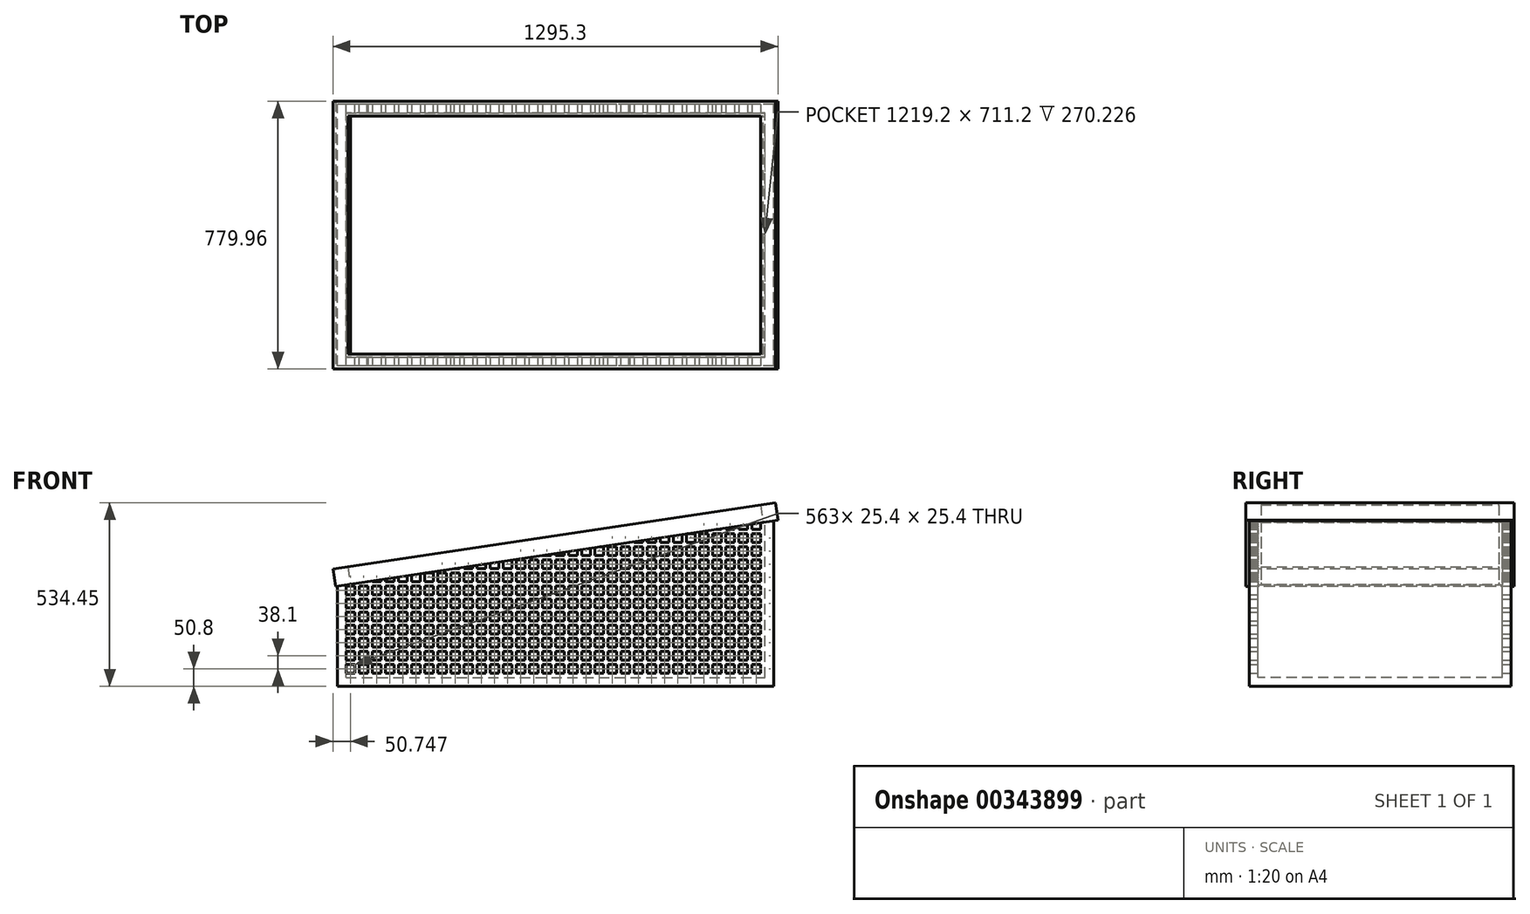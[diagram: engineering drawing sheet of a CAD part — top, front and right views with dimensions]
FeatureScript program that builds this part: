
annotation { "Feature Type Name" : "Feature", "Feature Type Description" : "" }
export const myFeature = defineFeature(function(context is Context, id is Id, definition is map)
    precondition{}
    {
        {
            var Q0;
            Q0=qCreatedBy(makeId("Top.planeOp"),FACE);
            var sketch = newSketch(context, id + "F0", { "sketchPlane" : qUnion([Q0])});
            skLineSegment(sketch, "E0.bottom", {"start": v(619.8, -571.34) * mm, "end": v(-650.2, -571.34) * mm});
            skLineSegment(sketch, "E0.top", {"start": v(619.8, 190.66) * mm, "end": v(-650.2, 190.66) * mm});
            skLineSegment(sketch, "E0.left", {"start": v(619.8, -571.34) * mm, "end": v(619.8, 190.66) * mm});
            skLineSegment(sketch, "E0.right", {"start": v(-650.2, -571.34) * mm, "end": v(-650.2, 190.66) * mm});
            skSolve(sketch);
        }
        {
            var Q0;
            Q0 = qSketchRegion(id + "F0", true);
            extrude(context, id + "F1", {"entities" : qUnion([Q0]), "depth" : 508 * mm});
        }
        {
            var Q0;
            Q0=makeQuery(id+"F1.opExtrude","SWEPT_FACE",FACE,{"disambiguationData":[OSD([sQuery(id+"F0.wireOp",EDGE,"E0.bottom")])]});
            var sketch = newSketch(context, id + "F2", { "sketchPlane" : qUnion([Q0])});
            skLineSegment(sketch, "E1.bottom", {"start": v(-650.2, 508) * mm, "end": v(619.8, 508) * mm, "construction": true});
            skLineSegment(sketch, "E1.top", {"start": v(-650.2, 317.5) * mm, "end": v(619.8, 317.5) * mm, "construction": true});
            skLineSegment(sketch, "E1.left", {"start": v(-650.2, 508) * mm, "end": v(-650.2, 317.5) * mm, "construction": true});
            skLineSegment(sketch, "E1.right", {"start": v(619.8, 508) * mm, "end": v(619.8, 317.5) * mm, "construction": true});
            skLineSegment(sketch, "E2", {"start": v(-650.2, 317.5) * mm, "end": v(619.8, 508) * mm});
            skLineSegment(sketch, "E3", {"start": v(619.8, 508) * mm, "end": v(-650.2, 508) * mm});
            skLineSegment(sketch, "E4", {"start": v(-650.2, 508) * mm, "end": v(-650.2, 317.5) * mm});
            skSolve(sketch);
        }
        {
            var Q0;
            Q0=makeQuery(id+"F1.opExtrude","CAP_FACE",FACE,{"disambiguationData":[OSD([sQuery(id+"F0.wireOp",EDGE,"E0.bottom"),sQuery(id+"F0.wireOp",EDGE,"E0.top"),sQuery(id+"F0.wireOp",EDGE,"E0.left"),sQuery(id+"F0.wireOp",EDGE,"E0.right")])],"isStart":false});
            var sketch = newSketch(context, id + "F3", { "sketchPlane" : qUnion([Q0])});
            skLineSegment(sketch, "E5.bottom", {"start": v(-624.8, 165.26) * mm, "end": v(594.4, 165.26) * mm});
            skLineSegment(sketch, "E5.top", {"start": v(-624.8, -545.94) * mm, "end": v(594.4, -545.94) * mm});
            skLineSegment(sketch, "E5.left", {"start": v(-624.8, 165.26) * mm, "end": v(-624.8, -545.94) * mm});
            skLineSegment(sketch, "E5.right", {"start": v(594.4, 165.26) * mm, "end": v(594.4, -545.94) * mm});
            skSolve(sketch);
        }
        {
            var Q0;
            Q0=makeQuery(id+"F3.imprint","IMPRINT",FACE,{"disambiguationData":[TD([[makeQuery(id+"F3.imprint","IMPRINT",EDGE,{"derivedFrom":sQuery(id+"F3.wireOp",EDGE,"E5.bottom")}),-1.0]])]});
            extrude(context, id + "F4", {"entities" : qUnion([Q0]), "operationType" : NewBodyOperationType.REMOVE, "oppositeDirection" : true, "depth" : 482.6 * mm});
        }
        {
            var Q0;
            Q0=makeQuery(id+"F2.imprint","IMPRINT",FACE,{"disambiguationData":[TD([[makeQuery(id+"F2.imprint","IMPRINT",EDGE,{"derivedFrom":sQuery(id+"F2.wireOp",EDGE,"E2")}),1.0]])]});
            extrude(context, id + "F5", {"entities" : qUnion([Q0]), "operationType" : NewBodyOperationType.REMOVE, "oppositeDirection" : true, "depth" : 762 * mm});
        }
        {
            var Q0;
            Q0=makeQuery(id+"F5.boolean.opBoolean","COPY",FACE,{"derivedFrom":makeQuery(id+"F5.opExtrude","SWEPT_FACE",FACE,{"disambiguationData":[OSD([sQuery(id+"F2.wireOp",EDGE,"E2")])]})});
            var sketch = newSketch(context, id + "F6", { "sketchPlane" : qUnion([Q0])});
            skLineSegment(sketch, "E6.bottom", {"start": v(-570.22, 165.26) * mm, "end": v(662.62, 165.26) * mm, "construction": true});
            skLineSegment(sketch, "E6.top", {"start": v(-570.22, -545.94) * mm, "end": v(662.62, -545.94) * mm, "construction": true});
            skLineSegment(sketch, "E6.left", {"start": v(-570.22, 165.26) * mm, "end": v(-570.22, -545.94) * mm, "construction": true});
            skLineSegment(sketch, "E6.right", {"start": v(662.62, 165.26) * mm, "end": v(662.62, -545.94) * mm, "construction": true});
            skLineSegment(sketch, "E7.bottom", {"start": v(688.3, 190.66) * mm, "end": v(-595.9, 190.66) * mm, "construction": true});
            skLineSegment(sketch, "E7.top", {"start": v(688.3, -571.34) * mm, "end": v(-595.9, -571.34) * mm, "construction": true});
            skLineSegment(sketch, "E7.left", {"start": v(688.3, 190.66) * mm, "end": v(688.3, -571.34) * mm, "construction": true});
            skLineSegment(sketch, "E7.right", {"start": v(-595.9, 190.66) * mm, "end": v(-595.9, -571.34) * mm, "construction": true});
            skLineSegment(sketch, "E8", {"start": v(-595.9, 190.66) * mm, "end": v(-604.88, 199.64) * mm, "construction": true});
            skLineSegment(sketch, "E9", {"start": v(-570.22, 165.26) * mm, "end": v(-561.24, 156.28) * mm, "construction": true});
            skLineSegment(sketch, "E10", {"start": v(662.62, -545.94) * mm, "end": v(653.64, -536.96) * mm, "construction": true});
            skLineSegment(sketch, "E11", {"start": v(688.3, -571.34) * mm, "end": v(697.29, -580.32) * mm, "construction": true});
            skLineSegment(sketch, "E12.bottom", {"start": v(-604.88, 199.64) * mm, "end": v(697.29, 199.64) * mm});
            skLineSegment(sketch, "E12.top", {"start": v(-604.88, -580.32) * mm, "end": v(697.29, -580.32) * mm});
            skLineSegment(sketch, "E12.left", {"start": v(-604.88, 199.64) * mm, "end": v(-604.88, -580.32) * mm});
            skLineSegment(sketch, "E12.right", {"start": v(697.29, 199.64) * mm, "end": v(697.29, -580.32) * mm});
            skLineSegment(sketch, "E13.bottom", {"start": v(653.64, -536.96) * mm, "end": v(-561.24, -536.96) * mm});
            skLineSegment(sketch, "E13.top", {"start": v(653.64, 156.28) * mm, "end": v(-561.24, 156.28) * mm});
            skLineSegment(sketch, "E13.left", {"start": v(653.64, -536.96) * mm, "end": v(653.64, 156.28) * mm});
            skLineSegment(sketch, "E13.right", {"start": v(-561.24, -536.96) * mm, "end": v(-561.24, 156.28) * mm});
            skSolve(sketch);
        }
        {
            var Q0;
            Q0=makeQuery(id+"F1.opExtrude","SWEPT_FACE",FACE,{"disambiguationData":[OSD([sQuery(id+"F0.wireOp",EDGE,"E0.top")])]});
            var sketch = newSketch(context, id + "F7", { "sketchPlane" : qUnion([Q0])});
            skLineSegment(sketch, "E14.bottom", {"start": v(-581.7, 63.5) * mm, "end": v(-556.3, 63.5) * mm});
            skLineSegment(sketch, "E14.top", {"start": v(-581.7, 38.1) * mm, "end": v(-556.3, 38.1) * mm});
            skLineSegment(sketch, "E14.left", {"start": v(-581.7, 63.5) * mm, "end": v(-581.7, 38.1) * mm});
            skLineSegment(sketch, "E14.right", {"start": v(-556.3, 63.5) * mm, "end": v(-556.3, 38.1) * mm});
            skLineSegment(sketch, "E15.0.1.0", {"start": v(-581.7, 101.6) * mm, "end": v(-556.3, 101.6) * mm});
            skLineSegment(sketch, "E15.0.1.1", {"start": v(-581.7, 101.6) * mm, "end": v(-581.7, 76.2) * mm});
            skLineSegment(sketch, "E15.0.1.2", {"start": v(-581.7, 76.2) * mm, "end": v(-556.3, 76.2) * mm});
            skLineSegment(sketch, "E15.0.1.3", {"start": v(-556.3, 101.6) * mm, "end": v(-556.3, 76.2) * mm});
            skLineSegment(sketch, "E15.0.2.0", {"start": v(-581.7, 139.7) * mm, "end": v(-556.3, 139.7) * mm});
            skLineSegment(sketch, "E15.0.2.1", {"start": v(-581.7, 139.7) * mm, "end": v(-581.7, 114.3) * mm});
            skLineSegment(sketch, "E15.0.2.2", {"start": v(-581.7, 114.3) * mm, "end": v(-556.3, 114.3) * mm});
            skLineSegment(sketch, "E15.0.2.3", {"start": v(-556.3, 139.7) * mm, "end": v(-556.3, 114.3) * mm});
            skLineSegment(sketch, "E15.0.3.0", {"start": v(-581.7, 177.8) * mm, "end": v(-556.3, 177.8) * mm});
            skLineSegment(sketch, "E15.0.3.1", {"start": v(-581.7, 177.8) * mm, "end": v(-581.7, 152.4) * mm});
            skLineSegment(sketch, "E15.0.3.2", {"start": v(-581.7, 152.4) * mm, "end": v(-556.3, 152.4) * mm});
            skLineSegment(sketch, "E15.0.3.3", {"start": v(-556.3, 177.8) * mm, "end": v(-556.3, 152.4) * mm});
            skLineSegment(sketch, "E15.0.4.0", {"start": v(-581.7, 215.9) * mm, "end": v(-556.3, 215.9) * mm});
            skLineSegment(sketch, "E15.0.4.1", {"start": v(-581.7, 215.9) * mm, "end": v(-581.7, 190.5) * mm});
            skLineSegment(sketch, "E15.0.4.2", {"start": v(-581.7, 190.5) * mm, "end": v(-556.3, 190.5) * mm});
            skLineSegment(sketch, "E15.0.4.3", {"start": v(-556.3, 215.9) * mm, "end": v(-556.3, 190.5) * mm});
            skLineSegment(sketch, "E15.0.5.0", {"start": v(-581.7, 254) * mm, "end": v(-556.3, 254) * mm});
            skLineSegment(sketch, "E15.0.5.1", {"start": v(-581.7, 254) * mm, "end": v(-581.7, 228.6) * mm});
            skLineSegment(sketch, "E15.0.5.2", {"start": v(-581.7, 228.6) * mm, "end": v(-556.3, 228.6) * mm});
            skLineSegment(sketch, "E15.0.5.3", {"start": v(-556.3, 254) * mm, "end": v(-556.3, 228.6) * mm});
            skLineSegment(sketch, "E15.0.6.0", {"start": v(-581.7, 292.1) * mm, "end": v(-556.3, 292.1) * mm});
            skLineSegment(sketch, "E15.0.6.1", {"start": v(-581.7, 292.1) * mm, "end": v(-581.7, 266.7) * mm});
            skLineSegment(sketch, "E15.0.6.2", {"start": v(-581.7, 266.7) * mm, "end": v(-556.3, 266.7) * mm});
            skLineSegment(sketch, "E15.0.6.3", {"start": v(-556.3, 292.1) * mm, "end": v(-556.3, 266.7) * mm});
            skLineSegment(sketch, "E15.0.7.0", {"start": v(-581.7, 330.2) * mm, "end": v(-556.3, 330.2) * mm});
            skLineSegment(sketch, "E15.0.7.1", {"start": v(-581.7, 330.2) * mm, "end": v(-581.7, 304.8) * mm});
            skLineSegment(sketch, "E15.0.7.2", {"start": v(-581.7, 304.8) * mm, "end": v(-556.3, 304.8) * mm});
            skLineSegment(sketch, "E15.0.7.3", {"start": v(-556.3, 330.2) * mm, "end": v(-556.3, 304.8) * mm});
            skLineSegment(sketch, "E15.0.8.0", {"start": v(-581.7, 368.3) * mm, "end": v(-556.3, 368.3) * mm});
            skLineSegment(sketch, "E15.0.8.1", {"start": v(-581.7, 368.3) * mm, "end": v(-581.7, 342.9) * mm});
            skLineSegment(sketch, "E15.0.8.2", {"start": v(-581.7, 342.9) * mm, "end": v(-556.3, 342.9) * mm});
            skLineSegment(sketch, "E15.0.8.3", {"start": v(-556.3, 368.3) * mm, "end": v(-556.3, 342.9) * mm});
            skLineSegment(sketch, "E15.1.0.0", {"start": v(-543.6, 63.5) * mm, "end": v(-518.2, 63.5) * mm});
            skLineSegment(sketch, "E15.1.0.1", {"start": v(-543.6, 63.5) * mm, "end": v(-543.6, 38.1) * mm});
            skLineSegment(sketch, "E15.1.0.2", {"start": v(-543.6, 38.1) * mm, "end": v(-518.2, 38.1) * mm});
            skLineSegment(sketch, "E15.1.0.3", {"start": v(-518.2, 63.5) * mm, "end": v(-518.2, 38.1) * mm});
            skLineSegment(sketch, "E15.1.1.0", {"start": v(-543.6, 101.6) * mm, "end": v(-518.2, 101.6) * mm});
            skLineSegment(sketch, "E15.1.1.1", {"start": v(-543.6, 101.6) * mm, "end": v(-543.6, 76.2) * mm});
            skLineSegment(sketch, "E15.1.1.2", {"start": v(-543.6, 76.2) * mm, "end": v(-518.2, 76.2) * mm});
            skLineSegment(sketch, "E15.1.1.3", {"start": v(-518.2, 101.6) * mm, "end": v(-518.2, 76.2) * mm});
            skLineSegment(sketch, "E15.1.2.0", {"start": v(-543.6, 139.7) * mm, "end": v(-518.2, 139.7) * mm});
            skLineSegment(sketch, "E15.1.2.1", {"start": v(-543.6, 139.7) * mm, "end": v(-543.6, 114.3) * mm});
            skLineSegment(sketch, "E15.1.2.2", {"start": v(-543.6, 114.3) * mm, "end": v(-518.2, 114.3) * mm});
            skLineSegment(sketch, "E15.1.2.3", {"start": v(-518.2, 139.7) * mm, "end": v(-518.2, 114.3) * mm});
            skLineSegment(sketch, "E15.1.3.0", {"start": v(-543.6, 177.8) * mm, "end": v(-518.2, 177.8) * mm});
            skLineSegment(sketch, "E15.1.3.1", {"start": v(-543.6, 177.8) * mm, "end": v(-543.6, 152.4) * mm});
            skLineSegment(sketch, "E15.1.3.2", {"start": v(-543.6, 152.4) * mm, "end": v(-518.2, 152.4) * mm});
            skLineSegment(sketch, "E15.1.3.3", {"start": v(-518.2, 177.8) * mm, "end": v(-518.2, 152.4) * mm});
            skLineSegment(sketch, "E15.1.4.0", {"start": v(-543.6, 215.9) * mm, "end": v(-518.2, 215.9) * mm});
            skLineSegment(sketch, "E15.1.4.1", {"start": v(-543.6, 215.9) * mm, "end": v(-543.6, 190.5) * mm});
            skLineSegment(sketch, "E15.1.4.2", {"start": v(-543.6, 190.5) * mm, "end": v(-518.2, 190.5) * mm});
            skLineSegment(sketch, "E15.1.4.3", {"start": v(-518.2, 215.9) * mm, "end": v(-518.2, 190.5) * mm});
            skLineSegment(sketch, "E15.1.5.0", {"start": v(-543.6, 254) * mm, "end": v(-518.2, 254) * mm});
            skLineSegment(sketch, "E15.1.5.1", {"start": v(-543.6, 254) * mm, "end": v(-543.6, 228.6) * mm});
            skLineSegment(sketch, "E15.1.5.2", {"start": v(-543.6, 228.6) * mm, "end": v(-518.2, 228.6) * mm});
            skLineSegment(sketch, "E15.1.5.3", {"start": v(-518.2, 254) * mm, "end": v(-518.2, 228.6) * mm});
            skLineSegment(sketch, "E15.1.6.0", {"start": v(-543.6, 292.1) * mm, "end": v(-518.2, 292.1) * mm});
            skLineSegment(sketch, "E15.1.6.1", {"start": v(-543.6, 292.1) * mm, "end": v(-543.6, 266.7) * mm});
            skLineSegment(sketch, "E15.1.6.2", {"start": v(-543.6, 266.7) * mm, "end": v(-518.2, 266.7) * mm});
            skLineSegment(sketch, "E15.1.6.3", {"start": v(-518.2, 292.1) * mm, "end": v(-518.2, 266.7) * mm});
            skLineSegment(sketch, "E15.1.7.0", {"start": v(-543.6, 330.2) * mm, "end": v(-518.2, 330.2) * mm});
            skLineSegment(sketch, "E15.1.7.1", {"start": v(-543.6, 330.2) * mm, "end": v(-543.6, 304.8) * mm});
            skLineSegment(sketch, "E15.1.7.2", {"start": v(-543.6, 304.8) * mm, "end": v(-518.2, 304.8) * mm});
            skLineSegment(sketch, "E15.1.7.3", {"start": v(-518.2, 330.2) * mm, "end": v(-518.2, 304.8) * mm});
            skLineSegment(sketch, "E15.1.8.0", {"start": v(-543.6, 368.3) * mm, "end": v(-518.2, 368.3) * mm});
            skLineSegment(sketch, "E15.1.8.1", {"start": v(-543.6, 368.3) * mm, "end": v(-543.6, 342.9) * mm});
            skLineSegment(sketch, "E15.1.8.2", {"start": v(-543.6, 342.9) * mm, "end": v(-518.2, 342.9) * mm});
            skLineSegment(sketch, "E15.1.8.3", {"start": v(-518.2, 368.3) * mm, "end": v(-518.2, 342.9) * mm});
            skLineSegment(sketch, "E15.2.0.0", {"start": v(-505.5, 63.5) * mm, "end": v(-480.1, 63.5) * mm});
            skLineSegment(sketch, "E15.2.0.1", {"start": v(-505.5, 63.5) * mm, "end": v(-505.5, 38.1) * mm});
            skLineSegment(sketch, "E15.2.0.2", {"start": v(-505.5, 38.1) * mm, "end": v(-480.1, 38.1) * mm});
            skLineSegment(sketch, "E15.2.0.3", {"start": v(-480.1, 63.5) * mm, "end": v(-480.1, 38.1) * mm});
            skLineSegment(sketch, "E15.2.1.0", {"start": v(-505.5, 101.6) * mm, "end": v(-480.1, 101.6) * mm});
            skLineSegment(sketch, "E15.2.1.1", {"start": v(-505.5, 101.6) * mm, "end": v(-505.5, 76.2) * mm});
            skLineSegment(sketch, "E15.2.1.2", {"start": v(-505.5, 76.2) * mm, "end": v(-480.1, 76.2) * mm});
            skLineSegment(sketch, "E15.2.1.3", {"start": v(-480.1, 101.6) * mm, "end": v(-480.1, 76.2) * mm});
            skLineSegment(sketch, "E15.2.2.0", {"start": v(-505.5, 139.7) * mm, "end": v(-480.1, 139.7) * mm});
            skLineSegment(sketch, "E15.2.2.1", {"start": v(-505.5, 139.7) * mm, "end": v(-505.5, 114.3) * mm});
            skLineSegment(sketch, "E15.2.2.2", {"start": v(-505.5, 114.3) * mm, "end": v(-480.1, 114.3) * mm});
            skLineSegment(sketch, "E15.2.2.3", {"start": v(-480.1, 139.7) * mm, "end": v(-480.1, 114.3) * mm});
            skLineSegment(sketch, "E15.2.3.0", {"start": v(-505.5, 177.8) * mm, "end": v(-480.1, 177.8) * mm});
            skLineSegment(sketch, "E15.2.3.1", {"start": v(-505.5, 177.8) * mm, "end": v(-505.5, 152.4) * mm});
            skLineSegment(sketch, "E15.2.3.2", {"start": v(-505.5, 152.4) * mm, "end": v(-480.1, 152.4) * mm});
            skLineSegment(sketch, "E15.2.3.3", {"start": v(-480.1, 177.8) * mm, "end": v(-480.1, 152.4) * mm});
            skLineSegment(sketch, "E15.2.4.0", {"start": v(-505.5, 215.9) * mm, "end": v(-480.1, 215.9) * mm});
            skLineSegment(sketch, "E15.2.4.1", {"start": v(-505.5, 215.9) * mm, "end": v(-505.5, 190.5) * mm});
            skLineSegment(sketch, "E15.2.4.2", {"start": v(-505.5, 190.5) * mm, "end": v(-480.1, 190.5) * mm});
            skLineSegment(sketch, "E15.2.4.3", {"start": v(-480.1, 215.9) * mm, "end": v(-480.1, 190.5) * mm});
            skLineSegment(sketch, "E15.2.5.0", {"start": v(-505.5, 254) * mm, "end": v(-480.1, 254) * mm});
            skLineSegment(sketch, "E15.2.5.1", {"start": v(-505.5, 254) * mm, "end": v(-505.5, 228.6) * mm});
            skLineSegment(sketch, "E15.2.5.2", {"start": v(-505.5, 228.6) * mm, "end": v(-480.1, 228.6) * mm});
            skLineSegment(sketch, "E15.2.5.3", {"start": v(-480.1, 254) * mm, "end": v(-480.1, 228.6) * mm});
            skLineSegment(sketch, "E15.2.6.0", {"start": v(-505.5, 292.1) * mm, "end": v(-480.1, 292.1) * mm});
            skLineSegment(sketch, "E15.2.6.1", {"start": v(-505.5, 292.1) * mm, "end": v(-505.5, 266.7) * mm});
            skLineSegment(sketch, "E15.2.6.2", {"start": v(-505.5, 266.7) * mm, "end": v(-480.1, 266.7) * mm});
            skLineSegment(sketch, "E15.2.6.3", {"start": v(-480.1, 292.1) * mm, "end": v(-480.1, 266.7) * mm});
            skLineSegment(sketch, "E15.2.7.0", {"start": v(-505.5, 330.2) * mm, "end": v(-480.1, 330.2) * mm});
            skLineSegment(sketch, "E15.2.7.1", {"start": v(-505.5, 330.2) * mm, "end": v(-505.5, 304.8) * mm});
            skLineSegment(sketch, "E15.2.7.2", {"start": v(-505.5, 304.8) * mm, "end": v(-480.1, 304.8) * mm});
            skLineSegment(sketch, "E15.2.7.3", {"start": v(-480.1, 330.2) * mm, "end": v(-480.1, 304.8) * mm});
            skLineSegment(sketch, "E15.2.8.0", {"start": v(-505.5, 368.3) * mm, "end": v(-480.1, 368.3) * mm});
            skLineSegment(sketch, "E15.2.8.1", {"start": v(-505.5, 368.3) * mm, "end": v(-505.5, 342.9) * mm});
            skLineSegment(sketch, "E15.2.8.2", {"start": v(-505.5, 342.9) * mm, "end": v(-480.1, 342.9) * mm});
            skLineSegment(sketch, "E15.2.8.3", {"start": v(-480.1, 368.3) * mm, "end": v(-480.1, 342.9) * mm});
            skLineSegment(sketch, "E15.3.0.0", {"start": v(-467.4, 63.5) * mm, "end": v(-442, 63.5) * mm});
            skLineSegment(sketch, "E15.3.0.1", {"start": v(-467.4, 63.5) * mm, "end": v(-467.4, 38.1) * mm});
            skLineSegment(sketch, "E15.3.0.2", {"start": v(-467.4, 38.1) * mm, "end": v(-442, 38.1) * mm});
            skLineSegment(sketch, "E15.3.0.3", {"start": v(-442, 63.5) * mm, "end": v(-442, 38.1) * mm});
            skLineSegment(sketch, "E15.3.1.0", {"start": v(-467.4, 101.6) * mm, "end": v(-442, 101.6) * mm});
            skLineSegment(sketch, "E15.3.1.1", {"start": v(-467.4, 101.6) * mm, "end": v(-467.4, 76.2) * mm});
            skLineSegment(sketch, "E15.3.1.2", {"start": v(-467.4, 76.2) * mm, "end": v(-442, 76.2) * mm});
            skLineSegment(sketch, "E15.3.1.3", {"start": v(-442, 101.6) * mm, "end": v(-442, 76.2) * mm});
            skLineSegment(sketch, "E15.3.2.0", {"start": v(-467.4, 139.7) * mm, "end": v(-442, 139.7) * mm});
            skLineSegment(sketch, "E15.3.2.1", {"start": v(-467.4, 139.7) * mm, "end": v(-467.4, 114.3) * mm});
            skLineSegment(sketch, "E15.3.2.2", {"start": v(-467.4, 114.3) * mm, "end": v(-442, 114.3) * mm});
            skLineSegment(sketch, "E15.3.2.3", {"start": v(-442, 139.7) * mm, "end": v(-442, 114.3) * mm});
            skLineSegment(sketch, "E15.3.3.0", {"start": v(-467.4, 177.8) * mm, "end": v(-442, 177.8) * mm});
            skLineSegment(sketch, "E15.3.3.1", {"start": v(-467.4, 177.8) * mm, "end": v(-467.4, 152.4) * mm});
            skLineSegment(sketch, "E15.3.3.2", {"start": v(-467.4, 152.4) * mm, "end": v(-442, 152.4) * mm});
            skLineSegment(sketch, "E15.3.3.3", {"start": v(-442, 177.8) * mm, "end": v(-442, 152.4) * mm});
            skLineSegment(sketch, "E15.3.4.0", {"start": v(-467.4, 215.9) * mm, "end": v(-442, 215.9) * mm});
            skLineSegment(sketch, "E15.3.4.1", {"start": v(-467.4, 215.9) * mm, "end": v(-467.4, 190.5) * mm});
            skLineSegment(sketch, "E15.3.4.2", {"start": v(-467.4, 190.5) * mm, "end": v(-442, 190.5) * mm});
            skLineSegment(sketch, "E15.3.4.3", {"start": v(-442, 215.9) * mm, "end": v(-442, 190.5) * mm});
            skLineSegment(sketch, "E15.3.5.0", {"start": v(-467.4, 254) * mm, "end": v(-442, 254) * mm});
            skLineSegment(sketch, "E15.3.5.1", {"start": v(-467.4, 254) * mm, "end": v(-467.4, 228.6) * mm});
            skLineSegment(sketch, "E15.3.5.2", {"start": v(-467.4, 228.6) * mm, "end": v(-442, 228.6) * mm});
            skLineSegment(sketch, "E15.3.5.3", {"start": v(-442, 254) * mm, "end": v(-442, 228.6) * mm});
            skLineSegment(sketch, "E15.3.6.0", {"start": v(-467.4, 292.1) * mm, "end": v(-442, 292.1) * mm});
            skLineSegment(sketch, "E15.3.6.1", {"start": v(-467.4, 292.1) * mm, "end": v(-467.4, 266.7) * mm});
            skLineSegment(sketch, "E15.3.6.2", {"start": v(-467.4, 266.7) * mm, "end": v(-442, 266.7) * mm});
            skLineSegment(sketch, "E15.3.6.3", {"start": v(-442, 292.1) * mm, "end": v(-442, 266.7) * mm});
            skLineSegment(sketch, "E15.3.7.0", {"start": v(-467.4, 330.2) * mm, "end": v(-442, 330.2) * mm});
            skLineSegment(sketch, "E15.3.7.1", {"start": v(-467.4, 330.2) * mm, "end": v(-467.4, 304.8) * mm});
            skLineSegment(sketch, "E15.3.7.2", {"start": v(-467.4, 304.8) * mm, "end": v(-442, 304.8) * mm});
            skLineSegment(sketch, "E15.3.7.3", {"start": v(-442, 330.2) * mm, "end": v(-442, 304.8) * mm});
            skLineSegment(sketch, "E15.3.8.0", {"start": v(-467.4, 368.3) * mm, "end": v(-442, 368.3) * mm});
            skLineSegment(sketch, "E15.3.8.1", {"start": v(-467.4, 368.3) * mm, "end": v(-467.4, 342.9) * mm});
            skLineSegment(sketch, "E15.3.8.2", {"start": v(-467.4, 342.9) * mm, "end": v(-442, 342.9) * mm});
            skLineSegment(sketch, "E15.3.8.3", {"start": v(-442, 368.3) * mm, "end": v(-442, 342.9) * mm});
            skLineSegment(sketch, "E15.4.0.0", {"start": v(-429.3, 63.5) * mm, "end": v(-403.9, 63.5) * mm});
            skLineSegment(sketch, "E15.4.0.1", {"start": v(-429.3, 63.5) * mm, "end": v(-429.3, 38.1) * mm});
            skLineSegment(sketch, "E15.4.0.2", {"start": v(-429.3, 38.1) * mm, "end": v(-403.9, 38.1) * mm});
            skLineSegment(sketch, "E15.4.0.3", {"start": v(-403.9, 63.5) * mm, "end": v(-403.9, 38.1) * mm});
            skLineSegment(sketch, "E15.4.1.0", {"start": v(-429.3, 101.6) * mm, "end": v(-403.9, 101.6) * mm});
            skLineSegment(sketch, "E15.4.1.1", {"start": v(-429.3, 101.6) * mm, "end": v(-429.3, 76.2) * mm});
            skLineSegment(sketch, "E15.4.1.2", {"start": v(-429.3, 76.2) * mm, "end": v(-403.9, 76.2) * mm});
            skLineSegment(sketch, "E15.4.1.3", {"start": v(-403.9, 101.6) * mm, "end": v(-403.9, 76.2) * mm});
            skLineSegment(sketch, "E15.4.2.0", {"start": v(-429.3, 139.7) * mm, "end": v(-403.9, 139.7) * mm});
            skLineSegment(sketch, "E15.4.2.1", {"start": v(-429.3, 139.7) * mm, "end": v(-429.3, 114.3) * mm});
            skLineSegment(sketch, "E15.4.2.2", {"start": v(-429.3, 114.3) * mm, "end": v(-403.9, 114.3) * mm});
            skLineSegment(sketch, "E15.4.2.3", {"start": v(-403.9, 139.7) * mm, "end": v(-403.9, 114.3) * mm});
            skLineSegment(sketch, "E15.4.3.0", {"start": v(-429.3, 177.8) * mm, "end": v(-403.9, 177.8) * mm});
            skLineSegment(sketch, "E15.4.3.1", {"start": v(-429.3, 177.8) * mm, "end": v(-429.3, 152.4) * mm});
            skLineSegment(sketch, "E15.4.3.2", {"start": v(-429.3, 152.4) * mm, "end": v(-403.9, 152.4) * mm});
            skLineSegment(sketch, "E15.4.3.3", {"start": v(-403.9, 177.8) * mm, "end": v(-403.9, 152.4) * mm});
            skLineSegment(sketch, "E15.4.4.0", {"start": v(-429.3, 215.9) * mm, "end": v(-403.9, 215.9) * mm});
            skLineSegment(sketch, "E15.4.4.1", {"start": v(-429.3, 215.9) * mm, "end": v(-429.3, 190.5) * mm});
            skLineSegment(sketch, "E15.4.4.2", {"start": v(-429.3, 190.5) * mm, "end": v(-403.9, 190.5) * mm});
            skLineSegment(sketch, "E15.4.4.3", {"start": v(-403.9, 215.9) * mm, "end": v(-403.9, 190.5) * mm});
            skLineSegment(sketch, "E15.4.5.0", {"start": v(-429.3, 254) * mm, "end": v(-403.9, 254) * mm});
            skLineSegment(sketch, "E15.4.5.1", {"start": v(-429.3, 254) * mm, "end": v(-429.3, 228.6) * mm});
            skLineSegment(sketch, "E15.4.5.2", {"start": v(-429.3, 228.6) * mm, "end": v(-403.9, 228.6) * mm});
            skLineSegment(sketch, "E15.4.5.3", {"start": v(-403.9, 254) * mm, "end": v(-403.9, 228.6) * mm});
            skLineSegment(sketch, "E15.4.6.0", {"start": v(-429.3, 292.1) * mm, "end": v(-403.9, 292.1) * mm});
            skLineSegment(sketch, "E15.4.6.1", {"start": v(-429.3, 292.1) * mm, "end": v(-429.3, 266.7) * mm});
            skLineSegment(sketch, "E15.4.6.2", {"start": v(-429.3, 266.7) * mm, "end": v(-403.9, 266.7) * mm});
            skLineSegment(sketch, "E15.4.6.3", {"start": v(-403.9, 292.1) * mm, "end": v(-403.9, 266.7) * mm});
            skLineSegment(sketch, "E15.4.7.0", {"start": v(-429.3, 330.2) * mm, "end": v(-403.9, 330.2) * mm});
            skLineSegment(sketch, "E15.4.7.1", {"start": v(-429.3, 330.2) * mm, "end": v(-429.3, 304.8) * mm});
            skLineSegment(sketch, "E15.4.7.2", {"start": v(-429.3, 304.8) * mm, "end": v(-403.9, 304.8) * mm});
            skLineSegment(sketch, "E15.4.7.3", {"start": v(-403.9, 330.2) * mm, "end": v(-403.9, 304.8) * mm});
            skLineSegment(sketch, "E15.4.8.0", {"start": v(-429.3, 368.3) * mm, "end": v(-403.9, 368.3) * mm});
            skLineSegment(sketch, "E15.4.8.1", {"start": v(-429.3, 368.3) * mm, "end": v(-429.3, 342.9) * mm});
            skLineSegment(sketch, "E15.4.8.2", {"start": v(-429.3, 342.9) * mm, "end": v(-403.9, 342.9) * mm});
            skLineSegment(sketch, "E15.4.8.3", {"start": v(-403.9, 368.3) * mm, "end": v(-403.9, 342.9) * mm});
            skLineSegment(sketch, "E15.5.0.0", {"start": v(-391.2, 63.5) * mm, "end": v(-365.8, 63.5) * mm});
            skLineSegment(sketch, "E15.5.0.1", {"start": v(-391.2, 63.5) * mm, "end": v(-391.2, 38.1) * mm});
            skLineSegment(sketch, "E15.5.0.2", {"start": v(-391.2, 38.1) * mm, "end": v(-365.8, 38.1) * mm});
            skLineSegment(sketch, "E15.5.0.3", {"start": v(-365.8, 63.5) * mm, "end": v(-365.8, 38.1) * mm});
            skLineSegment(sketch, "E15.5.1.0", {"start": v(-391.2, 101.6) * mm, "end": v(-365.8, 101.6) * mm});
            skLineSegment(sketch, "E15.5.1.1", {"start": v(-391.2, 101.6) * mm, "end": v(-391.2, 76.2) * mm});
            skLineSegment(sketch, "E15.5.1.2", {"start": v(-391.2, 76.2) * mm, "end": v(-365.8, 76.2) * mm});
            skLineSegment(sketch, "E15.5.1.3", {"start": v(-365.8, 101.6) * mm, "end": v(-365.8, 76.2) * mm});
            skLineSegment(sketch, "E15.5.2.0", {"start": v(-391.2, 139.7) * mm, "end": v(-365.8, 139.7) * mm});
            skLineSegment(sketch, "E15.5.2.1", {"start": v(-391.2, 139.7) * mm, "end": v(-391.2, 114.3) * mm});
            skLineSegment(sketch, "E15.5.2.2", {"start": v(-391.2, 114.3) * mm, "end": v(-365.8, 114.3) * mm});
            skLineSegment(sketch, "E15.5.2.3", {"start": v(-365.8, 139.7) * mm, "end": v(-365.8, 114.3) * mm});
            skLineSegment(sketch, "E15.5.3.0", {"start": v(-391.2, 177.8) * mm, "end": v(-365.8, 177.8) * mm});
            skLineSegment(sketch, "E15.5.3.1", {"start": v(-391.2, 177.8) * mm, "end": v(-391.2, 152.4) * mm});
            skLineSegment(sketch, "E15.5.3.2", {"start": v(-391.2, 152.4) * mm, "end": v(-365.8, 152.4) * mm});
            skLineSegment(sketch, "E15.5.3.3", {"start": v(-365.8, 177.8) * mm, "end": v(-365.8, 152.4) * mm});
            skLineSegment(sketch, "E15.5.4.0", {"start": v(-391.2, 215.9) * mm, "end": v(-365.8, 215.9) * mm});
            skLineSegment(sketch, "E15.5.4.1", {"start": v(-391.2, 215.9) * mm, "end": v(-391.2, 190.5) * mm});
            skLineSegment(sketch, "E15.5.4.2", {"start": v(-391.2, 190.5) * mm, "end": v(-365.8, 190.5) * mm});
            skLineSegment(sketch, "E15.5.4.3", {"start": v(-365.8, 215.9) * mm, "end": v(-365.8, 190.5) * mm});
            skLineSegment(sketch, "E15.5.5.0", {"start": v(-391.2, 254) * mm, "end": v(-365.8, 254) * mm});
            skLineSegment(sketch, "E15.5.5.1", {"start": v(-391.2, 254) * mm, "end": v(-391.2, 228.6) * mm});
            skLineSegment(sketch, "E15.5.5.2", {"start": v(-391.2, 228.6) * mm, "end": v(-365.8, 228.6) * mm});
            skLineSegment(sketch, "E15.5.5.3", {"start": v(-365.8, 254) * mm, "end": v(-365.8, 228.6) * mm});
            skLineSegment(sketch, "E15.5.6.0", {"start": v(-391.2, 292.1) * mm, "end": v(-365.8, 292.1) * mm});
            skLineSegment(sketch, "E15.5.6.1", {"start": v(-391.2, 292.1) * mm, "end": v(-391.2, 266.7) * mm});
            skLineSegment(sketch, "E15.5.6.2", {"start": v(-391.2, 266.7) * mm, "end": v(-365.8, 266.7) * mm});
            skLineSegment(sketch, "E15.5.6.3", {"start": v(-365.8, 292.1) * mm, "end": v(-365.8, 266.7) * mm});
            skLineSegment(sketch, "E15.5.7.0", {"start": v(-391.2, 330.2) * mm, "end": v(-365.8, 330.2) * mm});
            skLineSegment(sketch, "E15.5.7.1", {"start": v(-391.2, 330.2) * mm, "end": v(-391.2, 304.8) * mm});
            skLineSegment(sketch, "E15.5.7.2", {"start": v(-391.2, 304.8) * mm, "end": v(-365.8, 304.8) * mm});
            skLineSegment(sketch, "E15.5.7.3", {"start": v(-365.8, 330.2) * mm, "end": v(-365.8, 304.8) * mm});
            skLineSegment(sketch, "E15.5.8.0", {"start": v(-391.2, 368.3) * mm, "end": v(-365.8, 368.3) * mm});
            skLineSegment(sketch, "E15.5.8.1", {"start": v(-391.2, 368.3) * mm, "end": v(-391.2, 342.9) * mm});
            skLineSegment(sketch, "E15.5.8.2", {"start": v(-391.2, 342.9) * mm, "end": v(-365.8, 342.9) * mm});
            skLineSegment(sketch, "E15.5.8.3", {"start": v(-365.8, 368.3) * mm, "end": v(-365.8, 342.9) * mm});
            skLineSegment(sketch, "E15.6.0.0", {"start": v(-353.1, 63.5) * mm, "end": v(-327.7, 63.5) * mm});
            skLineSegment(sketch, "E15.6.0.1", {"start": v(-353.1, 63.5) * mm, "end": v(-353.1, 38.1) * mm});
            skLineSegment(sketch, "E15.6.0.2", {"start": v(-353.1, 38.1) * mm, "end": v(-327.7, 38.1) * mm});
            skLineSegment(sketch, "E15.6.0.3", {"start": v(-327.7, 63.5) * mm, "end": v(-327.7, 38.1) * mm});
            skLineSegment(sketch, "E15.6.1.0", {"start": v(-353.1, 101.6) * mm, "end": v(-327.7, 101.6) * mm});
            skLineSegment(sketch, "E15.6.1.1", {"start": v(-353.1, 101.6) * mm, "end": v(-353.1, 76.2) * mm});
            skLineSegment(sketch, "E15.6.1.2", {"start": v(-353.1, 76.2) * mm, "end": v(-327.7, 76.2) * mm});
            skLineSegment(sketch, "E15.6.1.3", {"start": v(-327.7, 101.6) * mm, "end": v(-327.7, 76.2) * mm});
            skLineSegment(sketch, "E15.6.2.0", {"start": v(-353.1, 139.7) * mm, "end": v(-327.7, 139.7) * mm});
            skLineSegment(sketch, "E15.6.2.1", {"start": v(-353.1, 139.7) * mm, "end": v(-353.1, 114.3) * mm});
            skLineSegment(sketch, "E15.6.2.2", {"start": v(-353.1, 114.3) * mm, "end": v(-327.7, 114.3) * mm});
            skLineSegment(sketch, "E15.6.2.3", {"start": v(-327.7, 139.7) * mm, "end": v(-327.7, 114.3) * mm});
            skLineSegment(sketch, "E15.6.3.0", {"start": v(-353.1, 177.8) * mm, "end": v(-327.7, 177.8) * mm});
            skLineSegment(sketch, "E15.6.3.1", {"start": v(-353.1, 177.8) * mm, "end": v(-353.1, 152.4) * mm});
            skLineSegment(sketch, "E15.6.3.2", {"start": v(-353.1, 152.4) * mm, "end": v(-327.7, 152.4) * mm});
            skLineSegment(sketch, "E15.6.3.3", {"start": v(-327.7, 177.8) * mm, "end": v(-327.7, 152.4) * mm});
            skLineSegment(sketch, "E15.6.4.0", {"start": v(-353.1, 215.9) * mm, "end": v(-327.7, 215.9) * mm});
            skLineSegment(sketch, "E15.6.4.1", {"start": v(-353.1, 215.9) * mm, "end": v(-353.1, 190.5) * mm});
            skLineSegment(sketch, "E15.6.4.2", {"start": v(-353.1, 190.5) * mm, "end": v(-327.7, 190.5) * mm});
            skLineSegment(sketch, "E15.6.4.3", {"start": v(-327.7, 215.9) * mm, "end": v(-327.7, 190.5) * mm});
            skLineSegment(sketch, "E15.6.5.0", {"start": v(-353.1, 254) * mm, "end": v(-327.7, 254) * mm});
            skLineSegment(sketch, "E15.6.5.1", {"start": v(-353.1, 254) * mm, "end": v(-353.1, 228.6) * mm});
            skLineSegment(sketch, "E15.6.5.2", {"start": v(-353.1, 228.6) * mm, "end": v(-327.7, 228.6) * mm});
            skLineSegment(sketch, "E15.6.5.3", {"start": v(-327.7, 254) * mm, "end": v(-327.7, 228.6) * mm});
            skLineSegment(sketch, "E15.6.6.0", {"start": v(-353.1, 292.1) * mm, "end": v(-327.7, 292.1) * mm});
            skLineSegment(sketch, "E15.6.6.1", {"start": v(-353.1, 292.1) * mm, "end": v(-353.1, 266.7) * mm});
            skLineSegment(sketch, "E15.6.6.2", {"start": v(-353.1, 266.7) * mm, "end": v(-327.7, 266.7) * mm});
            skLineSegment(sketch, "E15.6.6.3", {"start": v(-327.7, 292.1) * mm, "end": v(-327.7, 266.7) * mm});
            skLineSegment(sketch, "E15.6.7.0", {"start": v(-353.1, 330.2) * mm, "end": v(-327.7, 330.2) * mm});
            skLineSegment(sketch, "E15.6.7.1", {"start": v(-353.1, 330.2) * mm, "end": v(-353.1, 304.8) * mm});
            skLineSegment(sketch, "E15.6.7.2", {"start": v(-353.1, 304.8) * mm, "end": v(-327.7, 304.8) * mm});
            skLineSegment(sketch, "E15.6.7.3", {"start": v(-327.7, 330.2) * mm, "end": v(-327.7, 304.8) * mm});
            skLineSegment(sketch, "E15.6.8.0", {"start": v(-353.1, 368.3) * mm, "end": v(-327.7, 368.3) * mm});
            skLineSegment(sketch, "E15.6.8.1", {"start": v(-353.1, 368.3) * mm, "end": v(-353.1, 342.9) * mm});
            skLineSegment(sketch, "E15.6.8.2", {"start": v(-353.1, 342.9) * mm, "end": v(-327.7, 342.9) * mm});
            skLineSegment(sketch, "E15.6.8.3", {"start": v(-327.7, 368.3) * mm, "end": v(-327.7, 342.9) * mm});
            skLineSegment(sketch, "E15.7.0.0", {"start": v(-315, 63.5) * mm, "end": v(-289.6, 63.5) * mm});
            skLineSegment(sketch, "E15.7.0.1", {"start": v(-315, 63.5) * mm, "end": v(-315, 38.1) * mm});
            skLineSegment(sketch, "E15.7.0.2", {"start": v(-315, 38.1) * mm, "end": v(-289.6, 38.1) * mm});
            skLineSegment(sketch, "E15.7.0.3", {"start": v(-289.6, 63.5) * mm, "end": v(-289.6, 38.1) * mm});
            skLineSegment(sketch, "E15.7.1.0", {"start": v(-315, 101.6) * mm, "end": v(-289.6, 101.6) * mm});
            skLineSegment(sketch, "E15.7.1.1", {"start": v(-315, 101.6) * mm, "end": v(-315, 76.2) * mm});
            skLineSegment(sketch, "E15.7.1.2", {"start": v(-315, 76.2) * mm, "end": v(-289.6, 76.2) * mm});
            skLineSegment(sketch, "E15.7.1.3", {"start": v(-289.6, 101.6) * mm, "end": v(-289.6, 76.2) * mm});
            skLineSegment(sketch, "E15.7.2.0", {"start": v(-315, 139.7) * mm, "end": v(-289.6, 139.7) * mm});
            skLineSegment(sketch, "E15.7.2.1", {"start": v(-315, 139.7) * mm, "end": v(-315, 114.3) * mm});
            skLineSegment(sketch, "E15.7.2.2", {"start": v(-315, 114.3) * mm, "end": v(-289.6, 114.3) * mm});
            skLineSegment(sketch, "E15.7.2.3", {"start": v(-289.6, 139.7) * mm, "end": v(-289.6, 114.3) * mm});
            skLineSegment(sketch, "E15.7.3.0", {"start": v(-315, 177.8) * mm, "end": v(-289.6, 177.8) * mm});
            skLineSegment(sketch, "E15.7.3.1", {"start": v(-315, 177.8) * mm, "end": v(-315, 152.4) * mm});
            skLineSegment(sketch, "E15.7.3.2", {"start": v(-315, 152.4) * mm, "end": v(-289.6, 152.4) * mm});
            skLineSegment(sketch, "E15.7.3.3", {"start": v(-289.6, 177.8) * mm, "end": v(-289.6, 152.4) * mm});
            skLineSegment(sketch, "E15.7.4.0", {"start": v(-315, 215.9) * mm, "end": v(-289.6, 215.9) * mm});
            skLineSegment(sketch, "E15.7.4.1", {"start": v(-315, 215.9) * mm, "end": v(-315, 190.5) * mm});
            skLineSegment(sketch, "E15.7.4.2", {"start": v(-315, 190.5) * mm, "end": v(-289.6, 190.5) * mm});
            skLineSegment(sketch, "E15.7.4.3", {"start": v(-289.6, 215.9) * mm, "end": v(-289.6, 190.5) * mm});
            skLineSegment(sketch, "E15.7.5.0", {"start": v(-315, 254) * mm, "end": v(-289.6, 254) * mm});
            skLineSegment(sketch, "E15.7.5.1", {"start": v(-315, 254) * mm, "end": v(-315, 228.6) * mm});
            skLineSegment(sketch, "E15.7.5.2", {"start": v(-315, 228.6) * mm, "end": v(-289.6, 228.6) * mm});
            skLineSegment(sketch, "E15.7.5.3", {"start": v(-289.6, 254) * mm, "end": v(-289.6, 228.6) * mm});
            skLineSegment(sketch, "E15.7.6.0", {"start": v(-315, 292.1) * mm, "end": v(-289.6, 292.1) * mm});
            skLineSegment(sketch, "E15.7.6.1", {"start": v(-315, 292.1) * mm, "end": v(-315, 266.7) * mm});
            skLineSegment(sketch, "E15.7.6.2", {"start": v(-315, 266.7) * mm, "end": v(-289.6, 266.7) * mm});
            skLineSegment(sketch, "E15.7.6.3", {"start": v(-289.6, 292.1) * mm, "end": v(-289.6, 266.7) * mm});
            skLineSegment(sketch, "E15.7.7.0", {"start": v(-315, 330.2) * mm, "end": v(-289.6, 330.2) * mm});
            skLineSegment(sketch, "E15.7.7.1", {"start": v(-315, 330.2) * mm, "end": v(-315, 304.8) * mm});
            skLineSegment(sketch, "E15.7.7.2", {"start": v(-315, 304.8) * mm, "end": v(-289.6, 304.8) * mm});
            skLineSegment(sketch, "E15.7.7.3", {"start": v(-289.6, 330.2) * mm, "end": v(-289.6, 304.8) * mm});
            skLineSegment(sketch, "E15.7.8.0", {"start": v(-315, 368.3) * mm, "end": v(-289.6, 368.3) * mm});
            skLineSegment(sketch, "E15.7.8.1", {"start": v(-315, 368.3) * mm, "end": v(-315, 342.9) * mm});
            skLineSegment(sketch, "E15.7.8.2", {"start": v(-315, 342.9) * mm, "end": v(-289.6, 342.9) * mm});
            skLineSegment(sketch, "E15.7.8.3", {"start": v(-289.6, 368.3) * mm, "end": v(-289.6, 342.9) * mm});
            skLineSegment(sketch, "E15.8.0.0", {"start": v(-276.9, 63.5) * mm, "end": v(-251.5, 63.5) * mm});
            skLineSegment(sketch, "E15.8.0.1", {"start": v(-276.9, 63.5) * mm, "end": v(-276.9, 38.1) * mm});
            skLineSegment(sketch, "E15.8.0.2", {"start": v(-276.9, 38.1) * mm, "end": v(-251.5, 38.1) * mm});
            skLineSegment(sketch, "E15.8.0.3", {"start": v(-251.5, 63.5) * mm, "end": v(-251.5, 38.1) * mm});
            skLineSegment(sketch, "E15.8.1.0", {"start": v(-276.9, 101.6) * mm, "end": v(-251.5, 101.6) * mm});
            skLineSegment(sketch, "E15.8.1.1", {"start": v(-276.9, 101.6) * mm, "end": v(-276.9, 76.2) * mm});
            skLineSegment(sketch, "E15.8.1.2", {"start": v(-276.9, 76.2) * mm, "end": v(-251.5, 76.2) * mm});
            skLineSegment(sketch, "E15.8.1.3", {"start": v(-251.5, 101.6) * mm, "end": v(-251.5, 76.2) * mm});
            skLineSegment(sketch, "E15.8.2.0", {"start": v(-276.9, 139.7) * mm, "end": v(-251.5, 139.7) * mm});
            skLineSegment(sketch, "E15.8.2.1", {"start": v(-276.9, 139.7) * mm, "end": v(-276.9, 114.3) * mm});
            skLineSegment(sketch, "E15.8.2.2", {"start": v(-276.9, 114.3) * mm, "end": v(-251.5, 114.3) * mm});
            skLineSegment(sketch, "E15.8.2.3", {"start": v(-251.5, 139.7) * mm, "end": v(-251.5, 114.3) * mm});
            skLineSegment(sketch, "E15.8.3.0", {"start": v(-276.9, 177.8) * mm, "end": v(-251.5, 177.8) * mm});
            skLineSegment(sketch, "E15.8.3.1", {"start": v(-276.9, 177.8) * mm, "end": v(-276.9, 152.4) * mm});
            skLineSegment(sketch, "E15.8.3.2", {"start": v(-276.9, 152.4) * mm, "end": v(-251.5, 152.4) * mm});
            skLineSegment(sketch, "E15.8.3.3", {"start": v(-251.5, 177.8) * mm, "end": v(-251.5, 152.4) * mm});
            skLineSegment(sketch, "E15.8.4.0", {"start": v(-276.9, 215.9) * mm, "end": v(-251.5, 215.9) * mm});
            skLineSegment(sketch, "E15.8.4.1", {"start": v(-276.9, 215.9) * mm, "end": v(-276.9, 190.5) * mm});
            skLineSegment(sketch, "E15.8.4.2", {"start": v(-276.9, 190.5) * mm, "end": v(-251.5, 190.5) * mm});
            skLineSegment(sketch, "E15.8.4.3", {"start": v(-251.5, 215.9) * mm, "end": v(-251.5, 190.5) * mm});
            skLineSegment(sketch, "E15.8.5.0", {"start": v(-276.9, 254) * mm, "end": v(-251.5, 254) * mm});
            skLineSegment(sketch, "E15.8.5.1", {"start": v(-276.9, 254) * mm, "end": v(-276.9, 228.6) * mm});
            skLineSegment(sketch, "E15.8.5.2", {"start": v(-276.9, 228.6) * mm, "end": v(-251.5, 228.6) * mm});
            skLineSegment(sketch, "E15.8.5.3", {"start": v(-251.5, 254) * mm, "end": v(-251.5, 228.6) * mm});
            skLineSegment(sketch, "E15.8.6.0", {"start": v(-276.9, 292.1) * mm, "end": v(-251.5, 292.1) * mm});
            skLineSegment(sketch, "E15.8.6.1", {"start": v(-276.9, 292.1) * mm, "end": v(-276.9, 266.7) * mm});
            skLineSegment(sketch, "E15.8.6.2", {"start": v(-276.9, 266.7) * mm, "end": v(-251.5, 266.7) * mm});
            skLineSegment(sketch, "E15.8.6.3", {"start": v(-251.5, 292.1) * mm, "end": v(-251.5, 266.7) * mm});
            skLineSegment(sketch, "E15.8.7.0", {"start": v(-276.9, 330.2) * mm, "end": v(-251.5, 330.2) * mm});
            skLineSegment(sketch, "E15.8.7.1", {"start": v(-276.9, 330.2) * mm, "end": v(-276.9, 304.8) * mm});
            skLineSegment(sketch, "E15.8.7.2", {"start": v(-276.9, 304.8) * mm, "end": v(-251.5, 304.8) * mm});
            skLineSegment(sketch, "E15.8.7.3", {"start": v(-251.5, 330.2) * mm, "end": v(-251.5, 304.8) * mm});
            skLineSegment(sketch, "E15.8.8.0", {"start": v(-276.9, 368.3) * mm, "end": v(-251.5, 368.3) * mm});
            skLineSegment(sketch, "E15.8.8.1", {"start": v(-276.9, 368.3) * mm, "end": v(-276.9, 342.9) * mm});
            skLineSegment(sketch, "E15.8.8.2", {"start": v(-276.9, 342.9) * mm, "end": v(-251.5, 342.9) * mm});
            skLineSegment(sketch, "E15.8.8.3", {"start": v(-251.5, 368.3) * mm, "end": v(-251.5, 342.9) * mm});
            skLineSegment(sketch, "E15.9.0.0", {"start": v(-238.8, 63.5) * mm, "end": v(-213.4, 63.5) * mm});
            skLineSegment(sketch, "E15.9.0.1", {"start": v(-238.8, 63.5) * mm, "end": v(-238.8, 38.1) * mm});
            skLineSegment(sketch, "E15.9.0.2", {"start": v(-238.8, 38.1) * mm, "end": v(-213.4, 38.1) * mm});
            skLineSegment(sketch, "E15.9.0.3", {"start": v(-213.4, 63.5) * mm, "end": v(-213.4, 38.1) * mm});
            skLineSegment(sketch, "E15.9.1.0", {"start": v(-238.8, 101.6) * mm, "end": v(-213.4, 101.6) * mm});
            skLineSegment(sketch, "E15.9.1.1", {"start": v(-238.8, 101.6) * mm, "end": v(-238.8, 76.2) * mm});
            skLineSegment(sketch, "E15.9.1.2", {"start": v(-238.8, 76.2) * mm, "end": v(-213.4, 76.2) * mm});
            skLineSegment(sketch, "E15.9.1.3", {"start": v(-213.4, 101.6) * mm, "end": v(-213.4, 76.2) * mm});
            skLineSegment(sketch, "E15.9.2.0", {"start": v(-238.8, 139.7) * mm, "end": v(-213.4, 139.7) * mm});
            skLineSegment(sketch, "E15.9.2.1", {"start": v(-238.8, 139.7) * mm, "end": v(-238.8, 114.3) * mm});
            skLineSegment(sketch, "E15.9.2.2", {"start": v(-238.8, 114.3) * mm, "end": v(-213.4, 114.3) * mm});
            skLineSegment(sketch, "E15.9.2.3", {"start": v(-213.4, 139.7) * mm, "end": v(-213.4, 114.3) * mm});
            skLineSegment(sketch, "E15.9.3.0", {"start": v(-238.8, 177.8) * mm, "end": v(-213.4, 177.8) * mm});
            skLineSegment(sketch, "E15.9.3.1", {"start": v(-238.8, 177.8) * mm, "end": v(-238.8, 152.4) * mm});
            skLineSegment(sketch, "E15.9.3.2", {"start": v(-238.8, 152.4) * mm, "end": v(-213.4, 152.4) * mm});
            skLineSegment(sketch, "E15.9.3.3", {"start": v(-213.4, 177.8) * mm, "end": v(-213.4, 152.4) * mm});
            skLineSegment(sketch, "E15.9.4.0", {"start": v(-238.8, 215.9) * mm, "end": v(-213.4, 215.9) * mm});
            skLineSegment(sketch, "E15.9.4.1", {"start": v(-238.8, 215.9) * mm, "end": v(-238.8, 190.5) * mm});
            skLineSegment(sketch, "E15.9.4.2", {"start": v(-238.8, 190.5) * mm, "end": v(-213.4, 190.5) * mm});
            skLineSegment(sketch, "E15.9.4.3", {"start": v(-213.4, 215.9) * mm, "end": v(-213.4, 190.5) * mm});
            skLineSegment(sketch, "E15.9.5.0", {"start": v(-238.8, 254) * mm, "end": v(-213.4, 254) * mm});
            skLineSegment(sketch, "E15.9.5.1", {"start": v(-238.8, 254) * mm, "end": v(-238.8, 228.6) * mm});
            skLineSegment(sketch, "E15.9.5.2", {"start": v(-238.8, 228.6) * mm, "end": v(-213.4, 228.6) * mm});
            skLineSegment(sketch, "E15.9.5.3", {"start": v(-213.4, 254) * mm, "end": v(-213.4, 228.6) * mm});
            skLineSegment(sketch, "E15.9.6.0", {"start": v(-238.8, 292.1) * mm, "end": v(-213.4, 292.1) * mm});
            skLineSegment(sketch, "E15.9.6.1", {"start": v(-238.8, 292.1) * mm, "end": v(-238.8, 266.7) * mm});
            skLineSegment(sketch, "E15.9.6.2", {"start": v(-238.8, 266.7) * mm, "end": v(-213.4, 266.7) * mm});
            skLineSegment(sketch, "E15.9.6.3", {"start": v(-213.4, 292.1) * mm, "end": v(-213.4, 266.7) * mm});
            skLineSegment(sketch, "E15.9.7.0", {"start": v(-238.8, 330.2) * mm, "end": v(-213.4, 330.2) * mm});
            skLineSegment(sketch, "E15.9.7.1", {"start": v(-238.8, 330.2) * mm, "end": v(-238.8, 304.8) * mm});
            skLineSegment(sketch, "E15.9.7.2", {"start": v(-238.8, 304.8) * mm, "end": v(-213.4, 304.8) * mm});
            skLineSegment(sketch, "E15.9.7.3", {"start": v(-213.4, 330.2) * mm, "end": v(-213.4, 304.8) * mm});
            skLineSegment(sketch, "E15.9.8.0", {"start": v(-238.8, 368.3) * mm, "end": v(-213.4, 368.3) * mm});
            skLineSegment(sketch, "E15.9.8.1", {"start": v(-238.8, 368.3) * mm, "end": v(-238.8, 342.9) * mm});
            skLineSegment(sketch, "E15.9.8.2", {"start": v(-238.8, 342.9) * mm, "end": v(-213.4, 342.9) * mm});
            skLineSegment(sketch, "E15.9.8.3", {"start": v(-213.4, 368.3) * mm, "end": v(-213.4, 342.9) * mm});
            skLineSegment(sketch, "E15.10.0.0", {"start": v(-200.7, 63.5) * mm, "end": v(-175.3, 63.5) * mm});
            skLineSegment(sketch, "E15.10.0.1", {"start": v(-200.7, 63.5) * mm, "end": v(-200.7, 38.1) * mm});
            skLineSegment(sketch, "E15.10.0.2", {"start": v(-200.7, 38.1) * mm, "end": v(-175.3, 38.1) * mm});
            skLineSegment(sketch, "E15.10.0.3", {"start": v(-175.3, 63.5) * mm, "end": v(-175.3, 38.1) * mm});
            skLineSegment(sketch, "E15.10.1.0", {"start": v(-200.7, 101.6) * mm, "end": v(-175.3, 101.6) * mm});
            skLineSegment(sketch, "E15.10.1.1", {"start": v(-200.7, 101.6) * mm, "end": v(-200.7, 76.2) * mm});
            skLineSegment(sketch, "E15.10.1.2", {"start": v(-200.7, 76.2) * mm, "end": v(-175.3, 76.2) * mm});
            skLineSegment(sketch, "E15.10.1.3", {"start": v(-175.3, 101.6) * mm, "end": v(-175.3, 76.2) * mm});
            skLineSegment(sketch, "E15.10.2.0", {"start": v(-200.7, 139.7) * mm, "end": v(-175.3, 139.7) * mm});
            skLineSegment(sketch, "E15.10.2.1", {"start": v(-200.7, 139.7) * mm, "end": v(-200.7, 114.3) * mm});
            skLineSegment(sketch, "E15.10.2.2", {"start": v(-200.7, 114.3) * mm, "end": v(-175.3, 114.3) * mm});
            skLineSegment(sketch, "E15.10.2.3", {"start": v(-175.3, 139.7) * mm, "end": v(-175.3, 114.3) * mm});
            skLineSegment(sketch, "E15.10.3.0", {"start": v(-200.7, 177.8) * mm, "end": v(-175.3, 177.8) * mm});
            skLineSegment(sketch, "E15.10.3.1", {"start": v(-200.7, 177.8) * mm, "end": v(-200.7, 152.4) * mm});
            skLineSegment(sketch, "E15.10.3.2", {"start": v(-200.7, 152.4) * mm, "end": v(-175.3, 152.4) * mm});
            skLineSegment(sketch, "E15.10.3.3", {"start": v(-175.3, 177.8) * mm, "end": v(-175.3, 152.4) * mm});
            skLineSegment(sketch, "E15.10.4.0", {"start": v(-200.7, 215.9) * mm, "end": v(-175.3, 215.9) * mm});
            skLineSegment(sketch, "E15.10.4.1", {"start": v(-200.7, 215.9) * mm, "end": v(-200.7, 190.5) * mm});
            skLineSegment(sketch, "E15.10.4.2", {"start": v(-200.7, 190.5) * mm, "end": v(-175.3, 190.5) * mm});
            skLineSegment(sketch, "E15.10.4.3", {"start": v(-175.3, 215.9) * mm, "end": v(-175.3, 190.5) * mm});
            skLineSegment(sketch, "E15.10.5.0", {"start": v(-200.7, 254) * mm, "end": v(-175.3, 254) * mm});
            skLineSegment(sketch, "E15.10.5.1", {"start": v(-200.7, 254) * mm, "end": v(-200.7, 228.6) * mm});
            skLineSegment(sketch, "E15.10.5.2", {"start": v(-200.7, 228.6) * mm, "end": v(-175.3, 228.6) * mm});
            skLineSegment(sketch, "E15.10.5.3", {"start": v(-175.3, 254) * mm, "end": v(-175.3, 228.6) * mm});
            skLineSegment(sketch, "E15.10.6.0", {"start": v(-200.7, 292.1) * mm, "end": v(-175.3, 292.1) * mm});
            skLineSegment(sketch, "E15.10.6.1", {"start": v(-200.7, 292.1) * mm, "end": v(-200.7, 266.7) * mm});
            skLineSegment(sketch, "E15.10.6.2", {"start": v(-200.7, 266.7) * mm, "end": v(-175.3, 266.7) * mm});
            skLineSegment(sketch, "E15.10.6.3", {"start": v(-175.3, 292.1) * mm, "end": v(-175.3, 266.7) * mm});
            skLineSegment(sketch, "E15.10.7.0", {"start": v(-200.7, 330.2) * mm, "end": v(-175.3, 330.2) * mm});
            skLineSegment(sketch, "E15.10.7.1", {"start": v(-200.7, 330.2) * mm, "end": v(-200.7, 304.8) * mm});
            skLineSegment(sketch, "E15.10.7.2", {"start": v(-200.7, 304.8) * mm, "end": v(-175.3, 304.8) * mm});
            skLineSegment(sketch, "E15.10.7.3", {"start": v(-175.3, 330.2) * mm, "end": v(-175.3, 304.8) * mm});
            skLineSegment(sketch, "E15.10.8.0", {"start": v(-200.7, 368.3) * mm, "end": v(-175.3, 368.3) * mm});
            skLineSegment(sketch, "E15.10.8.1", {"start": v(-200.7, 368.3) * mm, "end": v(-200.7, 342.9) * mm});
            skLineSegment(sketch, "E15.10.8.2", {"start": v(-200.7, 342.9) * mm, "end": v(-175.3, 342.9) * mm});
            skLineSegment(sketch, "E15.10.8.3", {"start": v(-175.3, 368.3) * mm, "end": v(-175.3, 342.9) * mm});
            skLineSegment(sketch, "E15.11.0.0", {"start": v(-162.6, 63.5) * mm, "end": v(-137.2, 63.5) * mm});
            skLineSegment(sketch, "E15.11.0.1", {"start": v(-162.6, 63.5) * mm, "end": v(-162.6, 38.1) * mm});
            skLineSegment(sketch, "E15.11.0.2", {"start": v(-162.6, 38.1) * mm, "end": v(-137.2, 38.1) * mm});
            skLineSegment(sketch, "E15.11.0.3", {"start": v(-137.2, 63.5) * mm, "end": v(-137.2, 38.1) * mm});
            skLineSegment(sketch, "E15.11.1.0", {"start": v(-162.6, 101.6) * mm, "end": v(-137.2, 101.6) * mm});
            skLineSegment(sketch, "E15.11.1.1", {"start": v(-162.6, 101.6) * mm, "end": v(-162.6, 76.2) * mm});
            skLineSegment(sketch, "E15.11.1.2", {"start": v(-162.6, 76.2) * mm, "end": v(-137.2, 76.2) * mm});
            skLineSegment(sketch, "E15.11.1.3", {"start": v(-137.2, 101.6) * mm, "end": v(-137.2, 76.2) * mm});
            skLineSegment(sketch, "E15.11.2.0", {"start": v(-162.6, 139.7) * mm, "end": v(-137.2, 139.7) * mm});
            skLineSegment(sketch, "E15.11.2.1", {"start": v(-162.6, 139.7) * mm, "end": v(-162.6, 114.3) * mm});
            skLineSegment(sketch, "E15.11.2.2", {"start": v(-162.6, 114.3) * mm, "end": v(-137.2, 114.3) * mm});
            skLineSegment(sketch, "E15.11.2.3", {"start": v(-137.2, 139.7) * mm, "end": v(-137.2, 114.3) * mm});
            skLineSegment(sketch, "E15.11.3.0", {"start": v(-162.6, 177.8) * mm, "end": v(-137.2, 177.8) * mm});
            skLineSegment(sketch, "E15.11.3.1", {"start": v(-162.6, 177.8) * mm, "end": v(-162.6, 152.4) * mm});
            skLineSegment(sketch, "E15.11.3.2", {"start": v(-162.6, 152.4) * mm, "end": v(-137.2, 152.4) * mm});
            skLineSegment(sketch, "E15.11.3.3", {"start": v(-137.2, 177.8) * mm, "end": v(-137.2, 152.4) * mm});
            skLineSegment(sketch, "E15.11.4.0", {"start": v(-162.6, 215.9) * mm, "end": v(-137.2, 215.9) * mm});
            skLineSegment(sketch, "E15.11.4.1", {"start": v(-162.6, 215.9) * mm, "end": v(-162.6, 190.5) * mm});
            skLineSegment(sketch, "E15.11.4.2", {"start": v(-162.6, 190.5) * mm, "end": v(-137.2, 190.5) * mm});
            skLineSegment(sketch, "E15.11.4.3", {"start": v(-137.2, 215.9) * mm, "end": v(-137.2, 190.5) * mm});
            skLineSegment(sketch, "E15.11.5.0", {"start": v(-162.6, 254) * mm, "end": v(-137.2, 254) * mm});
            skLineSegment(sketch, "E15.11.5.1", {"start": v(-162.6, 254) * mm, "end": v(-162.6, 228.6) * mm});
            skLineSegment(sketch, "E15.11.5.2", {"start": v(-162.6, 228.6) * mm, "end": v(-137.2, 228.6) * mm});
            skLineSegment(sketch, "E15.11.5.3", {"start": v(-137.2, 254) * mm, "end": v(-137.2, 228.6) * mm});
            skLineSegment(sketch, "E15.11.6.0", {"start": v(-162.6, 292.1) * mm, "end": v(-137.2, 292.1) * mm});
            skLineSegment(sketch, "E15.11.6.1", {"start": v(-162.6, 292.1) * mm, "end": v(-162.6, 266.7) * mm});
            skLineSegment(sketch, "E15.11.6.2", {"start": v(-162.6, 266.7) * mm, "end": v(-137.2, 266.7) * mm});
            skLineSegment(sketch, "E15.11.6.3", {"start": v(-137.2, 292.1) * mm, "end": v(-137.2, 266.7) * mm});
            skLineSegment(sketch, "E15.11.7.0", {"start": v(-162.6, 330.2) * mm, "end": v(-137.2, 330.2) * mm});
            skLineSegment(sketch, "E15.11.7.1", {"start": v(-162.6, 330.2) * mm, "end": v(-162.6, 304.8) * mm});
            skLineSegment(sketch, "E15.11.7.2", {"start": v(-162.6, 304.8) * mm, "end": v(-137.2, 304.8) * mm});
            skLineSegment(sketch, "E15.11.7.3", {"start": v(-137.2, 330.2) * mm, "end": v(-137.2, 304.8) * mm});
            skLineSegment(sketch, "E15.11.8.0", {"start": v(-162.6, 368.3) * mm, "end": v(-137.2, 368.3) * mm});
            skLineSegment(sketch, "E15.11.8.1", {"start": v(-162.6, 368.3) * mm, "end": v(-162.6, 342.9) * mm});
            skLineSegment(sketch, "E15.11.8.2", {"start": v(-162.6, 342.9) * mm, "end": v(-137.2, 342.9) * mm});
            skLineSegment(sketch, "E15.11.8.3", {"start": v(-137.2, 368.3) * mm, "end": v(-137.2, 342.9) * mm});
            skLineSegment(sketch, "E15.12.0.0", {"start": v(-124.5, 63.5) * mm, "end": v(-99.1, 63.5) * mm});
            skLineSegment(sketch, "E15.12.0.1", {"start": v(-124.5, 63.5) * mm, "end": v(-124.5, 38.1) * mm});
            skLineSegment(sketch, "E15.12.0.2", {"start": v(-124.5, 38.1) * mm, "end": v(-99.1, 38.1) * mm});
            skLineSegment(sketch, "E15.12.0.3", {"start": v(-99.1, 63.5) * mm, "end": v(-99.1, 38.1) * mm});
            skLineSegment(sketch, "E15.12.1.0", {"start": v(-124.5, 101.6) * mm, "end": v(-99.1, 101.6) * mm});
            skLineSegment(sketch, "E15.12.1.1", {"start": v(-124.5, 101.6) * mm, "end": v(-124.5, 76.2) * mm});
            skLineSegment(sketch, "E15.12.1.2", {"start": v(-124.5, 76.2) * mm, "end": v(-99.1, 76.2) * mm});
            skLineSegment(sketch, "E15.12.1.3", {"start": v(-99.1, 101.6) * mm, "end": v(-99.1, 76.2) * mm});
            skLineSegment(sketch, "E15.12.2.0", {"start": v(-124.5, 139.7) * mm, "end": v(-99.1, 139.7) * mm});
            skLineSegment(sketch, "E15.12.2.1", {"start": v(-124.5, 139.7) * mm, "end": v(-124.5, 114.3) * mm});
            skLineSegment(sketch, "E15.12.2.2", {"start": v(-124.5, 114.3) * mm, "end": v(-99.1, 114.3) * mm});
            skLineSegment(sketch, "E15.12.2.3", {"start": v(-99.1, 139.7) * mm, "end": v(-99.1, 114.3) * mm});
            skLineSegment(sketch, "E15.12.3.0", {"start": v(-124.5, 177.8) * mm, "end": v(-99.1, 177.8) * mm});
            skLineSegment(sketch, "E15.12.3.1", {"start": v(-124.5, 177.8) * mm, "end": v(-124.5, 152.4) * mm});
            skLineSegment(sketch, "E15.12.3.2", {"start": v(-124.5, 152.4) * mm, "end": v(-99.1, 152.4) * mm});
            skLineSegment(sketch, "E15.12.3.3", {"start": v(-99.1, 177.8) * mm, "end": v(-99.1, 152.4) * mm});
            skLineSegment(sketch, "E15.12.4.0", {"start": v(-124.5, 215.9) * mm, "end": v(-99.1, 215.9) * mm});
            skLineSegment(sketch, "E15.12.4.1", {"start": v(-124.5, 215.9) * mm, "end": v(-124.5, 190.5) * mm});
            skLineSegment(sketch, "E15.12.4.2", {"start": v(-124.5, 190.5) * mm, "end": v(-99.1, 190.5) * mm});
            skLineSegment(sketch, "E15.12.4.3", {"start": v(-99.1, 215.9) * mm, "end": v(-99.1, 190.5) * mm});
            skLineSegment(sketch, "E15.12.5.0", {"start": v(-124.5, 254) * mm, "end": v(-99.1, 254) * mm});
            skLineSegment(sketch, "E15.12.5.1", {"start": v(-124.5, 254) * mm, "end": v(-124.5, 228.6) * mm});
            skLineSegment(sketch, "E15.12.5.2", {"start": v(-124.5, 228.6) * mm, "end": v(-99.1, 228.6) * mm});
            skLineSegment(sketch, "E15.12.5.3", {"start": v(-99.1, 254) * mm, "end": v(-99.1, 228.6) * mm});
            skLineSegment(sketch, "E15.12.6.0", {"start": v(-124.5, 292.1) * mm, "end": v(-99.1, 292.1) * mm});
            skLineSegment(sketch, "E15.12.6.1", {"start": v(-124.5, 292.1) * mm, "end": v(-124.5, 266.7) * mm});
            skLineSegment(sketch, "E15.12.6.2", {"start": v(-124.5, 266.7) * mm, "end": v(-99.1, 266.7) * mm});
            skLineSegment(sketch, "E15.12.6.3", {"start": v(-99.1, 292.1) * mm, "end": v(-99.1, 266.7) * mm});
            skLineSegment(sketch, "E15.12.7.0", {"start": v(-124.5, 330.2) * mm, "end": v(-99.1, 330.2) * mm});
            skLineSegment(sketch, "E15.12.7.1", {"start": v(-124.5, 330.2) * mm, "end": v(-124.5, 304.8) * mm});
            skLineSegment(sketch, "E15.12.7.2", {"start": v(-124.5, 304.8) * mm, "end": v(-99.1, 304.8) * mm});
            skLineSegment(sketch, "E15.12.7.3", {"start": v(-99.1, 330.2) * mm, "end": v(-99.1, 304.8) * mm});
            skLineSegment(sketch, "E15.12.8.0", {"start": v(-124.5, 368.3) * mm, "end": v(-99.1, 368.3) * mm});
            skLineSegment(sketch, "E15.12.8.1", {"start": v(-124.5, 368.3) * mm, "end": v(-124.5, 342.9) * mm});
            skLineSegment(sketch, "E15.12.8.2", {"start": v(-124.5, 342.9) * mm, "end": v(-99.1, 342.9) * mm});
            skLineSegment(sketch, "E15.12.8.3", {"start": v(-99.1, 368.3) * mm, "end": v(-99.1, 342.9) * mm});
            skLineSegment(sketch, "E15.13.0.0", {"start": v(-86.4, 63.5) * mm, "end": v(-61, 63.5) * mm});
            skLineSegment(sketch, "E15.13.0.1", {"start": v(-86.4, 63.5) * mm, "end": v(-86.4, 38.1) * mm});
            skLineSegment(sketch, "E15.13.0.2", {"start": v(-86.4, 38.1) * mm, "end": v(-61, 38.1) * mm});
            skLineSegment(sketch, "E15.13.0.3", {"start": v(-61, 63.5) * mm, "end": v(-61, 38.1) * mm});
            skLineSegment(sketch, "E15.13.1.0", {"start": v(-86.4, 101.6) * mm, "end": v(-61, 101.6) * mm});
            skLineSegment(sketch, "E15.13.1.1", {"start": v(-86.4, 101.6) * mm, "end": v(-86.4, 76.2) * mm});
            skLineSegment(sketch, "E15.13.1.2", {"start": v(-86.4, 76.2) * mm, "end": v(-61, 76.2) * mm});
            skLineSegment(sketch, "E15.13.1.3", {"start": v(-61, 101.6) * mm, "end": v(-61, 76.2) * mm});
            skLineSegment(sketch, "E15.13.2.0", {"start": v(-86.4, 139.7) * mm, "end": v(-61, 139.7) * mm});
            skLineSegment(sketch, "E15.13.2.1", {"start": v(-86.4, 139.7) * mm, "end": v(-86.4, 114.3) * mm});
            skLineSegment(sketch, "E15.13.2.2", {"start": v(-86.4, 114.3) * mm, "end": v(-61, 114.3) * mm});
            skLineSegment(sketch, "E15.13.2.3", {"start": v(-61, 139.7) * mm, "end": v(-61, 114.3) * mm});
            skLineSegment(sketch, "E15.13.3.0", {"start": v(-86.4, 177.8) * mm, "end": v(-61, 177.8) * mm});
            skLineSegment(sketch, "E15.13.3.1", {"start": v(-86.4, 177.8) * mm, "end": v(-86.4, 152.4) * mm});
            skLineSegment(sketch, "E15.13.3.2", {"start": v(-86.4, 152.4) * mm, "end": v(-61, 152.4) * mm});
            skLineSegment(sketch, "E15.13.3.3", {"start": v(-61, 177.8) * mm, "end": v(-61, 152.4) * mm});
            skLineSegment(sketch, "E15.13.4.0", {"start": v(-86.4, 215.9) * mm, "end": v(-61, 215.9) * mm});
            skLineSegment(sketch, "E15.13.4.1", {"start": v(-86.4, 215.9) * mm, "end": v(-86.4, 190.5) * mm});
            skLineSegment(sketch, "E15.13.4.2", {"start": v(-86.4, 190.5) * mm, "end": v(-61, 190.5) * mm});
            skLineSegment(sketch, "E15.13.4.3", {"start": v(-61, 215.9) * mm, "end": v(-61, 190.5) * mm});
            skLineSegment(sketch, "E15.13.5.0", {"start": v(-86.4, 254) * mm, "end": v(-61, 254) * mm});
            skLineSegment(sketch, "E15.13.5.1", {"start": v(-86.4, 254) * mm, "end": v(-86.4, 228.6) * mm});
            skLineSegment(sketch, "E15.13.5.2", {"start": v(-86.4, 228.6) * mm, "end": v(-61, 228.6) * mm});
            skLineSegment(sketch, "E15.13.5.3", {"start": v(-61, 254) * mm, "end": v(-61, 228.6) * mm});
            skLineSegment(sketch, "E15.13.6.0", {"start": v(-86.4, 292.1) * mm, "end": v(-61, 292.1) * mm});
            skLineSegment(sketch, "E15.13.6.1", {"start": v(-86.4, 292.1) * mm, "end": v(-86.4, 266.7) * mm});
            skLineSegment(sketch, "E15.13.6.2", {"start": v(-86.4, 266.7) * mm, "end": v(-61, 266.7) * mm});
            skLineSegment(sketch, "E15.13.6.3", {"start": v(-61, 292.1) * mm, "end": v(-61, 266.7) * mm});
            skLineSegment(sketch, "E15.13.7.0", {"start": v(-86.4, 330.2) * mm, "end": v(-61, 330.2) * mm});
            skLineSegment(sketch, "E15.13.7.1", {"start": v(-86.4, 330.2) * mm, "end": v(-86.4, 304.8) * mm});
            skLineSegment(sketch, "E15.13.7.2", {"start": v(-86.4, 304.8) * mm, "end": v(-61, 304.8) * mm});
            skLineSegment(sketch, "E15.13.7.3", {"start": v(-61, 330.2) * mm, "end": v(-61, 304.8) * mm});
            skLineSegment(sketch, "E15.13.8.0", {"start": v(-86.4, 368.3) * mm, "end": v(-61, 368.3) * mm});
            skLineSegment(sketch, "E15.13.8.1", {"start": v(-86.4, 368.3) * mm, "end": v(-86.4, 342.9) * mm});
            skLineSegment(sketch, "E15.13.8.2", {"start": v(-86.4, 342.9) * mm, "end": v(-61, 342.9) * mm});
            skLineSegment(sketch, "E15.13.8.3", {"start": v(-61, 368.3) * mm, "end": v(-61, 342.9) * mm});
            skLineSegment(sketch, "E15.14.0.0", {"start": v(-48.3, 63.5) * mm, "end": v(-22.9, 63.5) * mm});
            skLineSegment(sketch, "E15.14.0.1", {"start": v(-48.3, 63.5) * mm, "end": v(-48.3, 38.1) * mm});
            skLineSegment(sketch, "E15.14.0.2", {"start": v(-48.3, 38.1) * mm, "end": v(-22.9, 38.1) * mm});
            skLineSegment(sketch, "E15.14.0.3", {"start": v(-22.9, 63.5) * mm, "end": v(-22.9, 38.1) * mm});
            skLineSegment(sketch, "E15.14.1.0", {"start": v(-48.3, 101.6) * mm, "end": v(-22.9, 101.6) * mm});
            skLineSegment(sketch, "E15.14.1.1", {"start": v(-48.3, 101.6) * mm, "end": v(-48.3, 76.2) * mm});
            skLineSegment(sketch, "E15.14.1.2", {"start": v(-48.3, 76.2) * mm, "end": v(-22.9, 76.2) * mm});
            skLineSegment(sketch, "E15.14.1.3", {"start": v(-22.9, 101.6) * mm, "end": v(-22.9, 76.2) * mm});
            skLineSegment(sketch, "E15.14.2.0", {"start": v(-48.3, 139.7) * mm, "end": v(-22.9, 139.7) * mm});
            skLineSegment(sketch, "E15.14.2.1", {"start": v(-48.3, 139.7) * mm, "end": v(-48.3, 114.3) * mm});
            skLineSegment(sketch, "E15.14.2.2", {"start": v(-48.3, 114.3) * mm, "end": v(-22.9, 114.3) * mm});
            skLineSegment(sketch, "E15.14.2.3", {"start": v(-22.9, 139.7) * mm, "end": v(-22.9, 114.3) * mm});
            skLineSegment(sketch, "E15.14.3.0", {"start": v(-48.3, 177.8) * mm, "end": v(-22.9, 177.8) * mm});
            skLineSegment(sketch, "E15.14.3.1", {"start": v(-48.3, 177.8) * mm, "end": v(-48.3, 152.4) * mm});
            skLineSegment(sketch, "E15.14.3.2", {"start": v(-48.3, 152.4) * mm, "end": v(-22.9, 152.4) * mm});
            skLineSegment(sketch, "E15.14.3.3", {"start": v(-22.9, 177.8) * mm, "end": v(-22.9, 152.4) * mm});
            skLineSegment(sketch, "E15.14.4.0", {"start": v(-48.3, 215.9) * mm, "end": v(-22.9, 215.9) * mm});
            skLineSegment(sketch, "E15.14.4.1", {"start": v(-48.3, 215.9) * mm, "end": v(-48.3, 190.5) * mm});
            skLineSegment(sketch, "E15.14.4.2", {"start": v(-48.3, 190.5) * mm, "end": v(-22.9, 190.5) * mm});
            skLineSegment(sketch, "E15.14.4.3", {"start": v(-22.9, 215.9) * mm, "end": v(-22.9, 190.5) * mm});
            skLineSegment(sketch, "E15.14.5.0", {"start": v(-48.3, 254) * mm, "end": v(-22.9, 254) * mm});
            skLineSegment(sketch, "E15.14.5.1", {"start": v(-48.3, 254) * mm, "end": v(-48.3, 228.6) * mm});
            skLineSegment(sketch, "E15.14.5.2", {"start": v(-48.3, 228.6) * mm, "end": v(-22.9, 228.6) * mm});
            skLineSegment(sketch, "E15.14.5.3", {"start": v(-22.9, 254) * mm, "end": v(-22.9, 228.6) * mm});
            skLineSegment(sketch, "E15.14.6.0", {"start": v(-48.3, 292.1) * mm, "end": v(-22.9, 292.1) * mm});
            skLineSegment(sketch, "E15.14.6.1", {"start": v(-48.3, 292.1) * mm, "end": v(-48.3, 266.7) * mm});
            skLineSegment(sketch, "E15.14.6.2", {"start": v(-48.3, 266.7) * mm, "end": v(-22.9, 266.7) * mm});
            skLineSegment(sketch, "E15.14.6.3", {"start": v(-22.9, 292.1) * mm, "end": v(-22.9, 266.7) * mm});
            skLineSegment(sketch, "E15.14.7.0", {"start": v(-48.3, 330.2) * mm, "end": v(-22.9, 330.2) * mm});
            skLineSegment(sketch, "E15.14.7.1", {"start": v(-48.3, 330.2) * mm, "end": v(-48.3, 304.8) * mm});
            skLineSegment(sketch, "E15.14.7.2", {"start": v(-48.3, 304.8) * mm, "end": v(-22.9, 304.8) * mm});
            skLineSegment(sketch, "E15.14.7.3", {"start": v(-22.9, 330.2) * mm, "end": v(-22.9, 304.8) * mm});
            skLineSegment(sketch, "E15.14.8.0", {"start": v(-48.3, 368.3) * mm, "end": v(-22.9, 368.3) * mm});
            skLineSegment(sketch, "E15.14.8.1", {"start": v(-48.3, 368.3) * mm, "end": v(-48.3, 342.9) * mm});
            skLineSegment(sketch, "E15.14.8.2", {"start": v(-48.3, 342.9) * mm, "end": v(-22.9, 342.9) * mm});
            skLineSegment(sketch, "E15.14.8.3", {"start": v(-22.9, 368.3) * mm, "end": v(-22.9, 342.9) * mm});
            skLineSegment(sketch, "E15.15.0.0", {"start": v(-10.2, 63.5) * mm, "end": v(15.2, 63.5) * mm});
            skLineSegment(sketch, "E15.15.0.1", {"start": v(-10.2, 63.5) * mm, "end": v(-10.2, 38.1) * mm});
            skLineSegment(sketch, "E15.15.0.2", {"start": v(-10.2, 38.1) * mm, "end": v(15.2, 38.1) * mm});
            skLineSegment(sketch, "E15.15.0.3", {"start": v(15.2, 63.5) * mm, "end": v(15.2, 38.1) * mm});
            skLineSegment(sketch, "E15.15.1.0", {"start": v(-10.2, 101.6) * mm, "end": v(15.2, 101.6) * mm});
            skLineSegment(sketch, "E15.15.1.1", {"start": v(-10.2, 101.6) * mm, "end": v(-10.2, 76.2) * mm});
            skLineSegment(sketch, "E15.15.1.2", {"start": v(-10.2, 76.2) * mm, "end": v(15.2, 76.2) * mm});
            skLineSegment(sketch, "E15.15.1.3", {"start": v(15.2, 101.6) * mm, "end": v(15.2, 76.2) * mm});
            skLineSegment(sketch, "E15.15.2.0", {"start": v(-10.2, 139.7) * mm, "end": v(15.2, 139.7) * mm});
            skLineSegment(sketch, "E15.15.2.1", {"start": v(-10.2, 139.7) * mm, "end": v(-10.2, 114.3) * mm});
            skLineSegment(sketch, "E15.15.2.2", {"start": v(-10.2, 114.3) * mm, "end": v(15.2, 114.3) * mm});
            skLineSegment(sketch, "E15.15.2.3", {"start": v(15.2, 139.7) * mm, "end": v(15.2, 114.3) * mm});
            skLineSegment(sketch, "E15.15.3.0", {"start": v(-10.2, 177.8) * mm, "end": v(15.2, 177.8) * mm});
            skLineSegment(sketch, "E15.15.3.1", {"start": v(-10.2, 177.8) * mm, "end": v(-10.2, 152.4) * mm});
            skLineSegment(sketch, "E15.15.3.2", {"start": v(-10.2, 152.4) * mm, "end": v(15.2, 152.4) * mm});
            skLineSegment(sketch, "E15.15.3.3", {"start": v(15.2, 177.8) * mm, "end": v(15.2, 152.4) * mm});
            skLineSegment(sketch, "E15.15.4.0", {"start": v(-10.2, 215.9) * mm, "end": v(15.2, 215.9) * mm});
            skLineSegment(sketch, "E15.15.4.1", {"start": v(-10.2, 215.9) * mm, "end": v(-10.2, 190.5) * mm});
            skLineSegment(sketch, "E15.15.4.2", {"start": v(-10.2, 190.5) * mm, "end": v(15.2, 190.5) * mm});
            skLineSegment(sketch, "E15.15.4.3", {"start": v(15.2, 215.9) * mm, "end": v(15.2, 190.5) * mm});
            skLineSegment(sketch, "E15.15.5.0", {"start": v(-10.2, 254) * mm, "end": v(15.2, 254) * mm});
            skLineSegment(sketch, "E15.15.5.1", {"start": v(-10.2, 254) * mm, "end": v(-10.2, 228.6) * mm});
            skLineSegment(sketch, "E15.15.5.2", {"start": v(-10.2, 228.6) * mm, "end": v(15.2, 228.6) * mm});
            skLineSegment(sketch, "E15.15.5.3", {"start": v(15.2, 254) * mm, "end": v(15.2, 228.6) * mm});
            skLineSegment(sketch, "E15.15.6.0", {"start": v(-10.2, 292.1) * mm, "end": v(15.2, 292.1) * mm});
            skLineSegment(sketch, "E15.15.6.1", {"start": v(-10.2, 292.1) * mm, "end": v(-10.2, 266.7) * mm});
            skLineSegment(sketch, "E15.15.6.2", {"start": v(-10.2, 266.7) * mm, "end": v(15.2, 266.7) * mm});
            skLineSegment(sketch, "E15.15.6.3", {"start": v(15.2, 292.1) * mm, "end": v(15.2, 266.7) * mm});
            skLineSegment(sketch, "E15.15.7.0", {"start": v(-10.2, 330.2) * mm, "end": v(15.2, 330.2) * mm});
            skLineSegment(sketch, "E15.15.7.1", {"start": v(-10.2, 330.2) * mm, "end": v(-10.2, 304.8) * mm});
            skLineSegment(sketch, "E15.15.7.2", {"start": v(-10.2, 304.8) * mm, "end": v(15.2, 304.8) * mm});
            skLineSegment(sketch, "E15.15.7.3", {"start": v(15.2, 330.2) * mm, "end": v(15.2, 304.8) * mm});
            skLineSegment(sketch, "E15.15.8.0", {"start": v(-10.2, 368.3) * mm, "end": v(15.2, 368.3) * mm});
            skLineSegment(sketch, "E15.15.8.1", {"start": v(-10.2, 368.3) * mm, "end": v(-10.2, 342.9) * mm});
            skLineSegment(sketch, "E15.15.8.2", {"start": v(-10.2, 342.9) * mm, "end": v(15.2, 342.9) * mm});
            skLineSegment(sketch, "E15.15.8.3", {"start": v(15.2, 368.3) * mm, "end": v(15.2, 342.9) * mm});
            skLineSegment(sketch, "E15.16.0.0", {"start": v(27.9, 63.5) * mm, "end": v(53.3, 63.5) * mm});
            skLineSegment(sketch, "E15.16.0.1", {"start": v(27.9, 63.5) * mm, "end": v(27.9, 38.1) * mm});
            skLineSegment(sketch, "E15.16.0.2", {"start": v(27.9, 38.1) * mm, "end": v(53.3, 38.1) * mm});
            skLineSegment(sketch, "E15.16.0.3", {"start": v(53.3, 63.5) * mm, "end": v(53.3, 38.1) * mm});
            skLineSegment(sketch, "E15.16.1.0", {"start": v(27.9, 101.6) * mm, "end": v(53.3, 101.6) * mm});
            skLineSegment(sketch, "E15.16.1.1", {"start": v(27.9, 101.6) * mm, "end": v(27.9, 76.2) * mm});
            skLineSegment(sketch, "E15.16.1.2", {"start": v(27.9, 76.2) * mm, "end": v(53.3, 76.2) * mm});
            skLineSegment(sketch, "E15.16.1.3", {"start": v(53.3, 101.6) * mm, "end": v(53.3, 76.2) * mm});
            skLineSegment(sketch, "E15.16.2.0", {"start": v(27.9, 139.7) * mm, "end": v(53.3, 139.7) * mm});
            skLineSegment(sketch, "E15.16.2.1", {"start": v(27.9, 139.7) * mm, "end": v(27.9, 114.3) * mm});
            skLineSegment(sketch, "E15.16.2.2", {"start": v(27.9, 114.3) * mm, "end": v(53.3, 114.3) * mm});
            skLineSegment(sketch, "E15.16.2.3", {"start": v(53.3, 139.7) * mm, "end": v(53.3, 114.3) * mm});
            skLineSegment(sketch, "E15.16.3.0", {"start": v(27.9, 177.8) * mm, "end": v(53.3, 177.8) * mm});
            skLineSegment(sketch, "E15.16.3.1", {"start": v(27.9, 177.8) * mm, "end": v(27.9, 152.4) * mm});
            skLineSegment(sketch, "E15.16.3.2", {"start": v(27.9, 152.4) * mm, "end": v(53.3, 152.4) * mm});
            skLineSegment(sketch, "E15.16.3.3", {"start": v(53.3, 177.8) * mm, "end": v(53.3, 152.4) * mm});
            skLineSegment(sketch, "E15.16.4.0", {"start": v(27.9, 215.9) * mm, "end": v(53.3, 215.9) * mm});
            skLineSegment(sketch, "E15.16.4.1", {"start": v(27.9, 215.9) * mm, "end": v(27.9, 190.5) * mm});
            skLineSegment(sketch, "E15.16.4.2", {"start": v(27.9, 190.5) * mm, "end": v(53.3, 190.5) * mm});
            skLineSegment(sketch, "E15.16.4.3", {"start": v(53.3, 215.9) * mm, "end": v(53.3, 190.5) * mm});
            skLineSegment(sketch, "E15.16.5.0", {"start": v(27.9, 254) * mm, "end": v(53.3, 254) * mm});
            skLineSegment(sketch, "E15.16.5.1", {"start": v(27.9, 254) * mm, "end": v(27.9, 228.6) * mm});
            skLineSegment(sketch, "E15.16.5.2", {"start": v(27.9, 228.6) * mm, "end": v(53.3, 228.6) * mm});
            skLineSegment(sketch, "E15.16.5.3", {"start": v(53.3, 254) * mm, "end": v(53.3, 228.6) * mm});
            skLineSegment(sketch, "E15.16.6.0", {"start": v(27.9, 292.1) * mm, "end": v(53.3, 292.1) * mm});
            skLineSegment(sketch, "E15.16.6.1", {"start": v(27.9, 292.1) * mm, "end": v(27.9, 266.7) * mm});
            skLineSegment(sketch, "E15.16.6.2", {"start": v(27.9, 266.7) * mm, "end": v(53.3, 266.7) * mm});
            skLineSegment(sketch, "E15.16.6.3", {"start": v(53.3, 292.1) * mm, "end": v(53.3, 266.7) * mm});
            skLineSegment(sketch, "E15.16.7.0", {"start": v(27.9, 330.2) * mm, "end": v(53.3, 330.2) * mm});
            skLineSegment(sketch, "E15.16.7.1", {"start": v(27.9, 330.2) * mm, "end": v(27.9, 304.8) * mm});
            skLineSegment(sketch, "E15.16.7.2", {"start": v(27.9, 304.8) * mm, "end": v(53.3, 304.8) * mm});
            skLineSegment(sketch, "E15.16.7.3", {"start": v(53.3, 330.2) * mm, "end": v(53.3, 304.8) * mm});
            skLineSegment(sketch, "E15.16.8.0", {"start": v(27.9, 368.3) * mm, "end": v(53.3, 368.3) * mm});
            skLineSegment(sketch, "E15.16.8.1", {"start": v(27.9, 368.3) * mm, "end": v(27.9, 342.9) * mm});
            skLineSegment(sketch, "E15.16.8.2", {"start": v(27.9, 342.9) * mm, "end": v(53.3, 342.9) * mm});
            skLineSegment(sketch, "E15.16.8.3", {"start": v(53.3, 368.3) * mm, "end": v(53.3, 342.9) * mm});
            skLineSegment(sketch, "E15.17.0.0", {"start": v(66, 63.5) * mm, "end": v(91.4, 63.5) * mm});
            skLineSegment(sketch, "E15.17.0.1", {"start": v(66, 63.5) * mm, "end": v(66, 38.1) * mm});
            skLineSegment(sketch, "E15.17.0.2", {"start": v(66, 38.1) * mm, "end": v(91.4, 38.1) * mm});
            skLineSegment(sketch, "E15.17.0.3", {"start": v(91.4, 63.5) * mm, "end": v(91.4, 38.1) * mm});
            skLineSegment(sketch, "E15.17.1.0", {"start": v(66, 101.6) * mm, "end": v(91.4, 101.6) * mm});
            skLineSegment(sketch, "E15.17.1.1", {"start": v(66, 101.6) * mm, "end": v(66, 76.2) * mm});
            skLineSegment(sketch, "E15.17.1.2", {"start": v(66, 76.2) * mm, "end": v(91.4, 76.2) * mm});
            skLineSegment(sketch, "E15.17.1.3", {"start": v(91.4, 101.6) * mm, "end": v(91.4, 76.2) * mm});
            skLineSegment(sketch, "E15.17.2.0", {"start": v(66, 139.7) * mm, "end": v(91.4, 139.7) * mm});
            skLineSegment(sketch, "E15.17.2.1", {"start": v(66, 139.7) * mm, "end": v(66, 114.3) * mm});
            skLineSegment(sketch, "E15.17.2.2", {"start": v(66, 114.3) * mm, "end": v(91.4, 114.3) * mm});
            skLineSegment(sketch, "E15.17.2.3", {"start": v(91.4, 139.7) * mm, "end": v(91.4, 114.3) * mm});
            skLineSegment(sketch, "E15.17.3.0", {"start": v(66, 177.8) * mm, "end": v(91.4, 177.8) * mm});
            skLineSegment(sketch, "E15.17.3.1", {"start": v(66, 177.8) * mm, "end": v(66, 152.4) * mm});
            skLineSegment(sketch, "E15.17.3.2", {"start": v(66, 152.4) * mm, "end": v(91.4, 152.4) * mm});
            skLineSegment(sketch, "E15.17.3.3", {"start": v(91.4, 177.8) * mm, "end": v(91.4, 152.4) * mm});
            skLineSegment(sketch, "E15.17.4.0", {"start": v(66, 215.9) * mm, "end": v(91.4, 215.9) * mm});
            skLineSegment(sketch, "E15.17.4.1", {"start": v(66, 215.9) * mm, "end": v(66, 190.5) * mm});
            skLineSegment(sketch, "E15.17.4.2", {"start": v(66, 190.5) * mm, "end": v(91.4, 190.5) * mm});
            skLineSegment(sketch, "E15.17.4.3", {"start": v(91.4, 215.9) * mm, "end": v(91.4, 190.5) * mm});
            skLineSegment(sketch, "E15.17.5.0", {"start": v(66, 254) * mm, "end": v(91.4, 254) * mm});
            skLineSegment(sketch, "E15.17.5.1", {"start": v(66, 254) * mm, "end": v(66, 228.6) * mm});
            skLineSegment(sketch, "E15.17.5.2", {"start": v(66, 228.6) * mm, "end": v(91.4, 228.6) * mm});
            skLineSegment(sketch, "E15.17.5.3", {"start": v(91.4, 254) * mm, "end": v(91.4, 228.6) * mm});
            skLineSegment(sketch, "E15.17.6.0", {"start": v(66, 292.1) * mm, "end": v(91.4, 292.1) * mm});
            skLineSegment(sketch, "E15.17.6.1", {"start": v(66, 292.1) * mm, "end": v(66, 266.7) * mm});
            skLineSegment(sketch, "E15.17.6.2", {"start": v(66, 266.7) * mm, "end": v(91.4, 266.7) * mm});
            skLineSegment(sketch, "E15.17.6.3", {"start": v(91.4, 292.1) * mm, "end": v(91.4, 266.7) * mm});
            skLineSegment(sketch, "E15.17.7.0", {"start": v(66, 330.2) * mm, "end": v(91.4, 330.2) * mm});
            skLineSegment(sketch, "E15.17.7.1", {"start": v(66, 330.2) * mm, "end": v(66, 304.8) * mm});
            skLineSegment(sketch, "E15.17.7.2", {"start": v(66, 304.8) * mm, "end": v(91.4, 304.8) * mm});
            skLineSegment(sketch, "E15.17.7.3", {"start": v(91.4, 330.2) * mm, "end": v(91.4, 304.8) * mm});
            skLineSegment(sketch, "E15.17.8.0", {"start": v(66, 368.3) * mm, "end": v(91.4, 368.3) * mm});
            skLineSegment(sketch, "E15.17.8.1", {"start": v(66, 368.3) * mm, "end": v(66, 342.9) * mm});
            skLineSegment(sketch, "E15.17.8.2", {"start": v(66, 342.9) * mm, "end": v(91.4, 342.9) * mm});
            skLineSegment(sketch, "E15.17.8.3", {"start": v(91.4, 368.3) * mm, "end": v(91.4, 342.9) * mm});
            skLineSegment(sketch, "E15.18.0.0", {"start": v(104.1, 63.5) * mm, "end": v(129.5, 63.5) * mm});
            skLineSegment(sketch, "E15.18.0.1", {"start": v(104.1, 63.5) * mm, "end": v(104.1, 38.1) * mm});
            skLineSegment(sketch, "E15.18.0.2", {"start": v(104.1, 38.1) * mm, "end": v(129.5, 38.1) * mm});
            skLineSegment(sketch, "E15.18.0.3", {"start": v(129.5, 63.5) * mm, "end": v(129.5, 38.1) * mm});
            skLineSegment(sketch, "E15.18.1.0", {"start": v(104.1, 101.6) * mm, "end": v(129.5, 101.6) * mm});
            skLineSegment(sketch, "E15.18.1.1", {"start": v(104.1, 101.6) * mm, "end": v(104.1, 76.2) * mm});
            skLineSegment(sketch, "E15.18.1.2", {"start": v(104.1, 76.2) * mm, "end": v(129.5, 76.2) * mm});
            skLineSegment(sketch, "E15.18.1.3", {"start": v(129.5, 101.6) * mm, "end": v(129.5, 76.2) * mm});
            skLineSegment(sketch, "E15.18.2.0", {"start": v(104.1, 139.7) * mm, "end": v(129.5, 139.7) * mm});
            skLineSegment(sketch, "E15.18.2.1", {"start": v(104.1, 139.7) * mm, "end": v(104.1, 114.3) * mm});
            skLineSegment(sketch, "E15.18.2.2", {"start": v(104.1, 114.3) * mm, "end": v(129.5, 114.3) * mm});
            skLineSegment(sketch, "E15.18.2.3", {"start": v(129.5, 139.7) * mm, "end": v(129.5, 114.3) * mm});
            skLineSegment(sketch, "E15.18.3.0", {"start": v(104.1, 177.8) * mm, "end": v(129.5, 177.8) * mm});
            skLineSegment(sketch, "E15.18.3.1", {"start": v(104.1, 177.8) * mm, "end": v(104.1, 152.4) * mm});
            skLineSegment(sketch, "E15.18.3.2", {"start": v(104.1, 152.4) * mm, "end": v(129.5, 152.4) * mm});
            skLineSegment(sketch, "E15.18.3.3", {"start": v(129.5, 177.8) * mm, "end": v(129.5, 152.4) * mm});
            skLineSegment(sketch, "E15.18.4.0", {"start": v(104.1, 215.9) * mm, "end": v(129.5, 215.9) * mm});
            skLineSegment(sketch, "E15.18.4.1", {"start": v(104.1, 215.9) * mm, "end": v(104.1, 190.5) * mm});
            skLineSegment(sketch, "E15.18.4.2", {"start": v(104.1, 190.5) * mm, "end": v(129.5, 190.5) * mm});
            skLineSegment(sketch, "E15.18.4.3", {"start": v(129.5, 215.9) * mm, "end": v(129.5, 190.5) * mm});
            skLineSegment(sketch, "E15.18.5.0", {"start": v(104.1, 254) * mm, "end": v(129.5, 254) * mm});
            skLineSegment(sketch, "E15.18.5.1", {"start": v(104.1, 254) * mm, "end": v(104.1, 228.6) * mm});
            skLineSegment(sketch, "E15.18.5.2", {"start": v(104.1, 228.6) * mm, "end": v(129.5, 228.6) * mm});
            skLineSegment(sketch, "E15.18.5.3", {"start": v(129.5, 254) * mm, "end": v(129.5, 228.6) * mm});
            skLineSegment(sketch, "E15.18.6.0", {"start": v(104.1, 292.1) * mm, "end": v(129.5, 292.1) * mm});
            skLineSegment(sketch, "E15.18.6.1", {"start": v(104.1, 292.1) * mm, "end": v(104.1, 266.7) * mm});
            skLineSegment(sketch, "E15.18.6.2", {"start": v(104.1, 266.7) * mm, "end": v(129.5, 266.7) * mm});
            skLineSegment(sketch, "E15.18.6.3", {"start": v(129.5, 292.1) * mm, "end": v(129.5, 266.7) * mm});
            skLineSegment(sketch, "E15.18.7.0", {"start": v(104.1, 330.2) * mm, "end": v(129.5, 330.2) * mm});
            skLineSegment(sketch, "E15.18.7.1", {"start": v(104.1, 330.2) * mm, "end": v(104.1, 304.8) * mm});
            skLineSegment(sketch, "E15.18.7.2", {"start": v(104.1, 304.8) * mm, "end": v(129.5, 304.8) * mm});
            skLineSegment(sketch, "E15.18.7.3", {"start": v(129.5, 330.2) * mm, "end": v(129.5, 304.8) * mm});
            skLineSegment(sketch, "E15.18.8.0", {"start": v(104.1, 368.3) * mm, "end": v(129.5, 368.3) * mm});
            skLineSegment(sketch, "E15.18.8.1", {"start": v(104.1, 368.3) * mm, "end": v(104.1, 342.9) * mm});
            skLineSegment(sketch, "E15.18.8.2", {"start": v(104.1, 342.9) * mm, "end": v(129.5, 342.9) * mm});
            skLineSegment(sketch, "E15.18.8.3", {"start": v(129.5, 368.3) * mm, "end": v(129.5, 342.9) * mm});
            skLineSegment(sketch, "E15.19.0.0", {"start": v(142.2, 63.5) * mm, "end": v(167.6, 63.5) * mm});
            skLineSegment(sketch, "E15.19.0.1", {"start": v(142.2, 63.5) * mm, "end": v(142.2, 38.1) * mm});
            skLineSegment(sketch, "E15.19.0.2", {"start": v(142.2, 38.1) * mm, "end": v(167.6, 38.1) * mm});
            skLineSegment(sketch, "E15.19.0.3", {"start": v(167.6, 63.5) * mm, "end": v(167.6, 38.1) * mm});
            skLineSegment(sketch, "E15.19.1.0", {"start": v(142.2, 101.6) * mm, "end": v(167.6, 101.6) * mm});
            skLineSegment(sketch, "E15.19.1.1", {"start": v(142.2, 101.6) * mm, "end": v(142.2, 76.2) * mm});
            skLineSegment(sketch, "E15.19.1.2", {"start": v(142.2, 76.2) * mm, "end": v(167.6, 76.2) * mm});
            skLineSegment(sketch, "E15.19.1.3", {"start": v(167.6, 101.6) * mm, "end": v(167.6, 76.2) * mm});
            skLineSegment(sketch, "E15.19.2.0", {"start": v(142.2, 139.7) * mm, "end": v(167.6, 139.7) * mm});
            skLineSegment(sketch, "E15.19.2.1", {"start": v(142.2, 139.7) * mm, "end": v(142.2, 114.3) * mm});
            skLineSegment(sketch, "E15.19.2.2", {"start": v(142.2, 114.3) * mm, "end": v(167.6, 114.3) * mm});
            skLineSegment(sketch, "E15.19.2.3", {"start": v(167.6, 139.7) * mm, "end": v(167.6, 114.3) * mm});
            skLineSegment(sketch, "E15.19.3.0", {"start": v(142.2, 177.8) * mm, "end": v(167.6, 177.8) * mm});
            skLineSegment(sketch, "E15.19.3.1", {"start": v(142.2, 177.8) * mm, "end": v(142.2, 152.4) * mm});
            skLineSegment(sketch, "E15.19.3.2", {"start": v(142.2, 152.4) * mm, "end": v(167.6, 152.4) * mm});
            skLineSegment(sketch, "E15.19.3.3", {"start": v(167.6, 177.8) * mm, "end": v(167.6, 152.4) * mm});
            skLineSegment(sketch, "E15.19.4.0", {"start": v(142.2, 215.9) * mm, "end": v(167.6, 215.9) * mm});
            skLineSegment(sketch, "E15.19.4.1", {"start": v(142.2, 215.9) * mm, "end": v(142.2, 190.5) * mm});
            skLineSegment(sketch, "E15.19.4.2", {"start": v(142.2, 190.5) * mm, "end": v(167.6, 190.5) * mm});
            skLineSegment(sketch, "E15.19.4.3", {"start": v(167.6, 215.9) * mm, "end": v(167.6, 190.5) * mm});
            skLineSegment(sketch, "E15.19.5.0", {"start": v(142.2, 254) * mm, "end": v(167.6, 254) * mm});
            skLineSegment(sketch, "E15.19.5.1", {"start": v(142.2, 254) * mm, "end": v(142.2, 228.6) * mm});
            skLineSegment(sketch, "E15.19.5.2", {"start": v(142.2, 228.6) * mm, "end": v(167.6, 228.6) * mm});
            skLineSegment(sketch, "E15.19.5.3", {"start": v(167.6, 254) * mm, "end": v(167.6, 228.6) * mm});
            skLineSegment(sketch, "E15.19.6.0", {"start": v(142.2, 292.1) * mm, "end": v(167.6, 292.1) * mm});
            skLineSegment(sketch, "E15.19.6.1", {"start": v(142.2, 292.1) * mm, "end": v(142.2, 266.7) * mm});
            skLineSegment(sketch, "E15.19.6.2", {"start": v(142.2, 266.7) * mm, "end": v(167.6, 266.7) * mm});
            skLineSegment(sketch, "E15.19.6.3", {"start": v(167.6, 292.1) * mm, "end": v(167.6, 266.7) * mm});
            skLineSegment(sketch, "E15.19.7.0", {"start": v(142.2, 330.2) * mm, "end": v(167.6, 330.2) * mm});
            skLineSegment(sketch, "E15.19.7.1", {"start": v(142.2, 330.2) * mm, "end": v(142.2, 304.8) * mm});
            skLineSegment(sketch, "E15.19.7.2", {"start": v(142.2, 304.8) * mm, "end": v(167.6, 304.8) * mm});
            skLineSegment(sketch, "E15.19.7.3", {"start": v(167.6, 330.2) * mm, "end": v(167.6, 304.8) * mm});
            skLineSegment(sketch, "E15.19.8.0", {"start": v(142.2, 368.3) * mm, "end": v(167.6, 368.3) * mm});
            skLineSegment(sketch, "E15.19.8.1", {"start": v(142.2, 368.3) * mm, "end": v(142.2, 342.9) * mm});
            skLineSegment(sketch, "E15.19.8.2", {"start": v(142.2, 342.9) * mm, "end": v(167.6, 342.9) * mm});
            skLineSegment(sketch, "E15.19.8.3", {"start": v(167.6, 368.3) * mm, "end": v(167.6, 342.9) * mm});
            skLineSegment(sketch, "E15.20.0.0", {"start": v(180.3, 63.5) * mm, "end": v(205.7, 63.5) * mm});
            skLineSegment(sketch, "E15.20.0.1", {"start": v(180.3, 63.5) * mm, "end": v(180.3, 38.1) * mm});
            skLineSegment(sketch, "E15.20.0.2", {"start": v(180.3, 38.1) * mm, "end": v(205.7, 38.1) * mm});
            skLineSegment(sketch, "E15.20.0.3", {"start": v(205.7, 63.5) * mm, "end": v(205.7, 38.1) * mm});
            skLineSegment(sketch, "E15.20.1.0", {"start": v(180.3, 101.6) * mm, "end": v(205.7, 101.6) * mm});
            skLineSegment(sketch, "E15.20.1.1", {"start": v(180.3, 101.6) * mm, "end": v(180.3, 76.2) * mm});
            skLineSegment(sketch, "E15.20.1.2", {"start": v(180.3, 76.2) * mm, "end": v(205.7, 76.2) * mm});
            skLineSegment(sketch, "E15.20.1.3", {"start": v(205.7, 101.6) * mm, "end": v(205.7, 76.2) * mm});
            skLineSegment(sketch, "E15.20.2.0", {"start": v(180.3, 139.7) * mm, "end": v(205.7, 139.7) * mm});
            skLineSegment(sketch, "E15.20.2.1", {"start": v(180.3, 139.7) * mm, "end": v(180.3, 114.3) * mm});
            skLineSegment(sketch, "E15.20.2.2", {"start": v(180.3, 114.3) * mm, "end": v(205.7, 114.3) * mm});
            skLineSegment(sketch, "E15.20.2.3", {"start": v(205.7, 139.7) * mm, "end": v(205.7, 114.3) * mm});
            skLineSegment(sketch, "E15.20.3.0", {"start": v(180.3, 177.8) * mm, "end": v(205.7, 177.8) * mm});
            skLineSegment(sketch, "E15.20.3.1", {"start": v(180.3, 177.8) * mm, "end": v(180.3, 152.4) * mm});
            skLineSegment(sketch, "E15.20.3.2", {"start": v(180.3, 152.4) * mm, "end": v(205.7, 152.4) * mm});
            skLineSegment(sketch, "E15.20.3.3", {"start": v(205.7, 177.8) * mm, "end": v(205.7, 152.4) * mm});
            skLineSegment(sketch, "E15.20.4.0", {"start": v(180.3, 215.9) * mm, "end": v(205.7, 215.9) * mm});
            skLineSegment(sketch, "E15.20.4.1", {"start": v(180.3, 215.9) * mm, "end": v(180.3, 190.5) * mm});
            skLineSegment(sketch, "E15.20.4.2", {"start": v(180.3, 190.5) * mm, "end": v(205.7, 190.5) * mm});
            skLineSegment(sketch, "E15.20.4.3", {"start": v(205.7, 215.9) * mm, "end": v(205.7, 190.5) * mm});
            skLineSegment(sketch, "E15.20.5.0", {"start": v(180.3, 254) * mm, "end": v(205.7, 254) * mm});
            skLineSegment(sketch, "E15.20.5.1", {"start": v(180.3, 254) * mm, "end": v(180.3, 228.6) * mm});
            skLineSegment(sketch, "E15.20.5.2", {"start": v(180.3, 228.6) * mm, "end": v(205.7, 228.6) * mm});
            skLineSegment(sketch, "E15.20.5.3", {"start": v(205.7, 254) * mm, "end": v(205.7, 228.6) * mm});
            skLineSegment(sketch, "E15.20.6.0", {"start": v(180.3, 292.1) * mm, "end": v(205.7, 292.1) * mm});
            skLineSegment(sketch, "E15.20.6.1", {"start": v(180.3, 292.1) * mm, "end": v(180.3, 266.7) * mm});
            skLineSegment(sketch, "E15.20.6.2", {"start": v(180.3, 266.7) * mm, "end": v(205.7, 266.7) * mm});
            skLineSegment(sketch, "E15.20.6.3", {"start": v(205.7, 292.1) * mm, "end": v(205.7, 266.7) * mm});
            skLineSegment(sketch, "E15.20.7.0", {"start": v(180.3, 330.2) * mm, "end": v(205.7, 330.2) * mm});
            skLineSegment(sketch, "E15.20.7.1", {"start": v(180.3, 330.2) * mm, "end": v(180.3, 304.8) * mm});
            skLineSegment(sketch, "E15.20.7.2", {"start": v(180.3, 304.8) * mm, "end": v(205.7, 304.8) * mm});
            skLineSegment(sketch, "E15.20.7.3", {"start": v(205.7, 330.2) * mm, "end": v(205.7, 304.8) * mm});
            skLineSegment(sketch, "E15.20.8.0", {"start": v(180.3, 368.3) * mm, "end": v(205.7, 368.3) * mm});
            skLineSegment(sketch, "E15.20.8.1", {"start": v(180.3, 368.3) * mm, "end": v(180.3, 342.9) * mm});
            skLineSegment(sketch, "E15.20.8.2", {"start": v(180.3, 342.9) * mm, "end": v(205.7, 342.9) * mm});
            skLineSegment(sketch, "E15.20.8.3", {"start": v(205.7, 368.3) * mm, "end": v(205.7, 342.9) * mm});
            skLineSegment(sketch, "E15.21.0.0", {"start": v(218.4, 63.5) * mm, "end": v(243.8, 63.5) * mm});
            skLineSegment(sketch, "E15.21.0.1", {"start": v(218.4, 63.5) * mm, "end": v(218.4, 38.1) * mm});
            skLineSegment(sketch, "E15.21.0.2", {"start": v(218.4, 38.1) * mm, "end": v(243.8, 38.1) * mm});
            skLineSegment(sketch, "E15.21.0.3", {"start": v(243.8, 63.5) * mm, "end": v(243.8, 38.1) * mm});
            skLineSegment(sketch, "E15.21.1.0", {"start": v(218.4, 101.6) * mm, "end": v(243.8, 101.6) * mm});
            skLineSegment(sketch, "E15.21.1.1", {"start": v(218.4, 101.6) * mm, "end": v(218.4, 76.2) * mm});
            skLineSegment(sketch, "E15.21.1.2", {"start": v(218.4, 76.2) * mm, "end": v(243.8, 76.2) * mm});
            skLineSegment(sketch, "E15.21.1.3", {"start": v(243.8, 101.6) * mm, "end": v(243.8, 76.2) * mm});
            skLineSegment(sketch, "E15.21.2.0", {"start": v(218.4, 139.7) * mm, "end": v(243.8, 139.7) * mm});
            skLineSegment(sketch, "E15.21.2.1", {"start": v(218.4, 139.7) * mm, "end": v(218.4, 114.3) * mm});
            skLineSegment(sketch, "E15.21.2.2", {"start": v(218.4, 114.3) * mm, "end": v(243.8, 114.3) * mm});
            skLineSegment(sketch, "E15.21.2.3", {"start": v(243.8, 139.7) * mm, "end": v(243.8, 114.3) * mm});
            skLineSegment(sketch, "E15.21.3.0", {"start": v(218.4, 177.8) * mm, "end": v(243.8, 177.8) * mm});
            skLineSegment(sketch, "E15.21.3.1", {"start": v(218.4, 177.8) * mm, "end": v(218.4, 152.4) * mm});
            skLineSegment(sketch, "E15.21.3.2", {"start": v(218.4, 152.4) * mm, "end": v(243.8, 152.4) * mm});
            skLineSegment(sketch, "E15.21.3.3", {"start": v(243.8, 177.8) * mm, "end": v(243.8, 152.4) * mm});
            skLineSegment(sketch, "E15.21.4.0", {"start": v(218.4, 215.9) * mm, "end": v(243.8, 215.9) * mm});
            skLineSegment(sketch, "E15.21.4.1", {"start": v(218.4, 215.9) * mm, "end": v(218.4, 190.5) * mm});
            skLineSegment(sketch, "E15.21.4.2", {"start": v(218.4, 190.5) * mm, "end": v(243.8, 190.5) * mm});
            skLineSegment(sketch, "E15.21.4.3", {"start": v(243.8, 215.9) * mm, "end": v(243.8, 190.5) * mm});
            skLineSegment(sketch, "E15.21.5.0", {"start": v(218.4, 254) * mm, "end": v(243.8, 254) * mm});
            skLineSegment(sketch, "E15.21.5.1", {"start": v(218.4, 254) * mm, "end": v(218.4, 228.6) * mm});
            skLineSegment(sketch, "E15.21.5.2", {"start": v(218.4, 228.6) * mm, "end": v(243.8, 228.6) * mm});
            skLineSegment(sketch, "E15.21.5.3", {"start": v(243.8, 254) * mm, "end": v(243.8, 228.6) * mm});
            skLineSegment(sketch, "E15.21.6.0", {"start": v(218.4, 292.1) * mm, "end": v(243.8, 292.1) * mm});
            skLineSegment(sketch, "E15.21.6.1", {"start": v(218.4, 292.1) * mm, "end": v(218.4, 266.7) * mm});
            skLineSegment(sketch, "E15.21.6.2", {"start": v(218.4, 266.7) * mm, "end": v(243.8, 266.7) * mm});
            skLineSegment(sketch, "E15.21.6.3", {"start": v(243.8, 292.1) * mm, "end": v(243.8, 266.7) * mm});
            skLineSegment(sketch, "E15.21.7.0", {"start": v(218.4, 330.2) * mm, "end": v(243.8, 330.2) * mm});
            skLineSegment(sketch, "E15.21.7.1", {"start": v(218.4, 330.2) * mm, "end": v(218.4, 304.8) * mm});
            skLineSegment(sketch, "E15.21.7.2", {"start": v(218.4, 304.8) * mm, "end": v(243.8, 304.8) * mm});
            skLineSegment(sketch, "E15.21.7.3", {"start": v(243.8, 330.2) * mm, "end": v(243.8, 304.8) * mm});
            skLineSegment(sketch, "E15.21.8.0", {"start": v(218.4, 368.3) * mm, "end": v(243.8, 368.3) * mm});
            skLineSegment(sketch, "E15.21.8.1", {"start": v(218.4, 368.3) * mm, "end": v(218.4, 342.9) * mm});
            skLineSegment(sketch, "E15.21.8.2", {"start": v(218.4, 342.9) * mm, "end": v(243.8, 342.9) * mm});
            skLineSegment(sketch, "E15.21.8.3", {"start": v(243.8, 368.3) * mm, "end": v(243.8, 342.9) * mm});
            skLineSegment(sketch, "E15.22.0.0", {"start": v(256.5, 63.5) * mm, "end": v(281.9, 63.5) * mm});
            skLineSegment(sketch, "E15.22.0.1", {"start": v(256.5, 63.5) * mm, "end": v(256.5, 38.1) * mm});
            skLineSegment(sketch, "E15.22.0.2", {"start": v(256.5, 38.1) * mm, "end": v(281.9, 38.1) * mm});
            skLineSegment(sketch, "E15.22.0.3", {"start": v(281.9, 63.5) * mm, "end": v(281.9, 38.1) * mm});
            skLineSegment(sketch, "E15.22.1.0", {"start": v(256.5, 101.6) * mm, "end": v(281.9, 101.6) * mm});
            skLineSegment(sketch, "E15.22.1.1", {"start": v(256.5, 101.6) * mm, "end": v(256.5, 76.2) * mm});
            skLineSegment(sketch, "E15.22.1.2", {"start": v(256.5, 76.2) * mm, "end": v(281.9, 76.2) * mm});
            skLineSegment(sketch, "E15.22.1.3", {"start": v(281.9, 101.6) * mm, "end": v(281.9, 76.2) * mm});
            skLineSegment(sketch, "E15.22.2.0", {"start": v(256.5, 139.7) * mm, "end": v(281.9, 139.7) * mm});
            skLineSegment(sketch, "E15.22.2.1", {"start": v(256.5, 139.7) * mm, "end": v(256.5, 114.3) * mm});
            skLineSegment(sketch, "E15.22.2.2", {"start": v(256.5, 114.3) * mm, "end": v(281.9, 114.3) * mm});
            skLineSegment(sketch, "E15.22.2.3", {"start": v(281.9, 139.7) * mm, "end": v(281.9, 114.3) * mm});
            skLineSegment(sketch, "E15.22.3.0", {"start": v(256.5, 177.8) * mm, "end": v(281.9, 177.8) * mm});
            skLineSegment(sketch, "E15.22.3.1", {"start": v(256.5, 177.8) * mm, "end": v(256.5, 152.4) * mm});
            skLineSegment(sketch, "E15.22.3.2", {"start": v(256.5, 152.4) * mm, "end": v(281.9, 152.4) * mm});
            skLineSegment(sketch, "E15.22.3.3", {"start": v(281.9, 177.8) * mm, "end": v(281.9, 152.4) * mm});
            skLineSegment(sketch, "E15.22.4.0", {"start": v(256.5, 215.9) * mm, "end": v(281.9, 215.9) * mm});
            skLineSegment(sketch, "E15.22.4.1", {"start": v(256.5, 215.9) * mm, "end": v(256.5, 190.5) * mm});
            skLineSegment(sketch, "E15.22.4.2", {"start": v(256.5, 190.5) * mm, "end": v(281.9, 190.5) * mm});
            skLineSegment(sketch, "E15.22.4.3", {"start": v(281.9, 215.9) * mm, "end": v(281.9, 190.5) * mm});
            skLineSegment(sketch, "E15.22.5.0", {"start": v(256.5, 254) * mm, "end": v(281.9, 254) * mm});
            skLineSegment(sketch, "E15.22.5.1", {"start": v(256.5, 254) * mm, "end": v(256.5, 228.6) * mm});
            skLineSegment(sketch, "E15.22.5.2", {"start": v(256.5, 228.6) * mm, "end": v(281.9, 228.6) * mm});
            skLineSegment(sketch, "E15.22.5.3", {"start": v(281.9, 254) * mm, "end": v(281.9, 228.6) * mm});
            skLineSegment(sketch, "E15.22.6.0", {"start": v(256.5, 292.1) * mm, "end": v(281.9, 292.1) * mm});
            skLineSegment(sketch, "E15.22.6.1", {"start": v(256.5, 292.1) * mm, "end": v(256.5, 266.7) * mm});
            skLineSegment(sketch, "E15.22.6.2", {"start": v(256.5, 266.7) * mm, "end": v(281.9, 266.7) * mm});
            skLineSegment(sketch, "E15.22.6.3", {"start": v(281.9, 292.1) * mm, "end": v(281.9, 266.7) * mm});
            skLineSegment(sketch, "E15.22.7.0", {"start": v(256.5, 330.2) * mm, "end": v(281.9, 330.2) * mm});
            skLineSegment(sketch, "E15.22.7.1", {"start": v(256.5, 330.2) * mm, "end": v(256.5, 304.8) * mm});
            skLineSegment(sketch, "E15.22.7.2", {"start": v(256.5, 304.8) * mm, "end": v(281.9, 304.8) * mm});
            skLineSegment(sketch, "E15.22.7.3", {"start": v(281.9, 330.2) * mm, "end": v(281.9, 304.8) * mm});
            skLineSegment(sketch, "E15.22.8.0", {"start": v(256.5, 368.3) * mm, "end": v(281.9, 368.3) * mm});
            skLineSegment(sketch, "E15.22.8.1", {"start": v(256.5, 368.3) * mm, "end": v(256.5, 342.9) * mm});
            skLineSegment(sketch, "E15.22.8.2", {"start": v(256.5, 342.9) * mm, "end": v(281.9, 342.9) * mm});
            skLineSegment(sketch, "E15.22.8.3", {"start": v(281.9, 368.3) * mm, "end": v(281.9, 342.9) * mm});
            skLineSegment(sketch, "E15.23.0.0", {"start": v(294.6, 63.5) * mm, "end": v(320, 63.5) * mm});
            skLineSegment(sketch, "E15.23.0.1", {"start": v(294.6, 63.5) * mm, "end": v(294.6, 38.1) * mm});
            skLineSegment(sketch, "E15.23.0.2", {"start": v(294.6, 38.1) * mm, "end": v(320, 38.1) * mm});
            skLineSegment(sketch, "E15.23.0.3", {"start": v(320, 63.5) * mm, "end": v(320, 38.1) * mm});
            skLineSegment(sketch, "E15.23.1.0", {"start": v(294.6, 101.6) * mm, "end": v(320, 101.6) * mm});
            skLineSegment(sketch, "E15.23.1.1", {"start": v(294.6, 101.6) * mm, "end": v(294.6, 76.2) * mm});
            skLineSegment(sketch, "E15.23.1.2", {"start": v(294.6, 76.2) * mm, "end": v(320, 76.2) * mm});
            skLineSegment(sketch, "E15.23.1.3", {"start": v(320, 101.6) * mm, "end": v(320, 76.2) * mm});
            skLineSegment(sketch, "E15.23.2.0", {"start": v(294.6, 139.7) * mm, "end": v(320, 139.7) * mm});
            skLineSegment(sketch, "E15.23.2.1", {"start": v(294.6, 139.7) * mm, "end": v(294.6, 114.3) * mm});
            skLineSegment(sketch, "E15.23.2.2", {"start": v(294.6, 114.3) * mm, "end": v(320, 114.3) * mm});
            skLineSegment(sketch, "E15.23.2.3", {"start": v(320, 139.7) * mm, "end": v(320, 114.3) * mm});
            skLineSegment(sketch, "E15.23.3.0", {"start": v(294.6, 177.8) * mm, "end": v(320, 177.8) * mm});
            skLineSegment(sketch, "E15.23.3.1", {"start": v(294.6, 177.8) * mm, "end": v(294.6, 152.4) * mm});
            skLineSegment(sketch, "E15.23.3.2", {"start": v(294.6, 152.4) * mm, "end": v(320, 152.4) * mm});
            skLineSegment(sketch, "E15.23.3.3", {"start": v(320, 177.8) * mm, "end": v(320, 152.4) * mm});
            skLineSegment(sketch, "E15.23.4.0", {"start": v(294.6, 215.9) * mm, "end": v(320, 215.9) * mm});
            skLineSegment(sketch, "E15.23.4.1", {"start": v(294.6, 215.9) * mm, "end": v(294.6, 190.5) * mm});
            skLineSegment(sketch, "E15.23.4.2", {"start": v(294.6, 190.5) * mm, "end": v(320, 190.5) * mm});
            skLineSegment(sketch, "E15.23.4.3", {"start": v(320, 215.9) * mm, "end": v(320, 190.5) * mm});
            skLineSegment(sketch, "E15.23.5.0", {"start": v(294.6, 254) * mm, "end": v(320, 254) * mm});
            skLineSegment(sketch, "E15.23.5.1", {"start": v(294.6, 254) * mm, "end": v(294.6, 228.6) * mm});
            skLineSegment(sketch, "E15.23.5.2", {"start": v(294.6, 228.6) * mm, "end": v(320, 228.6) * mm});
            skLineSegment(sketch, "E15.23.5.3", {"start": v(320, 254) * mm, "end": v(320, 228.6) * mm});
            skLineSegment(sketch, "E15.23.6.0", {"start": v(294.6, 292.1) * mm, "end": v(320, 292.1) * mm});
            skLineSegment(sketch, "E15.23.6.1", {"start": v(294.6, 292.1) * mm, "end": v(294.6, 266.7) * mm});
            skLineSegment(sketch, "E15.23.6.2", {"start": v(294.6, 266.7) * mm, "end": v(320, 266.7) * mm});
            skLineSegment(sketch, "E15.23.6.3", {"start": v(320, 292.1) * mm, "end": v(320, 266.7) * mm});
            skLineSegment(sketch, "E15.23.7.0", {"start": v(294.6, 330.2) * mm, "end": v(320, 330.2) * mm});
            skLineSegment(sketch, "E15.23.7.1", {"start": v(294.6, 330.2) * mm, "end": v(294.6, 304.8) * mm});
            skLineSegment(sketch, "E15.23.7.2", {"start": v(294.6, 304.8) * mm, "end": v(320, 304.8) * mm});
            skLineSegment(sketch, "E15.23.7.3", {"start": v(320, 330.2) * mm, "end": v(320, 304.8) * mm});
            skLineSegment(sketch, "E15.23.8.0", {"start": v(294.6, 368.3) * mm, "end": v(320, 368.3) * mm});
            skLineSegment(sketch, "E15.23.8.1", {"start": v(294.6, 368.3) * mm, "end": v(294.6, 342.9) * mm});
            skLineSegment(sketch, "E15.23.8.2", {"start": v(294.6, 342.9) * mm, "end": v(320, 342.9) * mm});
            skLineSegment(sketch, "E15.23.8.3", {"start": v(320, 368.3) * mm, "end": v(320, 342.9) * mm});
            skLineSegment(sketch, "E15.direction1", {"start": v(-581.7, 63.5) * mm, "end": v(-543.6, 63.5) * mm, "construction": true});
            skLineSegment(sketch, "E15.direction2", {"start": v(-581.7, 63.5) * mm, "end": v(-581.7, 101.6) * mm, "construction": true});
            skLineSegment(sketch, "E16.0.0.9", {"start": v(-581.7, 406.4) * mm, "end": v(-556.3, 406.4) * mm});
            skLineSegment(sketch, "E16.3.0.9", {"start": v(-581.7, 406.4) * mm, "end": v(-581.7, 381) * mm});
            skLineSegment(sketch, "E16.6.0.9", {"start": v(-581.7, 381) * mm, "end": v(-556.3, 381) * mm});
            skLineSegment(sketch, "E16.9.0.9", {"start": v(-556.3, 406.4) * mm, "end": v(-556.3, 381) * mm});
            skLineSegment(sketch, "E16.0.1.9", {"start": v(-543.6, 406.4) * mm, "end": v(-518.2, 406.4) * mm});
            skLineSegment(sketch, "E16.3.1.9", {"start": v(-543.6, 406.4) * mm, "end": v(-543.6, 381) * mm});
            skLineSegment(sketch, "E16.6.1.9", {"start": v(-543.6, 381) * mm, "end": v(-518.2, 381) * mm});
            skLineSegment(sketch, "E16.9.1.9", {"start": v(-518.2, 406.4) * mm, "end": v(-518.2, 381) * mm});
            skLineSegment(sketch, "E16.0.2.9", {"start": v(-505.5, 406.4) * mm, "end": v(-480.1, 406.4) * mm});
            skLineSegment(sketch, "E16.3.2.9", {"start": v(-505.5, 406.4) * mm, "end": v(-505.5, 381) * mm});
            skLineSegment(sketch, "E16.6.2.9", {"start": v(-505.5, 381) * mm, "end": v(-480.1, 381) * mm});
            skLineSegment(sketch, "E16.9.2.9", {"start": v(-480.1, 406.4) * mm, "end": v(-480.1, 381) * mm});
            skLineSegment(sketch, "E16.0.3.9", {"start": v(-467.4, 406.4) * mm, "end": v(-442, 406.4) * mm});
            skLineSegment(sketch, "E16.3.3.9", {"start": v(-467.4, 406.4) * mm, "end": v(-467.4, 381) * mm});
            skLineSegment(sketch, "E16.6.3.9", {"start": v(-467.4, 381) * mm, "end": v(-442, 381) * mm});
            skLineSegment(sketch, "E16.9.3.9", {"start": v(-442, 406.4) * mm, "end": v(-442, 381) * mm});
            skLineSegment(sketch, "E16.0.4.9", {"start": v(-429.3, 406.4) * mm, "end": v(-403.9, 406.4) * mm});
            skLineSegment(sketch, "E16.3.4.9", {"start": v(-429.3, 406.4) * mm, "end": v(-429.3, 381) * mm});
            skLineSegment(sketch, "E16.6.4.9", {"start": v(-429.3, 381) * mm, "end": v(-403.9, 381) * mm});
            skLineSegment(sketch, "E16.9.4.9", {"start": v(-403.9, 406.4) * mm, "end": v(-403.9, 381) * mm});
            skLineSegment(sketch, "E16.0.5.9", {"start": v(-391.2, 406.4) * mm, "end": v(-365.8, 406.4) * mm});
            skLineSegment(sketch, "E16.3.5.9", {"start": v(-391.2, 406.4) * mm, "end": v(-391.2, 381) * mm});
            skLineSegment(sketch, "E16.6.5.9", {"start": v(-391.2, 381) * mm, "end": v(-365.8, 381) * mm});
            skLineSegment(sketch, "E16.9.5.9", {"start": v(-365.8, 406.4) * mm, "end": v(-365.8, 381) * mm});
            skLineSegment(sketch, "E16.0.6.9", {"start": v(-353.1, 406.4) * mm, "end": v(-327.7, 406.4) * mm});
            skLineSegment(sketch, "E16.3.6.9", {"start": v(-353.1, 406.4) * mm, "end": v(-353.1, 381) * mm});
            skLineSegment(sketch, "E16.6.6.9", {"start": v(-353.1, 381) * mm, "end": v(-327.7, 381) * mm});
            skLineSegment(sketch, "E16.9.6.9", {"start": v(-327.7, 406.4) * mm, "end": v(-327.7, 381) * mm});
            skLineSegment(sketch, "E16.0.7.9", {"start": v(-315, 406.4) * mm, "end": v(-289.6, 406.4) * mm});
            skLineSegment(sketch, "E16.3.7.9", {"start": v(-315, 406.4) * mm, "end": v(-315, 381) * mm});
            skLineSegment(sketch, "E16.6.7.9", {"start": v(-315, 381) * mm, "end": v(-289.6, 381) * mm});
            skLineSegment(sketch, "E16.9.7.9", {"start": v(-289.6, 406.4) * mm, "end": v(-289.6, 381) * mm});
            skLineSegment(sketch, "E16.0.8.9", {"start": v(-276.9, 406.4) * mm, "end": v(-251.5, 406.4) * mm});
            skLineSegment(sketch, "E16.3.8.9", {"start": v(-276.9, 406.4) * mm, "end": v(-276.9, 381) * mm});
            skLineSegment(sketch, "E16.6.8.9", {"start": v(-276.9, 381) * mm, "end": v(-251.5, 381) * mm});
            skLineSegment(sketch, "E16.9.8.9", {"start": v(-251.5, 406.4) * mm, "end": v(-251.5, 381) * mm});
            skLineSegment(sketch, "E16.0.9.9", {"start": v(-238.8, 406.4) * mm, "end": v(-213.4, 406.4) * mm});
            skLineSegment(sketch, "E16.3.9.9", {"start": v(-238.8, 406.4) * mm, "end": v(-238.8, 381) * mm});
            skLineSegment(sketch, "E16.6.9.9", {"start": v(-238.8, 381) * mm, "end": v(-213.4, 381) * mm});
            skLineSegment(sketch, "E16.9.9.9", {"start": v(-213.4, 406.4) * mm, "end": v(-213.4, 381) * mm});
            skLineSegment(sketch, "E16.0.10.9", {"start": v(-200.7, 406.4) * mm, "end": v(-175.3, 406.4) * mm});
            skLineSegment(sketch, "E16.3.10.9", {"start": v(-200.7, 406.4) * mm, "end": v(-200.7, 381) * mm});
            skLineSegment(sketch, "E16.6.10.9", {"start": v(-200.7, 381) * mm, "end": v(-175.3, 381) * mm});
            skLineSegment(sketch, "E16.9.10.9", {"start": v(-175.3, 406.4) * mm, "end": v(-175.3, 381) * mm});
            skLineSegment(sketch, "E16.0.11.9", {"start": v(-162.6, 406.4) * mm, "end": v(-137.2, 406.4) * mm});
            skLineSegment(sketch, "E16.3.11.9", {"start": v(-162.6, 406.4) * mm, "end": v(-162.6, 381) * mm});
            skLineSegment(sketch, "E16.6.11.9", {"start": v(-162.6, 381) * mm, "end": v(-137.2, 381) * mm});
            skLineSegment(sketch, "E16.9.11.9", {"start": v(-137.2, 406.4) * mm, "end": v(-137.2, 381) * mm});
            skLineSegment(sketch, "E16.0.12.9", {"start": v(-124.5, 406.4) * mm, "end": v(-99.1, 406.4) * mm});
            skLineSegment(sketch, "E16.3.12.9", {"start": v(-124.5, 406.4) * mm, "end": v(-124.5, 381) * mm});
            skLineSegment(sketch, "E16.6.12.9", {"start": v(-124.5, 381) * mm, "end": v(-99.1, 381) * mm});
            skLineSegment(sketch, "E16.9.12.9", {"start": v(-99.1, 406.4) * mm, "end": v(-99.1, 381) * mm});
            skLineSegment(sketch, "E16.0.13.9", {"start": v(-86.4, 406.4) * mm, "end": v(-61, 406.4) * mm});
            skLineSegment(sketch, "E16.3.13.9", {"start": v(-86.4, 406.4) * mm, "end": v(-86.4, 381) * mm});
            skLineSegment(sketch, "E16.6.13.9", {"start": v(-86.4, 381) * mm, "end": v(-61, 381) * mm});
            skLineSegment(sketch, "E16.9.13.9", {"start": v(-61, 406.4) * mm, "end": v(-61, 381) * mm});
            skLineSegment(sketch, "E16.0.14.9", {"start": v(-48.3, 406.4) * mm, "end": v(-22.9, 406.4) * mm});
            skLineSegment(sketch, "E16.3.14.9", {"start": v(-48.3, 406.4) * mm, "end": v(-48.3, 381) * mm});
            skLineSegment(sketch, "E16.6.14.9", {"start": v(-48.3, 381) * mm, "end": v(-22.9, 381) * mm});
            skLineSegment(sketch, "E16.9.14.9", {"start": v(-22.9, 406.4) * mm, "end": v(-22.9, 381) * mm});
            skLineSegment(sketch, "E16.0.15.9", {"start": v(-10.2, 406.4) * mm, "end": v(15.2, 406.4) * mm});
            skLineSegment(sketch, "E16.3.15.9", {"start": v(-10.2, 406.4) * mm, "end": v(-10.2, 381) * mm});
            skLineSegment(sketch, "E16.6.15.9", {"start": v(-10.2, 381) * mm, "end": v(15.2, 381) * mm});
            skLineSegment(sketch, "E16.9.15.9", {"start": v(15.2, 406.4) * mm, "end": v(15.2, 381) * mm});
            skLineSegment(sketch, "E16.0.16.9", {"start": v(27.9, 406.4) * mm, "end": v(53.3, 406.4) * mm});
            skLineSegment(sketch, "E16.3.16.9", {"start": v(27.9, 406.4) * mm, "end": v(27.9, 381) * mm});
            skLineSegment(sketch, "E16.6.16.9", {"start": v(27.9, 381) * mm, "end": v(53.3, 381) * mm});
            skLineSegment(sketch, "E16.9.16.9", {"start": v(53.3, 406.4) * mm, "end": v(53.3, 381) * mm});
            skLineSegment(sketch, "E16.0.17.9", {"start": v(66, 406.4) * mm, "end": v(91.4, 406.4) * mm});
            skLineSegment(sketch, "E16.3.17.9", {"start": v(66, 406.4) * mm, "end": v(66, 381) * mm});
            skLineSegment(sketch, "E16.6.17.9", {"start": v(66, 381) * mm, "end": v(91.4, 381) * mm});
            skLineSegment(sketch, "E16.9.17.9", {"start": v(91.4, 406.4) * mm, "end": v(91.4, 381) * mm});
            skLineSegment(sketch, "E16.0.18.9", {"start": v(104.1, 406.4) * mm, "end": v(129.5, 406.4) * mm});
            skLineSegment(sketch, "E16.3.18.9", {"start": v(104.1, 406.4) * mm, "end": v(104.1, 381) * mm});
            skLineSegment(sketch, "E16.6.18.9", {"start": v(104.1, 381) * mm, "end": v(129.5, 381) * mm});
            skLineSegment(sketch, "E16.9.18.9", {"start": v(129.5, 406.4) * mm, "end": v(129.5, 381) * mm});
            skLineSegment(sketch, "E16.0.19.9", {"start": v(142.2, 406.4) * mm, "end": v(167.6, 406.4) * mm});
            skLineSegment(sketch, "E16.3.19.9", {"start": v(142.2, 406.4) * mm, "end": v(142.2, 381) * mm});
            skLineSegment(sketch, "E16.6.19.9", {"start": v(142.2, 381) * mm, "end": v(167.6, 381) * mm});
            skLineSegment(sketch, "E16.9.19.9", {"start": v(167.6, 406.4) * mm, "end": v(167.6, 381) * mm});
            skLineSegment(sketch, "E16.0.20.9", {"start": v(180.3, 406.4) * mm, "end": v(205.7, 406.4) * mm});
            skLineSegment(sketch, "E16.3.20.9", {"start": v(180.3, 406.4) * mm, "end": v(180.3, 381) * mm});
            skLineSegment(sketch, "E16.6.20.9", {"start": v(180.3, 381) * mm, "end": v(205.7, 381) * mm});
            skLineSegment(sketch, "E16.9.20.9", {"start": v(205.7, 406.4) * mm, "end": v(205.7, 381) * mm});
            skLineSegment(sketch, "E16.0.21.9", {"start": v(218.4, 406.4) * mm, "end": v(243.8, 406.4) * mm});
            skLineSegment(sketch, "E16.3.21.9", {"start": v(218.4, 406.4) * mm, "end": v(218.4, 381) * mm});
            skLineSegment(sketch, "E16.6.21.9", {"start": v(218.4, 381) * mm, "end": v(243.8, 381) * mm});
            skLineSegment(sketch, "E16.9.21.9", {"start": v(243.8, 406.4) * mm, "end": v(243.8, 381) * mm});
            skLineSegment(sketch, "E16.0.22.9", {"start": v(256.5, 406.4) * mm, "end": v(281.9, 406.4) * mm});
            skLineSegment(sketch, "E16.3.22.9", {"start": v(256.5, 406.4) * mm, "end": v(256.5, 381) * mm});
            skLineSegment(sketch, "E16.6.22.9", {"start": v(256.5, 381) * mm, "end": v(281.9, 381) * mm});
            skLineSegment(sketch, "E16.9.22.9", {"start": v(281.9, 406.4) * mm, "end": v(281.9, 381) * mm});
            skLineSegment(sketch, "E16.0.23.9", {"start": v(294.6, 406.4) * mm, "end": v(320, 406.4) * mm});
            skLineSegment(sketch, "E16.3.23.9", {"start": v(294.6, 406.4) * mm, "end": v(294.6, 381) * mm});
            skLineSegment(sketch, "E16.6.23.9", {"start": v(294.6, 381) * mm, "end": v(320, 381) * mm});
            skLineSegment(sketch, "E16.9.23.9", {"start": v(320, 406.4) * mm, "end": v(320, 381) * mm});
            skLineSegment(sketch, "E17.0.24.0", {"start": v(332.7, 63.5) * mm, "end": v(358.1, 63.5) * mm});
            skLineSegment(sketch, "E17.3.24.0", {"start": v(332.7, 63.5) * mm, "end": v(332.7, 38.1) * mm});
            skLineSegment(sketch, "E17.6.24.0", {"start": v(332.7, 38.1) * mm, "end": v(358.1, 38.1) * mm});
            skLineSegment(sketch, "E17.9.24.0", {"start": v(358.1, 63.5) * mm, "end": v(358.1, 38.1) * mm});
            skLineSegment(sketch, "E17.0.24.1", {"start": v(332.7, 101.6) * mm, "end": v(358.1, 101.6) * mm});
            skLineSegment(sketch, "E17.3.24.1", {"start": v(332.7, 101.6) * mm, "end": v(332.7, 76.2) * mm});
            skLineSegment(sketch, "E17.6.24.1", {"start": v(332.7, 76.2) * mm, "end": v(358.1, 76.2) * mm});
            skLineSegment(sketch, "E17.9.24.1", {"start": v(358.1, 101.6) * mm, "end": v(358.1, 76.2) * mm});
            skLineSegment(sketch, "E17.0.24.2", {"start": v(332.7, 139.7) * mm, "end": v(358.1, 139.7) * mm});
            skLineSegment(sketch, "E17.3.24.2", {"start": v(332.7, 139.7) * mm, "end": v(332.7, 114.3) * mm});
            skLineSegment(sketch, "E17.6.24.2", {"start": v(332.7, 114.3) * mm, "end": v(358.1, 114.3) * mm});
            skLineSegment(sketch, "E17.9.24.2", {"start": v(358.1, 139.7) * mm, "end": v(358.1, 114.3) * mm});
            skLineSegment(sketch, "E17.0.24.3", {"start": v(332.7, 177.8) * mm, "end": v(358.1, 177.8) * mm});
            skLineSegment(sketch, "E17.3.24.3", {"start": v(332.7, 177.8) * mm, "end": v(332.7, 152.4) * mm});
            skLineSegment(sketch, "E17.6.24.3", {"start": v(332.7, 152.4) * mm, "end": v(358.1, 152.4) * mm});
            skLineSegment(sketch, "E17.9.24.3", {"start": v(358.1, 177.8) * mm, "end": v(358.1, 152.4) * mm});
            skLineSegment(sketch, "E17.0.24.4", {"start": v(332.7, 215.9) * mm, "end": v(358.1, 215.9) * mm});
            skLineSegment(sketch, "E17.3.24.4", {"start": v(332.7, 215.9) * mm, "end": v(332.7, 190.5) * mm});
            skLineSegment(sketch, "E17.6.24.4", {"start": v(332.7, 190.5) * mm, "end": v(358.1, 190.5) * mm});
            skLineSegment(sketch, "E17.9.24.4", {"start": v(358.1, 215.9) * mm, "end": v(358.1, 190.5) * mm});
            skLineSegment(sketch, "E17.0.24.5", {"start": v(332.7, 254) * mm, "end": v(358.1, 254) * mm});
            skLineSegment(sketch, "E17.3.24.5", {"start": v(332.7, 254) * mm, "end": v(332.7, 228.6) * mm});
            skLineSegment(sketch, "E17.6.24.5", {"start": v(332.7, 228.6) * mm, "end": v(358.1, 228.6) * mm});
            skLineSegment(sketch, "E17.9.24.5", {"start": v(358.1, 254) * mm, "end": v(358.1, 228.6) * mm});
            skLineSegment(sketch, "E17.0.24.6", {"start": v(332.7, 292.1) * mm, "end": v(358.1, 292.1) * mm});
            skLineSegment(sketch, "E17.3.24.6", {"start": v(332.7, 292.1) * mm, "end": v(332.7, 266.7) * mm});
            skLineSegment(sketch, "E17.6.24.6", {"start": v(332.7, 266.7) * mm, "end": v(358.1, 266.7) * mm});
            skLineSegment(sketch, "E17.9.24.6", {"start": v(358.1, 292.1) * mm, "end": v(358.1, 266.7) * mm});
            skLineSegment(sketch, "E17.0.24.7", {"start": v(332.7, 330.2) * mm, "end": v(358.1, 330.2) * mm});
            skLineSegment(sketch, "E17.3.24.7", {"start": v(332.7, 330.2) * mm, "end": v(332.7, 304.8) * mm});
            skLineSegment(sketch, "E17.6.24.7", {"start": v(332.7, 304.8) * mm, "end": v(358.1, 304.8) * mm});
            skLineSegment(sketch, "E17.9.24.7", {"start": v(358.1, 330.2) * mm, "end": v(358.1, 304.8) * mm});
            skLineSegment(sketch, "E17.0.24.8", {"start": v(332.7, 368.3) * mm, "end": v(358.1, 368.3) * mm});
            skLineSegment(sketch, "E17.3.24.8", {"start": v(332.7, 368.3) * mm, "end": v(332.7, 342.9) * mm});
            skLineSegment(sketch, "E17.6.24.8", {"start": v(332.7, 342.9) * mm, "end": v(358.1, 342.9) * mm});
            skLineSegment(sketch, "E17.9.24.8", {"start": v(358.1, 368.3) * mm, "end": v(358.1, 342.9) * mm});
            skLineSegment(sketch, "E17.0.24.9", {"start": v(332.7, 406.4) * mm, "end": v(358.1, 406.4) * mm});
            skLineSegment(sketch, "E17.3.24.9", {"start": v(332.7, 406.4) * mm, "end": v(332.7, 381) * mm});
            skLineSegment(sketch, "E17.6.24.9", {"start": v(332.7, 381) * mm, "end": v(358.1, 381) * mm});
            skLineSegment(sketch, "E17.9.24.9", {"start": v(358.1, 406.4) * mm, "end": v(358.1, 381) * mm});
            skLineSegment(sketch, "E18.0.0.10", {"start": v(-581.7, 444.5) * mm, "end": v(-556.3, 444.5) * mm});
            skLineSegment(sketch, "E18.3.0.10", {"start": v(-581.7, 444.5) * mm, "end": v(-581.7, 419.1) * mm});
            skLineSegment(sketch, "E18.6.0.10", {"start": v(-581.7, 419.1) * mm, "end": v(-556.3, 419.1) * mm});
            skLineSegment(sketch, "E18.9.0.10", {"start": v(-556.3, 444.5) * mm, "end": v(-556.3, 419.1) * mm});
            skLineSegment(sketch, "E18.0.0.11", {"start": v(-581.7, 482.6) * mm, "end": v(-556.3, 482.6) * mm});
            skLineSegment(sketch, "E18.3.0.11", {"start": v(-581.7, 482.6) * mm, "end": v(-581.7, 457.2) * mm});
            skLineSegment(sketch, "E18.6.0.11", {"start": v(-581.7, 457.2) * mm, "end": v(-556.3, 457.2) * mm});
            skLineSegment(sketch, "E18.9.0.11", {"start": v(-556.3, 482.6) * mm, "end": v(-556.3, 457.2) * mm});
            skLineSegment(sketch, "E18.0.1.10", {"start": v(-543.6, 444.5) * mm, "end": v(-518.2, 444.5) * mm});
            skLineSegment(sketch, "E18.3.1.10", {"start": v(-543.6, 444.5) * mm, "end": v(-543.6, 419.1) * mm});
            skLineSegment(sketch, "E18.6.1.10", {"start": v(-543.6, 419.1) * mm, "end": v(-518.2, 419.1) * mm});
            skLineSegment(sketch, "E18.9.1.10", {"start": v(-518.2, 444.5) * mm, "end": v(-518.2, 419.1) * mm});
            skLineSegment(sketch, "E18.0.1.11", {"start": v(-543.6, 482.6) * mm, "end": v(-518.2, 482.6) * mm});
            skLineSegment(sketch, "E18.3.1.11", {"start": v(-543.6, 482.6) * mm, "end": v(-543.6, 457.2) * mm});
            skLineSegment(sketch, "E18.6.1.11", {"start": v(-543.6, 457.2) * mm, "end": v(-518.2, 457.2) * mm});
            skLineSegment(sketch, "E18.9.1.11", {"start": v(-518.2, 482.6) * mm, "end": v(-518.2, 457.2) * mm});
            skLineSegment(sketch, "E18.0.2.10", {"start": v(-505.5, 444.5) * mm, "end": v(-480.1, 444.5) * mm});
            skLineSegment(sketch, "E18.3.2.10", {"start": v(-505.5, 444.5) * mm, "end": v(-505.5, 419.1) * mm});
            skLineSegment(sketch, "E18.6.2.10", {"start": v(-505.5, 419.1) * mm, "end": v(-480.1, 419.1) * mm});
            skLineSegment(sketch, "E18.9.2.10", {"start": v(-480.1, 444.5) * mm, "end": v(-480.1, 419.1) * mm});
            skLineSegment(sketch, "E18.0.2.11", {"start": v(-505.5, 482.6) * mm, "end": v(-480.1, 482.6) * mm});
            skLineSegment(sketch, "E18.3.2.11", {"start": v(-505.5, 482.6) * mm, "end": v(-505.5, 457.2) * mm});
            skLineSegment(sketch, "E18.6.2.11", {"start": v(-505.5, 457.2) * mm, "end": v(-480.1, 457.2) * mm});
            skLineSegment(sketch, "E18.9.2.11", {"start": v(-480.1, 482.6) * mm, "end": v(-480.1, 457.2) * mm});
            skLineSegment(sketch, "E18.0.3.10", {"start": v(-467.4, 444.5) * mm, "end": v(-442, 444.5) * mm});
            skLineSegment(sketch, "E18.3.3.10", {"start": v(-467.4, 444.5) * mm, "end": v(-467.4, 419.1) * mm});
            skLineSegment(sketch, "E18.6.3.10", {"start": v(-467.4, 419.1) * mm, "end": v(-442, 419.1) * mm});
            skLineSegment(sketch, "E18.9.3.10", {"start": v(-442, 444.5) * mm, "end": v(-442, 419.1) * mm});
            skLineSegment(sketch, "E18.0.3.11", {"start": v(-467.4, 482.6) * mm, "end": v(-442, 482.6) * mm});
            skLineSegment(sketch, "E18.3.3.11", {"start": v(-467.4, 482.6) * mm, "end": v(-467.4, 457.2) * mm});
            skLineSegment(sketch, "E18.6.3.11", {"start": v(-467.4, 457.2) * mm, "end": v(-442, 457.2) * mm});
            skLineSegment(sketch, "E18.9.3.11", {"start": v(-442, 482.6) * mm, "end": v(-442, 457.2) * mm});
            skLineSegment(sketch, "E18.0.4.10", {"start": v(-429.3, 444.5) * mm, "end": v(-403.9, 444.5) * mm});
            skLineSegment(sketch, "E18.3.4.10", {"start": v(-429.3, 444.5) * mm, "end": v(-429.3, 419.1) * mm});
            skLineSegment(sketch, "E18.6.4.10", {"start": v(-429.3, 419.1) * mm, "end": v(-403.9, 419.1) * mm});
            skLineSegment(sketch, "E18.9.4.10", {"start": v(-403.9, 444.5) * mm, "end": v(-403.9, 419.1) * mm});
            skLineSegment(sketch, "E18.0.4.11", {"start": v(-429.3, 482.6) * mm, "end": v(-403.9, 482.6) * mm});
            skLineSegment(sketch, "E18.3.4.11", {"start": v(-429.3, 482.6) * mm, "end": v(-429.3, 457.2) * mm});
            skLineSegment(sketch, "E18.6.4.11", {"start": v(-429.3, 457.2) * mm, "end": v(-403.9, 457.2) * mm});
            skLineSegment(sketch, "E18.9.4.11", {"start": v(-403.9, 482.6) * mm, "end": v(-403.9, 457.2) * mm});
            skLineSegment(sketch, "E18.0.5.10", {"start": v(-391.2, 444.5) * mm, "end": v(-365.8, 444.5) * mm});
            skLineSegment(sketch, "E18.3.5.10", {"start": v(-391.2, 444.5) * mm, "end": v(-391.2, 419.1) * mm});
            skLineSegment(sketch, "E18.6.5.10", {"start": v(-391.2, 419.1) * mm, "end": v(-365.8, 419.1) * mm});
            skLineSegment(sketch, "E18.9.5.10", {"start": v(-365.8, 444.5) * mm, "end": v(-365.8, 419.1) * mm});
            skLineSegment(sketch, "E18.0.5.11", {"start": v(-391.2, 482.6) * mm, "end": v(-365.8, 482.6) * mm});
            skLineSegment(sketch, "E18.3.5.11", {"start": v(-391.2, 482.6) * mm, "end": v(-391.2, 457.2) * mm});
            skLineSegment(sketch, "E18.6.5.11", {"start": v(-391.2, 457.2) * mm, "end": v(-365.8, 457.2) * mm});
            skLineSegment(sketch, "E18.9.5.11", {"start": v(-365.8, 482.6) * mm, "end": v(-365.8, 457.2) * mm});
            skLineSegment(sketch, "E18.0.6.10", {"start": v(-353.1, 444.5) * mm, "end": v(-327.7, 444.5) * mm});
            skLineSegment(sketch, "E18.3.6.10", {"start": v(-353.1, 444.5) * mm, "end": v(-353.1, 419.1) * mm});
            skLineSegment(sketch, "E18.6.6.10", {"start": v(-353.1, 419.1) * mm, "end": v(-327.7, 419.1) * mm});
            skLineSegment(sketch, "E18.9.6.10", {"start": v(-327.7, 444.5) * mm, "end": v(-327.7, 419.1) * mm});
            skLineSegment(sketch, "E18.0.6.11", {"start": v(-353.1, 482.6) * mm, "end": v(-327.7, 482.6) * mm});
            skLineSegment(sketch, "E18.3.6.11", {"start": v(-353.1, 482.6) * mm, "end": v(-353.1, 457.2) * mm});
            skLineSegment(sketch, "E18.6.6.11", {"start": v(-353.1, 457.2) * mm, "end": v(-327.7, 457.2) * mm});
            skLineSegment(sketch, "E18.9.6.11", {"start": v(-327.7, 482.6) * mm, "end": v(-327.7, 457.2) * mm});
            skLineSegment(sketch, "E18.0.7.10", {"start": v(-315, 444.5) * mm, "end": v(-289.6, 444.5) * mm});
            skLineSegment(sketch, "E18.3.7.10", {"start": v(-315, 444.5) * mm, "end": v(-315, 419.1) * mm});
            skLineSegment(sketch, "E18.6.7.10", {"start": v(-315, 419.1) * mm, "end": v(-289.6, 419.1) * mm});
            skLineSegment(sketch, "E18.9.7.10", {"start": v(-289.6, 444.5) * mm, "end": v(-289.6, 419.1) * mm});
            skLineSegment(sketch, "E18.0.7.11", {"start": v(-315, 482.6) * mm, "end": v(-289.6, 482.6) * mm});
            skLineSegment(sketch, "E18.3.7.11", {"start": v(-315, 482.6) * mm, "end": v(-315, 457.2) * mm});
            skLineSegment(sketch, "E18.6.7.11", {"start": v(-315, 457.2) * mm, "end": v(-289.6, 457.2) * mm});
            skLineSegment(sketch, "E18.9.7.11", {"start": v(-289.6, 482.6) * mm, "end": v(-289.6, 457.2) * mm});
            skLineSegment(sketch, "E18.0.8.10", {"start": v(-276.9, 444.5) * mm, "end": v(-251.5, 444.5) * mm});
            skLineSegment(sketch, "E18.3.8.10", {"start": v(-276.9, 444.5) * mm, "end": v(-276.9, 419.1) * mm});
            skLineSegment(sketch, "E18.6.8.10", {"start": v(-276.9, 419.1) * mm, "end": v(-251.5, 419.1) * mm});
            skLineSegment(sketch, "E18.9.8.10", {"start": v(-251.5, 444.5) * mm, "end": v(-251.5, 419.1) * mm});
            skLineSegment(sketch, "E18.0.8.11", {"start": v(-276.9, 482.6) * mm, "end": v(-251.5, 482.6) * mm});
            skLineSegment(sketch, "E18.3.8.11", {"start": v(-276.9, 482.6) * mm, "end": v(-276.9, 457.2) * mm});
            skLineSegment(sketch, "E18.6.8.11", {"start": v(-276.9, 457.2) * mm, "end": v(-251.5, 457.2) * mm});
            skLineSegment(sketch, "E18.9.8.11", {"start": v(-251.5, 482.6) * mm, "end": v(-251.5, 457.2) * mm});
            skLineSegment(sketch, "E18.0.9.10", {"start": v(-238.8, 444.5) * mm, "end": v(-213.4, 444.5) * mm});
            skLineSegment(sketch, "E18.3.9.10", {"start": v(-238.8, 444.5) * mm, "end": v(-238.8, 419.1) * mm});
            skLineSegment(sketch, "E18.6.9.10", {"start": v(-238.8, 419.1) * mm, "end": v(-213.4, 419.1) * mm});
            skLineSegment(sketch, "E18.9.9.10", {"start": v(-213.4, 444.5) * mm, "end": v(-213.4, 419.1) * mm});
            skLineSegment(sketch, "E18.0.9.11", {"start": v(-238.8, 482.6) * mm, "end": v(-213.4, 482.6) * mm});
            skLineSegment(sketch, "E18.3.9.11", {"start": v(-238.8, 482.6) * mm, "end": v(-238.8, 457.2) * mm});
            skLineSegment(sketch, "E18.6.9.11", {"start": v(-238.8, 457.2) * mm, "end": v(-213.4, 457.2) * mm});
            skLineSegment(sketch, "E18.9.9.11", {"start": v(-213.4, 482.6) * mm, "end": v(-213.4, 457.2) * mm});
            skLineSegment(sketch, "E18.0.10.10", {"start": v(-200.7, 444.5) * mm, "end": v(-175.3, 444.5) * mm});
            skLineSegment(sketch, "E18.3.10.10", {"start": v(-200.7, 444.5) * mm, "end": v(-200.7, 419.1) * mm});
            skLineSegment(sketch, "E18.6.10.10", {"start": v(-200.7, 419.1) * mm, "end": v(-175.3, 419.1) * mm});
            skLineSegment(sketch, "E18.9.10.10", {"start": v(-175.3, 444.5) * mm, "end": v(-175.3, 419.1) * mm});
            skLineSegment(sketch, "E18.0.10.11", {"start": v(-200.7, 482.6) * mm, "end": v(-175.3, 482.6) * mm});
            skLineSegment(sketch, "E18.3.10.11", {"start": v(-200.7, 482.6) * mm, "end": v(-200.7, 457.2) * mm});
            skLineSegment(sketch, "E18.6.10.11", {"start": v(-200.7, 457.2) * mm, "end": v(-175.3, 457.2) * mm});
            skLineSegment(sketch, "E18.9.10.11", {"start": v(-175.3, 482.6) * mm, "end": v(-175.3, 457.2) * mm});
            skLineSegment(sketch, "E18.0.11.10", {"start": v(-162.6, 444.5) * mm, "end": v(-137.2, 444.5) * mm});
            skLineSegment(sketch, "E18.3.11.10", {"start": v(-162.6, 444.5) * mm, "end": v(-162.6, 419.1) * mm});
            skLineSegment(sketch, "E18.6.11.10", {"start": v(-162.6, 419.1) * mm, "end": v(-137.2, 419.1) * mm});
            skLineSegment(sketch, "E18.9.11.10", {"start": v(-137.2, 444.5) * mm, "end": v(-137.2, 419.1) * mm});
            skLineSegment(sketch, "E18.0.11.11", {"start": v(-162.6, 482.6) * mm, "end": v(-137.2, 482.6) * mm});
            skLineSegment(sketch, "E18.3.11.11", {"start": v(-162.6, 482.6) * mm, "end": v(-162.6, 457.2) * mm});
            skLineSegment(sketch, "E18.6.11.11", {"start": v(-162.6, 457.2) * mm, "end": v(-137.2, 457.2) * mm});
            skLineSegment(sketch, "E18.9.11.11", {"start": v(-137.2, 482.6) * mm, "end": v(-137.2, 457.2) * mm});
            skLineSegment(sketch, "E18.0.12.10", {"start": v(-124.5, 444.5) * mm, "end": v(-99.1, 444.5) * mm});
            skLineSegment(sketch, "E18.3.12.10", {"start": v(-124.5, 444.5) * mm, "end": v(-124.5, 419.1) * mm});
            skLineSegment(sketch, "E18.6.12.10", {"start": v(-124.5, 419.1) * mm, "end": v(-99.1, 419.1) * mm});
            skLineSegment(sketch, "E18.9.12.10", {"start": v(-99.1, 444.5) * mm, "end": v(-99.1, 419.1) * mm});
            skLineSegment(sketch, "E18.0.12.11", {"start": v(-124.5, 482.6) * mm, "end": v(-99.1, 482.6) * mm});
            skLineSegment(sketch, "E18.3.12.11", {"start": v(-124.5, 482.6) * mm, "end": v(-124.5, 457.2) * mm});
            skLineSegment(sketch, "E18.6.12.11", {"start": v(-124.5, 457.2) * mm, "end": v(-99.1, 457.2) * mm});
            skLineSegment(sketch, "E18.9.12.11", {"start": v(-99.1, 482.6) * mm, "end": v(-99.1, 457.2) * mm});
            skLineSegment(sketch, "E18.0.13.10", {"start": v(-86.4, 444.5) * mm, "end": v(-61, 444.5) * mm});
            skLineSegment(sketch, "E18.3.13.10", {"start": v(-86.4, 444.5) * mm, "end": v(-86.4, 419.1) * mm});
            skLineSegment(sketch, "E18.6.13.10", {"start": v(-86.4, 419.1) * mm, "end": v(-61, 419.1) * mm});
            skLineSegment(sketch, "E18.9.13.10", {"start": v(-61, 444.5) * mm, "end": v(-61, 419.1) * mm});
            skLineSegment(sketch, "E18.0.13.11", {"start": v(-86.4, 482.6) * mm, "end": v(-61, 482.6) * mm});
            skLineSegment(sketch, "E18.3.13.11", {"start": v(-86.4, 482.6) * mm, "end": v(-86.4, 457.2) * mm});
            skLineSegment(sketch, "E18.6.13.11", {"start": v(-86.4, 457.2) * mm, "end": v(-61, 457.2) * mm});
            skLineSegment(sketch, "E18.9.13.11", {"start": v(-61, 482.6) * mm, "end": v(-61, 457.2) * mm});
            skLineSegment(sketch, "E18.0.14.10", {"start": v(-48.3, 444.5) * mm, "end": v(-22.9, 444.5) * mm});
            skLineSegment(sketch, "E18.3.14.10", {"start": v(-48.3, 444.5) * mm, "end": v(-48.3, 419.1) * mm});
            skLineSegment(sketch, "E18.6.14.10", {"start": v(-48.3, 419.1) * mm, "end": v(-22.9, 419.1) * mm});
            skLineSegment(sketch, "E18.9.14.10", {"start": v(-22.9, 444.5) * mm, "end": v(-22.9, 419.1) * mm});
            skLineSegment(sketch, "E18.0.14.11", {"start": v(-48.3, 482.6) * mm, "end": v(-22.9, 482.6) * mm});
            skLineSegment(sketch, "E18.3.14.11", {"start": v(-48.3, 482.6) * mm, "end": v(-48.3, 457.2) * mm});
            skLineSegment(sketch, "E18.6.14.11", {"start": v(-48.3, 457.2) * mm, "end": v(-22.9, 457.2) * mm});
            skLineSegment(sketch, "E18.9.14.11", {"start": v(-22.9, 482.6) * mm, "end": v(-22.9, 457.2) * mm});
            skLineSegment(sketch, "E18.0.15.10", {"start": v(-10.2, 444.5) * mm, "end": v(15.2, 444.5) * mm});
            skLineSegment(sketch, "E18.3.15.10", {"start": v(-10.2, 444.5) * mm, "end": v(-10.2, 419.1) * mm});
            skLineSegment(sketch, "E18.6.15.10", {"start": v(-10.2, 419.1) * mm, "end": v(15.2, 419.1) * mm});
            skLineSegment(sketch, "E18.9.15.10", {"start": v(15.2, 444.5) * mm, "end": v(15.2, 419.1) * mm});
            skLineSegment(sketch, "E18.0.15.11", {"start": v(-10.2, 482.6) * mm, "end": v(15.2, 482.6) * mm});
            skLineSegment(sketch, "E18.3.15.11", {"start": v(-10.2, 482.6) * mm, "end": v(-10.2, 457.2) * mm});
            skLineSegment(sketch, "E18.6.15.11", {"start": v(-10.2, 457.2) * mm, "end": v(15.2, 457.2) * mm});
            skLineSegment(sketch, "E18.9.15.11", {"start": v(15.2, 482.6) * mm, "end": v(15.2, 457.2) * mm});
            skLineSegment(sketch, "E18.0.16.10", {"start": v(27.9, 444.5) * mm, "end": v(53.3, 444.5) * mm});
            skLineSegment(sketch, "E18.3.16.10", {"start": v(27.9, 444.5) * mm, "end": v(27.9, 419.1) * mm});
            skLineSegment(sketch, "E18.6.16.10", {"start": v(27.9, 419.1) * mm, "end": v(53.3, 419.1) * mm});
            skLineSegment(sketch, "E18.9.16.10", {"start": v(53.3, 444.5) * mm, "end": v(53.3, 419.1) * mm});
            skLineSegment(sketch, "E18.0.16.11", {"start": v(27.9, 482.6) * mm, "end": v(53.3, 482.6) * mm});
            skLineSegment(sketch, "E18.3.16.11", {"start": v(27.9, 482.6) * mm, "end": v(27.9, 457.2) * mm});
            skLineSegment(sketch, "E18.6.16.11", {"start": v(27.9, 457.2) * mm, "end": v(53.3, 457.2) * mm});
            skLineSegment(sketch, "E18.9.16.11", {"start": v(53.3, 482.6) * mm, "end": v(53.3, 457.2) * mm});
            skLineSegment(sketch, "E18.0.17.10", {"start": v(66, 444.5) * mm, "end": v(91.4, 444.5) * mm});
            skLineSegment(sketch, "E18.3.17.10", {"start": v(66, 444.5) * mm, "end": v(66, 419.1) * mm});
            skLineSegment(sketch, "E18.6.17.10", {"start": v(66, 419.1) * mm, "end": v(91.4, 419.1) * mm});
            skLineSegment(sketch, "E18.9.17.10", {"start": v(91.4, 444.5) * mm, "end": v(91.4, 419.1) * mm});
            skLineSegment(sketch, "E18.0.17.11", {"start": v(66, 482.6) * mm, "end": v(91.4, 482.6) * mm});
            skLineSegment(sketch, "E18.3.17.11", {"start": v(66, 482.6) * mm, "end": v(66, 457.2) * mm});
            skLineSegment(sketch, "E18.6.17.11", {"start": v(66, 457.2) * mm, "end": v(91.4, 457.2) * mm});
            skLineSegment(sketch, "E18.9.17.11", {"start": v(91.4, 482.6) * mm, "end": v(91.4, 457.2) * mm});
            skLineSegment(sketch, "E18.0.18.10", {"start": v(104.1, 444.5) * mm, "end": v(129.5, 444.5) * mm});
            skLineSegment(sketch, "E18.3.18.10", {"start": v(104.1, 444.5) * mm, "end": v(104.1, 419.1) * mm});
            skLineSegment(sketch, "E18.6.18.10", {"start": v(104.1, 419.1) * mm, "end": v(129.5, 419.1) * mm});
            skLineSegment(sketch, "E18.9.18.10", {"start": v(129.5, 444.5) * mm, "end": v(129.5, 419.1) * mm});
            skLineSegment(sketch, "E18.0.18.11", {"start": v(104.1, 482.6) * mm, "end": v(129.5, 482.6) * mm});
            skLineSegment(sketch, "E18.3.18.11", {"start": v(104.1, 482.6) * mm, "end": v(104.1, 457.2) * mm});
            skLineSegment(sketch, "E18.6.18.11", {"start": v(104.1, 457.2) * mm, "end": v(129.5, 457.2) * mm});
            skLineSegment(sketch, "E18.9.18.11", {"start": v(129.5, 482.6) * mm, "end": v(129.5, 457.2) * mm});
            skLineSegment(sketch, "E18.0.19.10", {"start": v(142.2, 444.5) * mm, "end": v(167.6, 444.5) * mm});
            skLineSegment(sketch, "E18.3.19.10", {"start": v(142.2, 444.5) * mm, "end": v(142.2, 419.1) * mm});
            skLineSegment(sketch, "E18.6.19.10", {"start": v(142.2, 419.1) * mm, "end": v(167.6, 419.1) * mm});
            skLineSegment(sketch, "E18.9.19.10", {"start": v(167.6, 444.5) * mm, "end": v(167.6, 419.1) * mm});
            skLineSegment(sketch, "E18.0.19.11", {"start": v(142.2, 482.6) * mm, "end": v(167.6, 482.6) * mm});
            skLineSegment(sketch, "E18.3.19.11", {"start": v(142.2, 482.6) * mm, "end": v(142.2, 457.2) * mm});
            skLineSegment(sketch, "E18.6.19.11", {"start": v(142.2, 457.2) * mm, "end": v(167.6, 457.2) * mm});
            skLineSegment(sketch, "E18.9.19.11", {"start": v(167.6, 482.6) * mm, "end": v(167.6, 457.2) * mm});
            skLineSegment(sketch, "E18.0.20.10", {"start": v(180.3, 444.5) * mm, "end": v(205.7, 444.5) * mm});
            skLineSegment(sketch, "E18.3.20.10", {"start": v(180.3, 444.5) * mm, "end": v(180.3, 419.1) * mm});
            skLineSegment(sketch, "E18.6.20.10", {"start": v(180.3, 419.1) * mm, "end": v(205.7, 419.1) * mm});
            skLineSegment(sketch, "E18.9.20.10", {"start": v(205.7, 444.5) * mm, "end": v(205.7, 419.1) * mm});
            skLineSegment(sketch, "E18.0.20.11", {"start": v(180.3, 482.6) * mm, "end": v(205.7, 482.6) * mm});
            skLineSegment(sketch, "E18.3.20.11", {"start": v(180.3, 482.6) * mm, "end": v(180.3, 457.2) * mm});
            skLineSegment(sketch, "E18.6.20.11", {"start": v(180.3, 457.2) * mm, "end": v(205.7, 457.2) * mm});
            skLineSegment(sketch, "E18.9.20.11", {"start": v(205.7, 482.6) * mm, "end": v(205.7, 457.2) * mm});
            skLineSegment(sketch, "E18.0.21.10", {"start": v(218.4, 444.5) * mm, "end": v(243.8, 444.5) * mm});
            skLineSegment(sketch, "E18.3.21.10", {"start": v(218.4, 444.5) * mm, "end": v(218.4, 419.1) * mm});
            skLineSegment(sketch, "E18.6.21.10", {"start": v(218.4, 419.1) * mm, "end": v(243.8, 419.1) * mm});
            skLineSegment(sketch, "E18.9.21.10", {"start": v(243.8, 444.5) * mm, "end": v(243.8, 419.1) * mm});
            skLineSegment(sketch, "E18.0.21.11", {"start": v(218.4, 482.6) * mm, "end": v(243.8, 482.6) * mm});
            skLineSegment(sketch, "E18.3.21.11", {"start": v(218.4, 482.6) * mm, "end": v(218.4, 457.2) * mm});
            skLineSegment(sketch, "E18.6.21.11", {"start": v(218.4, 457.2) * mm, "end": v(243.8, 457.2) * mm});
            skLineSegment(sketch, "E18.9.21.11", {"start": v(243.8, 482.6) * mm, "end": v(243.8, 457.2) * mm});
            skLineSegment(sketch, "E18.0.22.10", {"start": v(256.5, 444.5) * mm, "end": v(281.9, 444.5) * mm});
            skLineSegment(sketch, "E18.3.22.10", {"start": v(256.5, 444.5) * mm, "end": v(256.5, 419.1) * mm});
            skLineSegment(sketch, "E18.6.22.10", {"start": v(256.5, 419.1) * mm, "end": v(281.9, 419.1) * mm});
            skLineSegment(sketch, "E18.9.22.10", {"start": v(281.9, 444.5) * mm, "end": v(281.9, 419.1) * mm});
            skLineSegment(sketch, "E18.0.22.11", {"start": v(256.5, 482.6) * mm, "end": v(281.9, 482.6) * mm});
            skLineSegment(sketch, "E18.3.22.11", {"start": v(256.5, 482.6) * mm, "end": v(256.5, 457.2) * mm});
            skLineSegment(sketch, "E18.6.22.11", {"start": v(256.5, 457.2) * mm, "end": v(281.9, 457.2) * mm});
            skLineSegment(sketch, "E18.9.22.11", {"start": v(281.9, 482.6) * mm, "end": v(281.9, 457.2) * mm});
            skLineSegment(sketch, "E18.0.23.10", {"start": v(294.6, 444.5) * mm, "end": v(320, 444.5) * mm});
            skLineSegment(sketch, "E18.3.23.10", {"start": v(294.6, 444.5) * mm, "end": v(294.6, 419.1) * mm});
            skLineSegment(sketch, "E18.6.23.10", {"start": v(294.6, 419.1) * mm, "end": v(320, 419.1) * mm});
            skLineSegment(sketch, "E18.9.23.10", {"start": v(320, 444.5) * mm, "end": v(320, 419.1) * mm});
            skLineSegment(sketch, "E18.0.23.11", {"start": v(294.6, 482.6) * mm, "end": v(320, 482.6) * mm});
            skLineSegment(sketch, "E18.3.23.11", {"start": v(294.6, 482.6) * mm, "end": v(294.6, 457.2) * mm});
            skLineSegment(sketch, "E18.6.23.11", {"start": v(294.6, 457.2) * mm, "end": v(320, 457.2) * mm});
            skLineSegment(sketch, "E18.9.23.11", {"start": v(320, 482.6) * mm, "end": v(320, 457.2) * mm});
            skLineSegment(sketch, "E18.0.24.10", {"start": v(332.7, 444.5) * mm, "end": v(358.1, 444.5) * mm});
            skLineSegment(sketch, "E18.3.24.10", {"start": v(332.7, 444.5) * mm, "end": v(332.7, 419.1) * mm});
            skLineSegment(sketch, "E18.6.24.10", {"start": v(332.7, 419.1) * mm, "end": v(358.1, 419.1) * mm});
            skLineSegment(sketch, "E18.9.24.10", {"start": v(358.1, 444.5) * mm, "end": v(358.1, 419.1) * mm});
            skLineSegment(sketch, "E18.0.24.11", {"start": v(332.7, 482.6) * mm, "end": v(358.1, 482.6) * mm});
            skLineSegment(sketch, "E18.3.24.11", {"start": v(332.7, 482.6) * mm, "end": v(332.7, 457.2) * mm});
            skLineSegment(sketch, "E18.6.24.11", {"start": v(332.7, 457.2) * mm, "end": v(358.1, 457.2) * mm});
            skLineSegment(sketch, "E18.9.24.11", {"start": v(358.1, 482.6) * mm, "end": v(358.1, 457.2) * mm});
            skLineSegment(sketch, "E19.0.25.0", {"start": v(370.8, 63.5) * mm, "end": v(396.2, 63.5) * mm});
            skLineSegment(sketch, "E19.3.25.0", {"start": v(370.8, 63.5) * mm, "end": v(370.8, 38.1) * mm});
            skLineSegment(sketch, "E19.6.25.0", {"start": v(370.8, 38.1) * mm, "end": v(396.2, 38.1) * mm});
            skLineSegment(sketch, "E19.9.25.0", {"start": v(396.2, 63.5) * mm, "end": v(396.2, 38.1) * mm});
            skLineSegment(sketch, "E19.0.25.1", {"start": v(370.8, 101.6) * mm, "end": v(396.2, 101.6) * mm});
            skLineSegment(sketch, "E19.3.25.1", {"start": v(370.8, 101.6) * mm, "end": v(370.8, 76.2) * mm});
            skLineSegment(sketch, "E19.6.25.1", {"start": v(370.8, 76.2) * mm, "end": v(396.2, 76.2) * mm});
            skLineSegment(sketch, "E19.9.25.1", {"start": v(396.2, 101.6) * mm, "end": v(396.2, 76.2) * mm});
            skLineSegment(sketch, "E19.0.25.2", {"start": v(370.8, 139.7) * mm, "end": v(396.2, 139.7) * mm});
            skLineSegment(sketch, "E19.3.25.2", {"start": v(370.8, 139.7) * mm, "end": v(370.8, 114.3) * mm});
            skLineSegment(sketch, "E19.6.25.2", {"start": v(370.8, 114.3) * mm, "end": v(396.2, 114.3) * mm});
            skLineSegment(sketch, "E19.9.25.2", {"start": v(396.2, 139.7) * mm, "end": v(396.2, 114.3) * mm});
            skLineSegment(sketch, "E19.0.25.3", {"start": v(370.8, 177.8) * mm, "end": v(396.2, 177.8) * mm});
            skLineSegment(sketch, "E19.3.25.3", {"start": v(370.8, 177.8) * mm, "end": v(370.8, 152.4) * mm});
            skLineSegment(sketch, "E19.6.25.3", {"start": v(370.8, 152.4) * mm, "end": v(396.2, 152.4) * mm});
            skLineSegment(sketch, "E19.9.25.3", {"start": v(396.2, 177.8) * mm, "end": v(396.2, 152.4) * mm});
            skLineSegment(sketch, "E19.0.25.4", {"start": v(370.8, 215.9) * mm, "end": v(396.2, 215.9) * mm});
            skLineSegment(sketch, "E19.3.25.4", {"start": v(370.8, 215.9) * mm, "end": v(370.8, 190.5) * mm});
            skLineSegment(sketch, "E19.6.25.4", {"start": v(370.8, 190.5) * mm, "end": v(396.2, 190.5) * mm});
            skLineSegment(sketch, "E19.9.25.4", {"start": v(396.2, 215.9) * mm, "end": v(396.2, 190.5) * mm});
            skLineSegment(sketch, "E19.0.25.5", {"start": v(370.8, 254) * mm, "end": v(396.2, 254) * mm});
            skLineSegment(sketch, "E19.3.25.5", {"start": v(370.8, 254) * mm, "end": v(370.8, 228.6) * mm});
            skLineSegment(sketch, "E19.6.25.5", {"start": v(370.8, 228.6) * mm, "end": v(396.2, 228.6) * mm});
            skLineSegment(sketch, "E19.9.25.5", {"start": v(396.2, 254) * mm, "end": v(396.2, 228.6) * mm});
            skLineSegment(sketch, "E19.0.25.6", {"start": v(370.8, 292.1) * mm, "end": v(396.2, 292.1) * mm});
            skLineSegment(sketch, "E19.3.25.6", {"start": v(370.8, 292.1) * mm, "end": v(370.8, 266.7) * mm});
            skLineSegment(sketch, "E19.6.25.6", {"start": v(370.8, 266.7) * mm, "end": v(396.2, 266.7) * mm});
            skLineSegment(sketch, "E19.9.25.6", {"start": v(396.2, 292.1) * mm, "end": v(396.2, 266.7) * mm});
            skLineSegment(sketch, "E19.0.25.7", {"start": v(370.8, 330.2) * mm, "end": v(396.2, 330.2) * mm});
            skLineSegment(sketch, "E19.3.25.7", {"start": v(370.8, 330.2) * mm, "end": v(370.8, 304.8) * mm});
            skLineSegment(sketch, "E19.6.25.7", {"start": v(370.8, 304.8) * mm, "end": v(396.2, 304.8) * mm});
            skLineSegment(sketch, "E19.9.25.7", {"start": v(396.2, 330.2) * mm, "end": v(396.2, 304.8) * mm});
            skLineSegment(sketch, "E19.0.25.8", {"start": v(370.8, 368.3) * mm, "end": v(396.2, 368.3) * mm});
            skLineSegment(sketch, "E19.3.25.8", {"start": v(370.8, 368.3) * mm, "end": v(370.8, 342.9) * mm});
            skLineSegment(sketch, "E19.6.25.8", {"start": v(370.8, 342.9) * mm, "end": v(396.2, 342.9) * mm});
            skLineSegment(sketch, "E19.9.25.8", {"start": v(396.2, 368.3) * mm, "end": v(396.2, 342.9) * mm});
            skLineSegment(sketch, "E19.0.25.9", {"start": v(370.8, 406.4) * mm, "end": v(396.2, 406.4) * mm});
            skLineSegment(sketch, "E19.3.25.9", {"start": v(370.8, 406.4) * mm, "end": v(370.8, 381) * mm});
            skLineSegment(sketch, "E19.6.25.9", {"start": v(370.8, 381) * mm, "end": v(396.2, 381) * mm});
            skLineSegment(sketch, "E19.9.25.9", {"start": v(396.2, 406.4) * mm, "end": v(396.2, 381) * mm});
            skLineSegment(sketch, "E19.0.25.10", {"start": v(370.8, 444.5) * mm, "end": v(396.2, 444.5) * mm});
            skLineSegment(sketch, "E19.3.25.10", {"start": v(370.8, 444.5) * mm, "end": v(370.8, 419.1) * mm});
            skLineSegment(sketch, "E19.6.25.10", {"start": v(370.8, 419.1) * mm, "end": v(396.2, 419.1) * mm});
            skLineSegment(sketch, "E19.9.25.10", {"start": v(396.2, 444.5) * mm, "end": v(396.2, 419.1) * mm});
            skLineSegment(sketch, "E19.0.25.11", {"start": v(370.8, 482.6) * mm, "end": v(396.2, 482.6) * mm});
            skLineSegment(sketch, "E19.3.25.11", {"start": v(370.8, 482.6) * mm, "end": v(370.8, 457.2) * mm});
            skLineSegment(sketch, "E19.6.25.11", {"start": v(370.8, 457.2) * mm, "end": v(396.2, 457.2) * mm});
            skLineSegment(sketch, "E19.9.25.11", {"start": v(396.2, 482.6) * mm, "end": v(396.2, 457.2) * mm});
            skLineSegment(sketch, "E19.0.26.0", {"start": v(408.9, 63.5) * mm, "end": v(434.3, 63.5) * mm});
            skLineSegment(sketch, "E19.3.26.0", {"start": v(408.9, 63.5) * mm, "end": v(408.9, 38.1) * mm});
            skLineSegment(sketch, "E19.6.26.0", {"start": v(408.9, 38.1) * mm, "end": v(434.3, 38.1) * mm});
            skLineSegment(sketch, "E19.9.26.0", {"start": v(434.3, 63.5) * mm, "end": v(434.3, 38.1) * mm});
            skLineSegment(sketch, "E19.0.26.1", {"start": v(408.9, 101.6) * mm, "end": v(434.3, 101.6) * mm});
            skLineSegment(sketch, "E19.3.26.1", {"start": v(408.9, 101.6) * mm, "end": v(408.9, 76.2) * mm});
            skLineSegment(sketch, "E19.6.26.1", {"start": v(408.9, 76.2) * mm, "end": v(434.3, 76.2) * mm});
            skLineSegment(sketch, "E19.9.26.1", {"start": v(434.3, 101.6) * mm, "end": v(434.3, 76.2) * mm});
            skLineSegment(sketch, "E19.0.26.2", {"start": v(408.9, 139.7) * mm, "end": v(434.3, 139.7) * mm});
            skLineSegment(sketch, "E19.3.26.2", {"start": v(408.9, 139.7) * mm, "end": v(408.9, 114.3) * mm});
            skLineSegment(sketch, "E19.6.26.2", {"start": v(408.9, 114.3) * mm, "end": v(434.3, 114.3) * mm});
            skLineSegment(sketch, "E19.9.26.2", {"start": v(434.3, 139.7) * mm, "end": v(434.3, 114.3) * mm});
            skLineSegment(sketch, "E19.0.26.3", {"start": v(408.9, 177.8) * mm, "end": v(434.3, 177.8) * mm});
            skLineSegment(sketch, "E19.3.26.3", {"start": v(408.9, 177.8) * mm, "end": v(408.9, 152.4) * mm});
            skLineSegment(sketch, "E19.6.26.3", {"start": v(408.9, 152.4) * mm, "end": v(434.3, 152.4) * mm});
            skLineSegment(sketch, "E19.9.26.3", {"start": v(434.3, 177.8) * mm, "end": v(434.3, 152.4) * mm});
            skLineSegment(sketch, "E19.0.26.4", {"start": v(408.9, 215.9) * mm, "end": v(434.3, 215.9) * mm});
            skLineSegment(sketch, "E19.3.26.4", {"start": v(408.9, 215.9) * mm, "end": v(408.9, 190.5) * mm});
            skLineSegment(sketch, "E19.6.26.4", {"start": v(408.9, 190.5) * mm, "end": v(434.3, 190.5) * mm});
            skLineSegment(sketch, "E19.9.26.4", {"start": v(434.3, 215.9) * mm, "end": v(434.3, 190.5) * mm});
            skLineSegment(sketch, "E19.0.26.5", {"start": v(408.9, 254) * mm, "end": v(434.3, 254) * mm});
            skLineSegment(sketch, "E19.3.26.5", {"start": v(408.9, 254) * mm, "end": v(408.9, 228.6) * mm});
            skLineSegment(sketch, "E19.6.26.5", {"start": v(408.9, 228.6) * mm, "end": v(434.3, 228.6) * mm});
            skLineSegment(sketch, "E19.9.26.5", {"start": v(434.3, 254) * mm, "end": v(434.3, 228.6) * mm});
            skLineSegment(sketch, "E19.0.26.6", {"start": v(408.9, 292.1) * mm, "end": v(434.3, 292.1) * mm});
            skLineSegment(sketch, "E19.3.26.6", {"start": v(408.9, 292.1) * mm, "end": v(408.9, 266.7) * mm});
            skLineSegment(sketch, "E19.6.26.6", {"start": v(408.9, 266.7) * mm, "end": v(434.3, 266.7) * mm});
            skLineSegment(sketch, "E19.9.26.6", {"start": v(434.3, 292.1) * mm, "end": v(434.3, 266.7) * mm});
            skLineSegment(sketch, "E19.0.26.7", {"start": v(408.9, 330.2) * mm, "end": v(434.3, 330.2) * mm});
            skLineSegment(sketch, "E19.3.26.7", {"start": v(408.9, 330.2) * mm, "end": v(408.9, 304.8) * mm});
            skLineSegment(sketch, "E19.6.26.7", {"start": v(408.9, 304.8) * mm, "end": v(434.3, 304.8) * mm});
            skLineSegment(sketch, "E19.9.26.7", {"start": v(434.3, 330.2) * mm, "end": v(434.3, 304.8) * mm});
            skLineSegment(sketch, "E19.0.26.8", {"start": v(408.9, 368.3) * mm, "end": v(434.3, 368.3) * mm});
            skLineSegment(sketch, "E19.3.26.8", {"start": v(408.9, 368.3) * mm, "end": v(408.9, 342.9) * mm});
            skLineSegment(sketch, "E19.6.26.8", {"start": v(408.9, 342.9) * mm, "end": v(434.3, 342.9) * mm});
            skLineSegment(sketch, "E19.9.26.8", {"start": v(434.3, 368.3) * mm, "end": v(434.3, 342.9) * mm});
            skLineSegment(sketch, "E19.0.26.9", {"start": v(408.9, 406.4) * mm, "end": v(434.3, 406.4) * mm});
            skLineSegment(sketch, "E19.3.26.9", {"start": v(408.9, 406.4) * mm, "end": v(408.9, 381) * mm});
            skLineSegment(sketch, "E19.6.26.9", {"start": v(408.9, 381) * mm, "end": v(434.3, 381) * mm});
            skLineSegment(sketch, "E19.9.26.9", {"start": v(434.3, 406.4) * mm, "end": v(434.3, 381) * mm});
            skLineSegment(sketch, "E19.0.26.10", {"start": v(408.9, 444.5) * mm, "end": v(434.3, 444.5) * mm});
            skLineSegment(sketch, "E19.3.26.10", {"start": v(408.9, 444.5) * mm, "end": v(408.9, 419.1) * mm});
            skLineSegment(sketch, "E19.6.26.10", {"start": v(408.9, 419.1) * mm, "end": v(434.3, 419.1) * mm});
            skLineSegment(sketch, "E19.9.26.10", {"start": v(434.3, 444.5) * mm, "end": v(434.3, 419.1) * mm});
            skLineSegment(sketch, "E19.0.26.11", {"start": v(408.9, 482.6) * mm, "end": v(434.3, 482.6) * mm});
            skLineSegment(sketch, "E19.3.26.11", {"start": v(408.9, 482.6) * mm, "end": v(408.9, 457.2) * mm});
            skLineSegment(sketch, "E19.6.26.11", {"start": v(408.9, 457.2) * mm, "end": v(434.3, 457.2) * mm});
            skLineSegment(sketch, "E19.9.26.11", {"start": v(434.3, 482.6) * mm, "end": v(434.3, 457.2) * mm});
            skLineSegment(sketch, "E19.0.27.0", {"start": v(447, 63.5) * mm, "end": v(472.4, 63.5) * mm});
            skLineSegment(sketch, "E19.3.27.0", {"start": v(447, 63.5) * mm, "end": v(447, 38.1) * mm});
            skLineSegment(sketch, "E19.6.27.0", {"start": v(447, 38.1) * mm, "end": v(472.4, 38.1) * mm});
            skLineSegment(sketch, "E19.9.27.0", {"start": v(472.4, 63.5) * mm, "end": v(472.4, 38.1) * mm});
            skLineSegment(sketch, "E19.0.27.1", {"start": v(447, 101.6) * mm, "end": v(472.4, 101.6) * mm});
            skLineSegment(sketch, "E19.3.27.1", {"start": v(447, 101.6) * mm, "end": v(447, 76.2) * mm});
            skLineSegment(sketch, "E19.6.27.1", {"start": v(447, 76.2) * mm, "end": v(472.4, 76.2) * mm});
            skLineSegment(sketch, "E19.9.27.1", {"start": v(472.4, 101.6) * mm, "end": v(472.4, 76.2) * mm});
            skLineSegment(sketch, "E19.0.27.2", {"start": v(447, 139.7) * mm, "end": v(472.4, 139.7) * mm});
            skLineSegment(sketch, "E19.3.27.2", {"start": v(447, 139.7) * mm, "end": v(447, 114.3) * mm});
            skLineSegment(sketch, "E19.6.27.2", {"start": v(447, 114.3) * mm, "end": v(472.4, 114.3) * mm});
            skLineSegment(sketch, "E19.9.27.2", {"start": v(472.4, 139.7) * mm, "end": v(472.4, 114.3) * mm});
            skLineSegment(sketch, "E19.0.27.3", {"start": v(447, 177.8) * mm, "end": v(472.4, 177.8) * mm});
            skLineSegment(sketch, "E19.3.27.3", {"start": v(447, 177.8) * mm, "end": v(447, 152.4) * mm});
            skLineSegment(sketch, "E19.6.27.3", {"start": v(447, 152.4) * mm, "end": v(472.4, 152.4) * mm});
            skLineSegment(sketch, "E19.9.27.3", {"start": v(472.4, 177.8) * mm, "end": v(472.4, 152.4) * mm});
            skLineSegment(sketch, "E19.0.27.4", {"start": v(447, 215.9) * mm, "end": v(472.4, 215.9) * mm});
            skLineSegment(sketch, "E19.3.27.4", {"start": v(447, 215.9) * mm, "end": v(447, 190.5) * mm});
            skLineSegment(sketch, "E19.6.27.4", {"start": v(447, 190.5) * mm, "end": v(472.4, 190.5) * mm});
            skLineSegment(sketch, "E19.9.27.4", {"start": v(472.4, 215.9) * mm, "end": v(472.4, 190.5) * mm});
            skLineSegment(sketch, "E19.0.27.5", {"start": v(447, 254) * mm, "end": v(472.4, 254) * mm});
            skLineSegment(sketch, "E19.3.27.5", {"start": v(447, 254) * mm, "end": v(447, 228.6) * mm});
            skLineSegment(sketch, "E19.6.27.5", {"start": v(447, 228.6) * mm, "end": v(472.4, 228.6) * mm});
            skLineSegment(sketch, "E19.9.27.5", {"start": v(472.4, 254) * mm, "end": v(472.4, 228.6) * mm});
            skLineSegment(sketch, "E19.0.27.6", {"start": v(447, 292.1) * mm, "end": v(472.4, 292.1) * mm});
            skLineSegment(sketch, "E19.3.27.6", {"start": v(447, 292.1) * mm, "end": v(447, 266.7) * mm});
            skLineSegment(sketch, "E19.6.27.6", {"start": v(447, 266.7) * mm, "end": v(472.4, 266.7) * mm});
            skLineSegment(sketch, "E19.9.27.6", {"start": v(472.4, 292.1) * mm, "end": v(472.4, 266.7) * mm});
            skLineSegment(sketch, "E19.0.27.7", {"start": v(447, 330.2) * mm, "end": v(472.4, 330.2) * mm});
            skLineSegment(sketch, "E19.3.27.7", {"start": v(447, 330.2) * mm, "end": v(447, 304.8) * mm});
            skLineSegment(sketch, "E19.6.27.7", {"start": v(447, 304.8) * mm, "end": v(472.4, 304.8) * mm});
            skLineSegment(sketch, "E19.9.27.7", {"start": v(472.4, 330.2) * mm, "end": v(472.4, 304.8) * mm});
            skLineSegment(sketch, "E19.0.27.8", {"start": v(447, 368.3) * mm, "end": v(472.4, 368.3) * mm});
            skLineSegment(sketch, "E19.3.27.8", {"start": v(447, 368.3) * mm, "end": v(447, 342.9) * mm});
            skLineSegment(sketch, "E19.6.27.8", {"start": v(447, 342.9) * mm, "end": v(472.4, 342.9) * mm});
            skLineSegment(sketch, "E19.9.27.8", {"start": v(472.4, 368.3) * mm, "end": v(472.4, 342.9) * mm});
            skLineSegment(sketch, "E19.0.27.9", {"start": v(447, 406.4) * mm, "end": v(472.4, 406.4) * mm});
            skLineSegment(sketch, "E19.3.27.9", {"start": v(447, 406.4) * mm, "end": v(447, 381) * mm});
            skLineSegment(sketch, "E19.6.27.9", {"start": v(447, 381) * mm, "end": v(472.4, 381) * mm});
            skLineSegment(sketch, "E19.9.27.9", {"start": v(472.4, 406.4) * mm, "end": v(472.4, 381) * mm});
            skLineSegment(sketch, "E19.0.27.10", {"start": v(447, 444.5) * mm, "end": v(472.4, 444.5) * mm});
            skLineSegment(sketch, "E19.3.27.10", {"start": v(447, 444.5) * mm, "end": v(447, 419.1) * mm});
            skLineSegment(sketch, "E19.6.27.10", {"start": v(447, 419.1) * mm, "end": v(472.4, 419.1) * mm});
            skLineSegment(sketch, "E19.9.27.10", {"start": v(472.4, 444.5) * mm, "end": v(472.4, 419.1) * mm});
            skLineSegment(sketch, "E19.0.27.11", {"start": v(447, 482.6) * mm, "end": v(472.4, 482.6) * mm});
            skLineSegment(sketch, "E19.3.27.11", {"start": v(447, 482.6) * mm, "end": v(447, 457.2) * mm});
            skLineSegment(sketch, "E19.6.27.11", {"start": v(447, 457.2) * mm, "end": v(472.4, 457.2) * mm});
            skLineSegment(sketch, "E19.9.27.11", {"start": v(472.4, 482.6) * mm, "end": v(472.4, 457.2) * mm});
            skLineSegment(sketch, "E20.0.28.0", {"start": v(485.1, 63.5) * mm, "end": v(510.5, 63.5) * mm});
            skLineSegment(sketch, "E20.3.28.0", {"start": v(485.1, 63.5) * mm, "end": v(485.1, 38.1) * mm});
            skLineSegment(sketch, "E20.6.28.0", {"start": v(485.1, 38.1) * mm, "end": v(510.5, 38.1) * mm});
            skLineSegment(sketch, "E20.9.28.0", {"start": v(510.5, 63.5) * mm, "end": v(510.5, 38.1) * mm});
            skLineSegment(sketch, "E20.0.28.1", {"start": v(485.1, 101.6) * mm, "end": v(510.5, 101.6) * mm});
            skLineSegment(sketch, "E20.3.28.1", {"start": v(485.1, 101.6) * mm, "end": v(485.1, 76.2) * mm});
            skLineSegment(sketch, "E20.6.28.1", {"start": v(485.1, 76.2) * mm, "end": v(510.5, 76.2) * mm});
            skLineSegment(sketch, "E20.9.28.1", {"start": v(510.5, 101.6) * mm, "end": v(510.5, 76.2) * mm});
            skLineSegment(sketch, "E20.0.28.2", {"start": v(485.1, 139.7) * mm, "end": v(510.5, 139.7) * mm});
            skLineSegment(sketch, "E20.3.28.2", {"start": v(485.1, 139.7) * mm, "end": v(485.1, 114.3) * mm});
            skLineSegment(sketch, "E20.6.28.2", {"start": v(485.1, 114.3) * mm, "end": v(510.5, 114.3) * mm});
            skLineSegment(sketch, "E20.9.28.2", {"start": v(510.5, 139.7) * mm, "end": v(510.5, 114.3) * mm});
            skLineSegment(sketch, "E20.0.28.3", {"start": v(485.1, 177.8) * mm, "end": v(510.5, 177.8) * mm});
            skLineSegment(sketch, "E20.3.28.3", {"start": v(485.1, 177.8) * mm, "end": v(485.1, 152.4) * mm});
            skLineSegment(sketch, "E20.6.28.3", {"start": v(485.1, 152.4) * mm, "end": v(510.5, 152.4) * mm});
            skLineSegment(sketch, "E20.9.28.3", {"start": v(510.5, 177.8) * mm, "end": v(510.5, 152.4) * mm});
            skLineSegment(sketch, "E20.0.28.4", {"start": v(485.1, 215.9) * mm, "end": v(510.5, 215.9) * mm});
            skLineSegment(sketch, "E20.3.28.4", {"start": v(485.1, 215.9) * mm, "end": v(485.1, 190.5) * mm});
            skLineSegment(sketch, "E20.6.28.4", {"start": v(485.1, 190.5) * mm, "end": v(510.5, 190.5) * mm});
            skLineSegment(sketch, "E20.9.28.4", {"start": v(510.5, 215.9) * mm, "end": v(510.5, 190.5) * mm});
            skLineSegment(sketch, "E20.0.28.5", {"start": v(485.1, 254) * mm, "end": v(510.5, 254) * mm});
            skLineSegment(sketch, "E20.3.28.5", {"start": v(485.1, 254) * mm, "end": v(485.1, 228.6) * mm});
            skLineSegment(sketch, "E20.6.28.5", {"start": v(485.1, 228.6) * mm, "end": v(510.5, 228.6) * mm});
            skLineSegment(sketch, "E20.9.28.5", {"start": v(510.5, 254) * mm, "end": v(510.5, 228.6) * mm});
            skLineSegment(sketch, "E20.0.28.6", {"start": v(485.1, 292.1) * mm, "end": v(510.5, 292.1) * mm});
            skLineSegment(sketch, "E20.3.28.6", {"start": v(485.1, 292.1) * mm, "end": v(485.1, 266.7) * mm});
            skLineSegment(sketch, "E20.6.28.6", {"start": v(485.1, 266.7) * mm, "end": v(510.5, 266.7) * mm});
            skLineSegment(sketch, "E20.9.28.6", {"start": v(510.5, 292.1) * mm, "end": v(510.5, 266.7) * mm});
            skLineSegment(sketch, "E20.0.28.7", {"start": v(485.1, 330.2) * mm, "end": v(510.5, 330.2) * mm});
            skLineSegment(sketch, "E20.3.28.7", {"start": v(485.1, 330.2) * mm, "end": v(485.1, 304.8) * mm});
            skLineSegment(sketch, "E20.6.28.7", {"start": v(485.1, 304.8) * mm, "end": v(510.5, 304.8) * mm});
            skLineSegment(sketch, "E20.9.28.7", {"start": v(510.5, 330.2) * mm, "end": v(510.5, 304.8) * mm});
            skLineSegment(sketch, "E20.0.28.8", {"start": v(485.1, 368.3) * mm, "end": v(510.5, 368.3) * mm});
            skLineSegment(sketch, "E20.3.28.8", {"start": v(485.1, 368.3) * mm, "end": v(485.1, 342.9) * mm});
            skLineSegment(sketch, "E20.6.28.8", {"start": v(485.1, 342.9) * mm, "end": v(510.5, 342.9) * mm});
            skLineSegment(sketch, "E20.9.28.8", {"start": v(510.5, 368.3) * mm, "end": v(510.5, 342.9) * mm});
            skLineSegment(sketch, "E20.0.28.9", {"start": v(485.1, 406.4) * mm, "end": v(510.5, 406.4) * mm});
            skLineSegment(sketch, "E20.3.28.9", {"start": v(485.1, 406.4) * mm, "end": v(485.1, 381) * mm});
            skLineSegment(sketch, "E20.6.28.9", {"start": v(485.1, 381) * mm, "end": v(510.5, 381) * mm});
            skLineSegment(sketch, "E20.9.28.9", {"start": v(510.5, 406.4) * mm, "end": v(510.5, 381) * mm});
            skLineSegment(sketch, "E20.0.28.10", {"start": v(485.1, 444.5) * mm, "end": v(510.5, 444.5) * mm});
            skLineSegment(sketch, "E20.3.28.10", {"start": v(485.1, 444.5) * mm, "end": v(485.1, 419.1) * mm});
            skLineSegment(sketch, "E20.6.28.10", {"start": v(485.1, 419.1) * mm, "end": v(510.5, 419.1) * mm});
            skLineSegment(sketch, "E20.9.28.10", {"start": v(510.5, 444.5) * mm, "end": v(510.5, 419.1) * mm});
            skLineSegment(sketch, "E20.0.28.11", {"start": v(485.1, 482.6) * mm, "end": v(510.5, 482.6) * mm});
            skLineSegment(sketch, "E20.3.28.11", {"start": v(485.1, 482.6) * mm, "end": v(485.1, 457.2) * mm});
            skLineSegment(sketch, "E20.6.28.11", {"start": v(485.1, 457.2) * mm, "end": v(510.5, 457.2) * mm});
            skLineSegment(sketch, "E20.9.28.11", {"start": v(510.5, 482.6) * mm, "end": v(510.5, 457.2) * mm});
            skLineSegment(sketch, "E20.0.29.0", {"start": v(523.2, 63.5) * mm, "end": v(548.6, 63.5) * mm});
            skLineSegment(sketch, "E20.3.29.0", {"start": v(523.2, 63.5) * mm, "end": v(523.2, 38.1) * mm});
            skLineSegment(sketch, "E20.6.29.0", {"start": v(523.2, 38.1) * mm, "end": v(548.6, 38.1) * mm});
            skLineSegment(sketch, "E20.9.29.0", {"start": v(548.6, 63.5) * mm, "end": v(548.6, 38.1) * mm});
            skLineSegment(sketch, "E20.0.29.1", {"start": v(523.2, 101.6) * mm, "end": v(548.6, 101.6) * mm});
            skLineSegment(sketch, "E20.3.29.1", {"start": v(523.2, 101.6) * mm, "end": v(523.2, 76.2) * mm});
            skLineSegment(sketch, "E20.6.29.1", {"start": v(523.2, 76.2) * mm, "end": v(548.6, 76.2) * mm});
            skLineSegment(sketch, "E20.9.29.1", {"start": v(548.6, 101.6) * mm, "end": v(548.6, 76.2) * mm});
            skLineSegment(sketch, "E20.0.29.2", {"start": v(523.2, 139.7) * mm, "end": v(548.6, 139.7) * mm});
            skLineSegment(sketch, "E20.3.29.2", {"start": v(523.2, 139.7) * mm, "end": v(523.2, 114.3) * mm});
            skLineSegment(sketch, "E20.6.29.2", {"start": v(523.2, 114.3) * mm, "end": v(548.6, 114.3) * mm});
            skLineSegment(sketch, "E20.9.29.2", {"start": v(548.6, 139.7) * mm, "end": v(548.6, 114.3) * mm});
            skLineSegment(sketch, "E20.0.29.3", {"start": v(523.2, 177.8) * mm, "end": v(548.6, 177.8) * mm});
            skLineSegment(sketch, "E20.3.29.3", {"start": v(523.2, 177.8) * mm, "end": v(523.2, 152.4) * mm});
            skLineSegment(sketch, "E20.6.29.3", {"start": v(523.2, 152.4) * mm, "end": v(548.6, 152.4) * mm});
            skLineSegment(sketch, "E20.9.29.3", {"start": v(548.6, 177.8) * mm, "end": v(548.6, 152.4) * mm});
            skLineSegment(sketch, "E20.0.29.4", {"start": v(523.2, 215.9) * mm, "end": v(548.6, 215.9) * mm});
            skLineSegment(sketch, "E20.3.29.4", {"start": v(523.2, 215.9) * mm, "end": v(523.2, 190.5) * mm});
            skLineSegment(sketch, "E20.6.29.4", {"start": v(523.2, 190.5) * mm, "end": v(548.6, 190.5) * mm});
            skLineSegment(sketch, "E20.9.29.4", {"start": v(548.6, 215.9) * mm, "end": v(548.6, 190.5) * mm});
            skLineSegment(sketch, "E20.0.29.5", {"start": v(523.2, 254) * mm, "end": v(548.6, 254) * mm});
            skLineSegment(sketch, "E20.3.29.5", {"start": v(523.2, 254) * mm, "end": v(523.2, 228.6) * mm});
            skLineSegment(sketch, "E20.6.29.5", {"start": v(523.2, 228.6) * mm, "end": v(548.6, 228.6) * mm});
            skLineSegment(sketch, "E20.9.29.5", {"start": v(548.6, 254) * mm, "end": v(548.6, 228.6) * mm});
            skLineSegment(sketch, "E20.0.29.6", {"start": v(523.2, 292.1) * mm, "end": v(548.6, 292.1) * mm});
            skLineSegment(sketch, "E20.3.29.6", {"start": v(523.2, 292.1) * mm, "end": v(523.2, 266.7) * mm});
            skLineSegment(sketch, "E20.6.29.6", {"start": v(523.2, 266.7) * mm, "end": v(548.6, 266.7) * mm});
            skLineSegment(sketch, "E20.9.29.6", {"start": v(548.6, 292.1) * mm, "end": v(548.6, 266.7) * mm});
            skLineSegment(sketch, "E20.0.29.7", {"start": v(523.2, 330.2) * mm, "end": v(548.6, 330.2) * mm});
            skLineSegment(sketch, "E20.3.29.7", {"start": v(523.2, 330.2) * mm, "end": v(523.2, 304.8) * mm});
            skLineSegment(sketch, "E20.6.29.7", {"start": v(523.2, 304.8) * mm, "end": v(548.6, 304.8) * mm});
            skLineSegment(sketch, "E20.9.29.7", {"start": v(548.6, 330.2) * mm, "end": v(548.6, 304.8) * mm});
            skLineSegment(sketch, "E20.0.29.8", {"start": v(523.2, 368.3) * mm, "end": v(548.6, 368.3) * mm});
            skLineSegment(sketch, "E20.3.29.8", {"start": v(523.2, 368.3) * mm, "end": v(523.2, 342.9) * mm});
            skLineSegment(sketch, "E20.6.29.8", {"start": v(523.2, 342.9) * mm, "end": v(548.6, 342.9) * mm});
            skLineSegment(sketch, "E20.9.29.8", {"start": v(548.6, 368.3) * mm, "end": v(548.6, 342.9) * mm});
            skLineSegment(sketch, "E20.0.29.9", {"start": v(523.2, 406.4) * mm, "end": v(548.6, 406.4) * mm});
            skLineSegment(sketch, "E20.3.29.9", {"start": v(523.2, 406.4) * mm, "end": v(523.2, 381) * mm});
            skLineSegment(sketch, "E20.6.29.9", {"start": v(523.2, 381) * mm, "end": v(548.6, 381) * mm});
            skLineSegment(sketch, "E20.9.29.9", {"start": v(548.6, 406.4) * mm, "end": v(548.6, 381) * mm});
            skLineSegment(sketch, "E20.0.29.10", {"start": v(523.2, 444.5) * mm, "end": v(548.6, 444.5) * mm});
            skLineSegment(sketch, "E20.3.29.10", {"start": v(523.2, 444.5) * mm, "end": v(523.2, 419.1) * mm});
            skLineSegment(sketch, "E20.6.29.10", {"start": v(523.2, 419.1) * mm, "end": v(548.6, 419.1) * mm});
            skLineSegment(sketch, "E20.9.29.10", {"start": v(548.6, 444.5) * mm, "end": v(548.6, 419.1) * mm});
            skLineSegment(sketch, "E20.0.29.11", {"start": v(523.2, 482.6) * mm, "end": v(548.6, 482.6) * mm});
            skLineSegment(sketch, "E20.3.29.11", {"start": v(523.2, 482.6) * mm, "end": v(523.2, 457.2) * mm});
            skLineSegment(sketch, "E20.6.29.11", {"start": v(523.2, 457.2) * mm, "end": v(548.6, 457.2) * mm});
            skLineSegment(sketch, "E20.9.29.11", {"start": v(548.6, 482.6) * mm, "end": v(548.6, 457.2) * mm});
            skLineSegment(sketch, "E20.0.30.0", {"start": v(561.3, 63.5) * mm, "end": v(586.7, 63.5) * mm});
            skLineSegment(sketch, "E20.3.30.0", {"start": v(561.3, 63.5) * mm, "end": v(561.3, 38.1) * mm});
            skLineSegment(sketch, "E20.6.30.0", {"start": v(561.3, 38.1) * mm, "end": v(586.7, 38.1) * mm});
            skLineSegment(sketch, "E20.9.30.0", {"start": v(586.7, 63.5) * mm, "end": v(586.7, 38.1) * mm});
            skLineSegment(sketch, "E20.0.30.1", {"start": v(561.3, 101.6) * mm, "end": v(586.7, 101.6) * mm});
            skLineSegment(sketch, "E20.3.30.1", {"start": v(561.3, 101.6) * mm, "end": v(561.3, 76.2) * mm});
            skLineSegment(sketch, "E20.6.30.1", {"start": v(561.3, 76.2) * mm, "end": v(586.7, 76.2) * mm});
            skLineSegment(sketch, "E20.9.30.1", {"start": v(586.7, 101.6) * mm, "end": v(586.7, 76.2) * mm});
            skLineSegment(sketch, "E20.0.30.2", {"start": v(561.3, 139.7) * mm, "end": v(586.7, 139.7) * mm});
            skLineSegment(sketch, "E20.3.30.2", {"start": v(561.3, 139.7) * mm, "end": v(561.3, 114.3) * mm});
            skLineSegment(sketch, "E20.6.30.2", {"start": v(561.3, 114.3) * mm, "end": v(586.7, 114.3) * mm});
            skLineSegment(sketch, "E20.9.30.2", {"start": v(586.7, 139.7) * mm, "end": v(586.7, 114.3) * mm});
            skLineSegment(sketch, "E20.0.30.3", {"start": v(561.3, 177.8) * mm, "end": v(586.7, 177.8) * mm});
            skLineSegment(sketch, "E20.3.30.3", {"start": v(561.3, 177.8) * mm, "end": v(561.3, 152.4) * mm});
            skLineSegment(sketch, "E20.6.30.3", {"start": v(561.3, 152.4) * mm, "end": v(586.7, 152.4) * mm});
            skLineSegment(sketch, "E20.9.30.3", {"start": v(586.7, 177.8) * mm, "end": v(586.7, 152.4) * mm});
            skLineSegment(sketch, "E20.0.30.4", {"start": v(561.3, 215.9) * mm, "end": v(586.7, 215.9) * mm});
            skLineSegment(sketch, "E20.3.30.4", {"start": v(561.3, 215.9) * mm, "end": v(561.3, 190.5) * mm});
            skLineSegment(sketch, "E20.6.30.4", {"start": v(561.3, 190.5) * mm, "end": v(586.7, 190.5) * mm});
            skLineSegment(sketch, "E20.9.30.4", {"start": v(586.7, 215.9) * mm, "end": v(586.7, 190.5) * mm});
            skLineSegment(sketch, "E20.0.30.5", {"start": v(561.3, 254) * mm, "end": v(586.7, 254) * mm});
            skLineSegment(sketch, "E20.3.30.5", {"start": v(561.3, 254) * mm, "end": v(561.3, 228.6) * mm});
            skLineSegment(sketch, "E20.6.30.5", {"start": v(561.3, 228.6) * mm, "end": v(586.7, 228.6) * mm});
            skLineSegment(sketch, "E20.9.30.5", {"start": v(586.7, 254) * mm, "end": v(586.7, 228.6) * mm});
            skLineSegment(sketch, "E20.0.30.6", {"start": v(561.3, 292.1) * mm, "end": v(586.7, 292.1) * mm});
            skLineSegment(sketch, "E20.3.30.6", {"start": v(561.3, 292.1) * mm, "end": v(561.3, 266.7) * mm});
            skLineSegment(sketch, "E20.6.30.6", {"start": v(561.3, 266.7) * mm, "end": v(586.7, 266.7) * mm});
            skLineSegment(sketch, "E20.9.30.6", {"start": v(586.7, 292.1) * mm, "end": v(586.7, 266.7) * mm});
            skLineSegment(sketch, "E20.0.30.7", {"start": v(561.3, 330.2) * mm, "end": v(586.7, 330.2) * mm});
            skLineSegment(sketch, "E20.3.30.7", {"start": v(561.3, 330.2) * mm, "end": v(561.3, 304.8) * mm});
            skLineSegment(sketch, "E20.6.30.7", {"start": v(561.3, 304.8) * mm, "end": v(586.7, 304.8) * mm});
            skLineSegment(sketch, "E20.9.30.7", {"start": v(586.7, 330.2) * mm, "end": v(586.7, 304.8) * mm});
            skLineSegment(sketch, "E20.0.30.8", {"start": v(561.3, 368.3) * mm, "end": v(586.7, 368.3) * mm});
            skLineSegment(sketch, "E20.3.30.8", {"start": v(561.3, 368.3) * mm, "end": v(561.3, 342.9) * mm});
            skLineSegment(sketch, "E20.6.30.8", {"start": v(561.3, 342.9) * mm, "end": v(586.7, 342.9) * mm});
            skLineSegment(sketch, "E20.9.30.8", {"start": v(586.7, 368.3) * mm, "end": v(586.7, 342.9) * mm});
            skLineSegment(sketch, "E20.0.30.9", {"start": v(561.3, 406.4) * mm, "end": v(586.7, 406.4) * mm});
            skLineSegment(sketch, "E20.3.30.9", {"start": v(561.3, 406.4) * mm, "end": v(561.3, 381) * mm});
            skLineSegment(sketch, "E20.6.30.9", {"start": v(561.3, 381) * mm, "end": v(586.7, 381) * mm});
            skLineSegment(sketch, "E20.9.30.9", {"start": v(586.7, 406.4) * mm, "end": v(586.7, 381) * mm});
            skLineSegment(sketch, "E20.0.30.10", {"start": v(561.3, 444.5) * mm, "end": v(586.7, 444.5) * mm});
            skLineSegment(sketch, "E20.3.30.10", {"start": v(561.3, 444.5) * mm, "end": v(561.3, 419.1) * mm});
            skLineSegment(sketch, "E20.6.30.10", {"start": v(561.3, 419.1) * mm, "end": v(586.7, 419.1) * mm});
            skLineSegment(sketch, "E20.9.30.10", {"start": v(586.7, 444.5) * mm, "end": v(586.7, 419.1) * mm});
            skLineSegment(sketch, "E20.0.30.11", {"start": v(561.3, 482.6) * mm, "end": v(586.7, 482.6) * mm});
            skLineSegment(sketch, "E20.3.30.11", {"start": v(561.3, 482.6) * mm, "end": v(561.3, 457.2) * mm});
            skLineSegment(sketch, "E20.6.30.11", {"start": v(561.3, 457.2) * mm, "end": v(586.7, 457.2) * mm});
            skLineSegment(sketch, "E20.9.30.11", {"start": v(586.7, 482.6) * mm, "end": v(586.7, 457.2) * mm});
            skLineSegment(sketch, "E20.0.31.0", {"start": v(599.4, 63.5) * mm, "end": v(624.8, 63.5) * mm});
            skLineSegment(sketch, "E20.3.31.0", {"start": v(599.4, 63.5) * mm, "end": v(599.4, 38.1) * mm});
            skLineSegment(sketch, "E20.6.31.0", {"start": v(599.4, 38.1) * mm, "end": v(624.8, 38.1) * mm});
            skLineSegment(sketch, "E20.9.31.0", {"start": v(624.8, 63.5) * mm, "end": v(624.8, 38.1) * mm});
            skLineSegment(sketch, "E20.0.31.1", {"start": v(599.4, 101.6) * mm, "end": v(624.8, 101.6) * mm});
            skLineSegment(sketch, "E20.3.31.1", {"start": v(599.4, 101.6) * mm, "end": v(599.4, 76.2) * mm});
            skLineSegment(sketch, "E20.6.31.1", {"start": v(599.4, 76.2) * mm, "end": v(624.8, 76.2) * mm});
            skLineSegment(sketch, "E20.9.31.1", {"start": v(624.8, 101.6) * mm, "end": v(624.8, 76.2) * mm});
            skLineSegment(sketch, "E20.0.31.2", {"start": v(599.4, 139.7) * mm, "end": v(624.8, 139.7) * mm});
            skLineSegment(sketch, "E20.3.31.2", {"start": v(599.4, 139.7) * mm, "end": v(599.4, 114.3) * mm});
            skLineSegment(sketch, "E20.6.31.2", {"start": v(599.4, 114.3) * mm, "end": v(624.8, 114.3) * mm});
            skLineSegment(sketch, "E20.9.31.2", {"start": v(624.8, 139.7) * mm, "end": v(624.8, 114.3) * mm});
            skLineSegment(sketch, "E20.0.31.3", {"start": v(599.4, 177.8) * mm, "end": v(624.8, 177.8) * mm});
            skLineSegment(sketch, "E20.3.31.3", {"start": v(599.4, 177.8) * mm, "end": v(599.4, 152.4) * mm});
            skLineSegment(sketch, "E20.6.31.3", {"start": v(599.4, 152.4) * mm, "end": v(624.8, 152.4) * mm});
            skLineSegment(sketch, "E20.9.31.3", {"start": v(624.8, 177.8) * mm, "end": v(624.8, 152.4) * mm});
            skLineSegment(sketch, "E20.0.31.4", {"start": v(599.4, 215.9) * mm, "end": v(624.8, 215.9) * mm});
            skLineSegment(sketch, "E20.3.31.4", {"start": v(599.4, 215.9) * mm, "end": v(599.4, 190.5) * mm});
            skLineSegment(sketch, "E20.6.31.4", {"start": v(599.4, 190.5) * mm, "end": v(624.8, 190.5) * mm});
            skLineSegment(sketch, "E20.9.31.4", {"start": v(624.8, 215.9) * mm, "end": v(624.8, 190.5) * mm});
            skLineSegment(sketch, "E20.0.31.5", {"start": v(599.4, 254) * mm, "end": v(624.8, 254) * mm});
            skLineSegment(sketch, "E20.3.31.5", {"start": v(599.4, 254) * mm, "end": v(599.4, 228.6) * mm});
            skLineSegment(sketch, "E20.6.31.5", {"start": v(599.4, 228.6) * mm, "end": v(624.8, 228.6) * mm});
            skLineSegment(sketch, "E20.9.31.5", {"start": v(624.8, 254) * mm, "end": v(624.8, 228.6) * mm});
            skLineSegment(sketch, "E20.0.31.6", {"start": v(599.4, 292.1) * mm, "end": v(624.8, 292.1) * mm});
            skLineSegment(sketch, "E20.3.31.6", {"start": v(599.4, 292.1) * mm, "end": v(599.4, 266.7) * mm});
            skLineSegment(sketch, "E20.6.31.6", {"start": v(599.4, 266.7) * mm, "end": v(624.8, 266.7) * mm});
            skLineSegment(sketch, "E20.9.31.6", {"start": v(624.8, 292.1) * mm, "end": v(624.8, 266.7) * mm});
            skLineSegment(sketch, "E20.0.31.7", {"start": v(599.4, 330.2) * mm, "end": v(624.8, 330.2) * mm});
            skLineSegment(sketch, "E20.3.31.7", {"start": v(599.4, 330.2) * mm, "end": v(599.4, 304.8) * mm});
            skLineSegment(sketch, "E20.6.31.7", {"start": v(599.4, 304.8) * mm, "end": v(624.8, 304.8) * mm});
            skLineSegment(sketch, "E20.9.31.7", {"start": v(624.8, 330.2) * mm, "end": v(624.8, 304.8) * mm});
            skLineSegment(sketch, "E20.0.31.8", {"start": v(599.4, 368.3) * mm, "end": v(624.8, 368.3) * mm});
            skLineSegment(sketch, "E20.3.31.8", {"start": v(599.4, 368.3) * mm, "end": v(599.4, 342.9) * mm});
            skLineSegment(sketch, "E20.6.31.8", {"start": v(599.4, 342.9) * mm, "end": v(624.8, 342.9) * mm});
            skLineSegment(sketch, "E20.9.31.8", {"start": v(624.8, 368.3) * mm, "end": v(624.8, 342.9) * mm});
            skLineSegment(sketch, "E20.0.31.9", {"start": v(599.4, 406.4) * mm, "end": v(624.8, 406.4) * mm});
            skLineSegment(sketch, "E20.3.31.9", {"start": v(599.4, 406.4) * mm, "end": v(599.4, 381) * mm});
            skLineSegment(sketch, "E20.6.31.9", {"start": v(599.4, 381) * mm, "end": v(624.8, 381) * mm});
            skLineSegment(sketch, "E20.9.31.9", {"start": v(624.8, 406.4) * mm, "end": v(624.8, 381) * mm});
            skLineSegment(sketch, "E20.0.31.10", {"start": v(599.4, 444.5) * mm, "end": v(624.8, 444.5) * mm});
            skLineSegment(sketch, "E20.3.31.10", {"start": v(599.4, 444.5) * mm, "end": v(599.4, 419.1) * mm});
            skLineSegment(sketch, "E20.6.31.10", {"start": v(599.4, 419.1) * mm, "end": v(624.8, 419.1) * mm});
            skLineSegment(sketch, "E20.9.31.10", {"start": v(624.8, 444.5) * mm, "end": v(624.8, 419.1) * mm});
            skLineSegment(sketch, "E20.0.31.11", {"start": v(599.4, 482.6) * mm, "end": v(624.8, 482.6) * mm});
            skLineSegment(sketch, "E20.3.31.11", {"start": v(599.4, 482.6) * mm, "end": v(599.4, 457.2) * mm});
            skLineSegment(sketch, "E20.6.31.11", {"start": v(599.4, 457.2) * mm, "end": v(624.8, 457.2) * mm});
            skLineSegment(sketch, "E20.9.31.11", {"start": v(624.8, 482.6) * mm, "end": v(624.8, 457.2) * mm});
            skSolve(sketch);
        }
        {
            var Q0;
            Q0 = qSketchRegion(id + "F7", true);
            extrude(context, id + "F8", {"entities" : qUnion([Q0]), "operationType" : NewBodyOperationType.REMOVE, "oppositeDirection" : true, "depth" : 762 * mm});
        }
        {
            var Q0;
            Q0 = qSketchRegion(id + "F6", true);
            extrude(context, id + "F9", {"entities" : qUnion([Q0]), "operationType" : NewBodyOperationType.ADD, "endBound" : BoundingType.SYMMETRIC, "depth" : 50.8 * mm});
        }
    });
